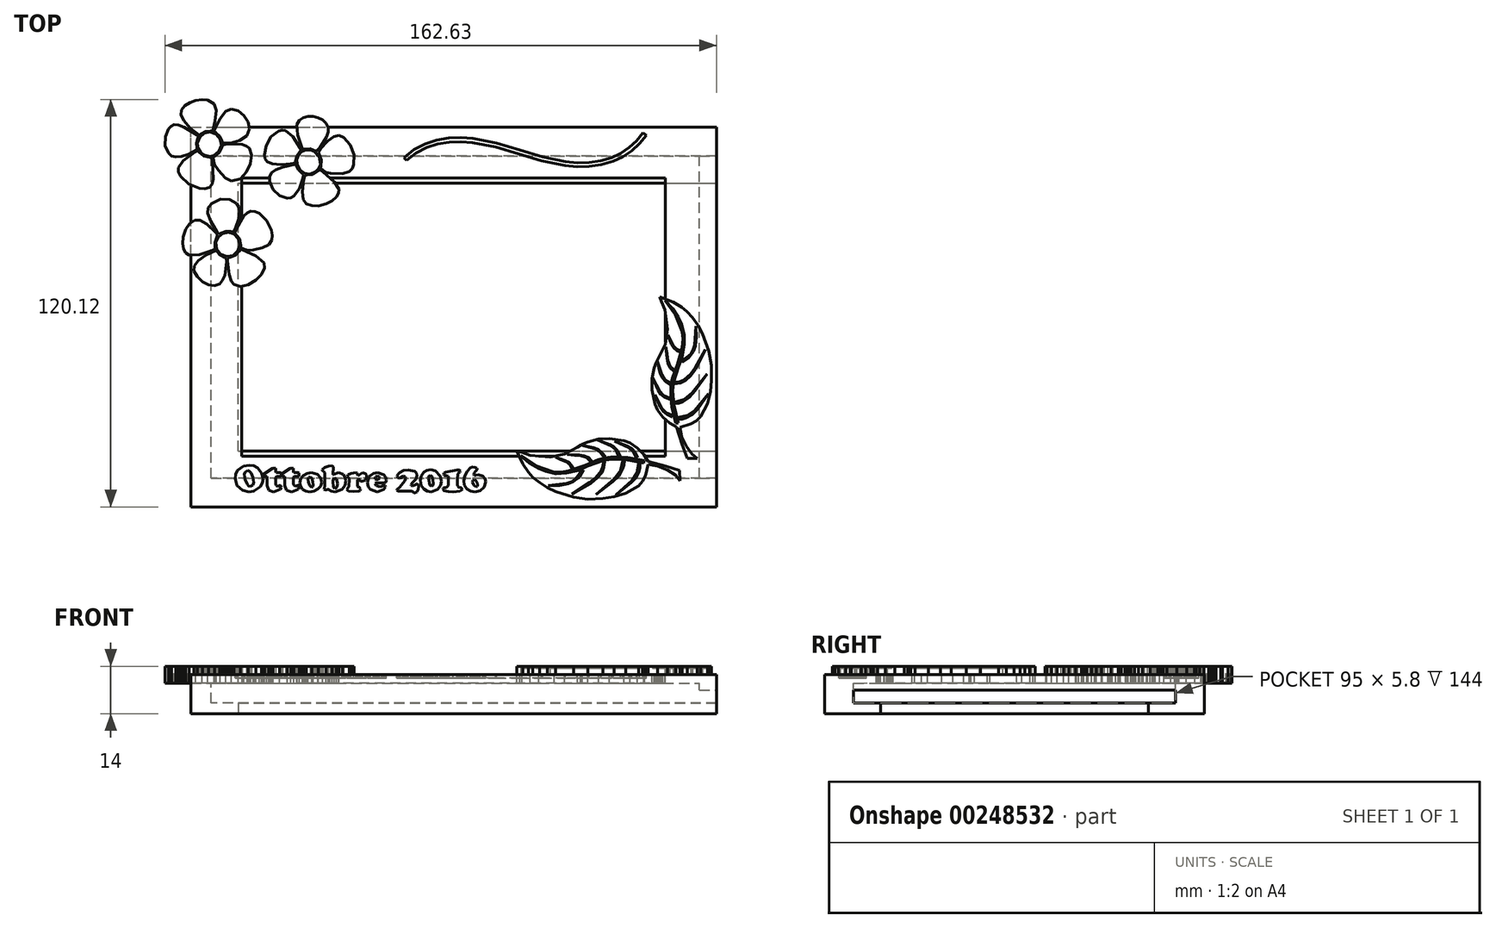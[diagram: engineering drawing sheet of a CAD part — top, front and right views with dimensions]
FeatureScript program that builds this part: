
annotation { "Feature Type Name" : "Feature", "Feature Type Description" : "" }
export const myFeature = defineFeature(function(context is Context, id is Id, definition is map)
    precondition{}
    {
        {
            var Q0;
            Q0=qCreatedBy(makeId("Top.planeOp"),FACE);
            var sketch = newSketch(context, id + "F0", { "sketchPlane" : qUnion([Q0])});
            skLineSegment(sketch, "E0", {"start": v(-51.6, -43.86) * mm, "end": v(-51.6, 51.14) * mm});
            skLineSegment(sketch, "E1", {"start": v(-51.6, 51.14) * mm, "end": v(91.4, 51.14) * mm});
            skLineSegment(sketch, "E2", {"start": v(92.4, -43.86) * mm, "end": v(-51.6, -43.86) * mm});
            skLineSegment(sketch, "E3", {"start": v(97.4, 59.64) * mm, "end": v(97.4, -52.22) * mm});
            skLineSegment(sketch, "E4", {"start": v(97.4, -52.36) * mm, "end": v(-57.31, -52.36) * mm});
            skLineSegment(sketch, "E5", {"start": v(-57.6, -52.22) * mm, "end": v(-57.6, 59.64) * mm});
            skLineSegment(sketch, "E6", {"start": v(-57.6, 59.64) * mm, "end": v(97.4, 59.64) * mm});
            skLineSegment(sketch, "E7", {"start": v(-42.6, 44.64) * mm, "end": v(-42.6, -37.36) * mm});
            skLineSegment(sketch, "E8", {"start": v(-42.6, -37.36) * mm, "end": v(82.4, -37.36) * mm});
            skLineSegment(sketch, "E9", {"start": v(82.4, -37.36) * mm, "end": v(82.4, 44.64) * mm});
            skLineSegment(sketch, "E10", {"start": v(82.4, 44.64) * mm, "end": v(-42.31, 44.64) * mm});
            skLineSegment(sketch, "E11", {"start": v(-57.6, -52.22) * mm, "end": v(-57.6, -52.36) * mm});
            skLineSegment(sketch, "E12", {"start": v(-57.6, -52.36) * mm, "end": v(-57.31, -52.36) * mm});
            skLineSegment(sketch, "E13", {"start": v(97.4, -52.22) * mm, "end": v(97.4, -52.36) * mm});
            skLineSegment(sketch, "E14", {"start": v(-42.31, 44.64) * mm, "end": v(-42.6, 44.64) * mm});
            skLineSegment(sketch, "E15", {"start": v(91.4, 51.14) * mm, "end": v(97.4, 51.14) * mm});
            skLineSegment(sketch, "E16", {"start": v(92.4, -43.86) * mm, "end": v(97.4, -43.86) * mm});
            skLineSegment(sketch, "E17", {"start": v(92.4, -43.86) * mm, "end": v(92.4, 51.14) * mm});
            skLineSegment(sketch, "E18.top", {"start": v(92.4, 51.14) * mm, "end": v(97.4, 51.14) * mm});
            skLineSegment(sketch, "E18.right", {"start": v(97.4, -43.86) * mm, "end": v(97.4, 51.14) * mm});
            skSolve(sketch);
        }
        {
            var Q0;
            Q0=makeQuery(id+"F0.imprint","IMPRINT",FACE,{"disambiguationData":[TD([[makeQuery(id+"F0.imprint","IMPRINT",EDGE,{"derivedFrom":sQuery(id+"F0.wireOp",EDGE,"E0")}),-1.0]])]});
            var Q1;
            Q1=makeQuery(id+"F0.imprint","IMPRINT",FACE,{"disambiguationData":[TD([[makeQuery(id+"F0.imprint","IMPRINT",EDGE,{"derivedFrom":sQuery(id+"F0.wireOp",EDGE,"E0")}),1.0]])]});
            var Q2;
            Q2=makeQuery(id+"F0.imprint","IMPRINT",FACE,{"disambiguationData":[TD([[makeQuery(id+"F0.imprint","IMPRINT",EDGE,{"derivedFrom":sQuery(id+"F0.wireOp",EDGE,"3e203181-d2fc-4a26-8add-b23972c1667f")}),1.0]])]});
            var Q3;
            Q3=makeQuery(id+"F0.imprint","IMPRINT",FACE,{"disambiguationData":[TD([[makeQuery(id+"F0.imprint","IMPRINT",EDGE,{"derivedFrom":sQuery(id+"F0.wireOp",EDGE,"E16")}),1.0]])]});
            extrude(context, id + "F1", {"entities" : qUnion([Q0, Q1, Q2, Q3]), "depth" : 2.5 * mm});
        }
        {
            var Q0;
            Q0=makeQuery(id+"F0.imprint","IMPRINT",FACE,{"disambiguationData":[TD([[makeQuery(id+"F0.imprint","IMPRINT",EDGE,{"derivedFrom":sQuery(id+"F0.wireOp",EDGE,"E0")}),1.0]])]});
            extrude(context, id + "F2", {"entities" : qUnion([Q0]), "operationType" : NewBodyOperationType.ADD, "oppositeDirection" : true, "depth" : 9 * mm});
        }
        {
            var Q0;
            Q0=makeQuery(id+"F0.imprint","IMPRINT",FACE,{"disambiguationData":[TD([[makeQuery(id+"F0.imprint","IMPRINT",EDGE,{"derivedFrom":sQuery(id+"F0.wireOp",EDGE,"E16")}),1.0]])]});
            extrude(context, id + "F3", {"entities" : qUnion([Q0]), "operationType" : NewBodyOperationType.ADD, "oppositeDirection" : true, "depth" : 2 * mm});
        }
        {
            var Q0;
            Q0=makeQuery(id+"F1.opExtrude","CAP_FACE",FACE,{"disambiguationData":[OSD([sQuery(id+"F0.wireOp",EDGE,"E3"),sQuery(id+"F0.wireOp",EDGE,"E4"),sQuery(id+"F0.wireOp",EDGE,"E5"),sQuery(id+"F0.wireOp",EDGE,"E6"),sQuery(id+"F0.wireOp",EDGE,"E7"),sQuery(id+"F0.wireOp",EDGE,"E8"),sQuery(id+"F0.wireOp",EDGE,"E9"),sQuery(id+"F0.wireOp",EDGE,"E10"),sQuery(id+"F0.wireOp",EDGE,"E11"),sQuery(id+"F0.wireOp",EDGE,"E12"),sQuery(id+"F0.wireOp",EDGE,"E13"),sQuery(id+"F0.wireOp",EDGE,"E14")])],"isStart":false});
            var sketch = newSketch(context, id + "F4", { "sketchPlane" : qUnion([Q0])});
            skLineSegment(sketch, "E19", {"start": v(-43.34, 12.36) * mm, "end": v(-44.56, 12.62) * mm});
            skLineSegment(sketch, "E20", {"start": v(-44.56, 12.62) * mm, "end": v(-45.45, 13.22) * mm});
            skLineSegment(sketch, "E21", {"start": v(-45.45, 13.22) * mm, "end": v(-46.62, 15.86) * mm});
            skLineSegment(sketch, "E22", {"start": v(-46.62, 15.86) * mm, "end": v(-46.97, 17.25) * mm});
            skLineSegment(sketch, "E23", {"start": v(-46.97, 17.25) * mm, "end": v(-47.22, 16.26) * mm});
            skLineSegment(sketch, "E24", {"start": v(-47.22, 16.26) * mm, "end": v(-48.3, 13.7) * mm});
            skLineSegment(sketch, "E25", {"start": v(-48.3, 13.7) * mm, "end": v(-49.1, 13.03) * mm});
            skLineSegment(sketch, "E26", {"start": v(-49.1, 13.03) * mm, "end": v(-50.16, 12.66) * mm});
            skLineSegment(sketch, "E27", {"start": v(-50.16, 12.66) * mm, "end": v(-52.63, 12.87) * mm});
            skLineSegment(sketch, "E28", {"start": v(-52.63, 12.87) * mm, "end": v(-54.94, 14.2) * mm});
            skLineSegment(sketch, "E29", {"start": v(-54.94, 14.2) * mm, "end": v(-56.58, 16.2) * mm});
            skLineSegment(sketch, "E30", {"start": v(-56.58, 16.2) * mm, "end": v(-57.03, 18.45) * mm});
            skLineSegment(sketch, "E31", {"start": v(-57.03, 18.45) * mm, "end": v(-56.32, 19.86) * mm});
            skLineSegment(sketch, "E32", {"start": v(-56.32, 19.86) * mm, "end": v(-54.27, 21.6) * mm});
            skLineSegment(sketch, "E33", {"start": v(-54.27, 21.6) * mm, "end": v(-54.18, 21.75) * mm});
            skLineSegment(sketch, "E34", {"start": v(-54.18, 21.75) * mm, "end": v(-55.13, 21.62) * mm});
            skLineSegment(sketch, "E35", {"start": v(-55.13, 21.62) * mm, "end": v(-58.2, 21.58) * mm});
            skLineSegment(sketch, "E36", {"start": v(-58.2, 21.58) * mm, "end": v(-59.42, 22.34) * mm});
            skLineSegment(sketch, "E37", {"start": v(-59.42, 22.34) * mm, "end": v(-60.13, 23.68) * mm});
            skLineSegment(sketch, "E38", {"start": v(-60.13, 23.68) * mm, "end": v(-60.37, 25.4) * mm});
            skLineSegment(sketch, "E39", {"start": v(-60.37, 25.4) * mm, "end": v(-60.18, 27.31) * mm});
            skLineSegment(sketch, "E40", {"start": v(-60.18, 27.31) * mm, "end": v(-59.6, 29.19) * mm});
            skLineSegment(sketch, "E41", {"start": v(-59.6, 29.19) * mm, "end": v(-58.69, 30.83) * mm});
            skLineSegment(sketch, "E42", {"start": v(-58.69, 30.83) * mm, "end": v(-57.46, 32.04) * mm});
            skLineSegment(sketch, "E43", {"start": v(-57.46, 32.04) * mm, "end": v(-55.97, 32.62) * mm});
            skLineSegment(sketch, "E44", {"start": v(-55.97, 32.62) * mm, "end": v(-54.14, 32.17) * mm});
            skLineSegment(sketch, "E45", {"start": v(-54.14, 32.17) * mm, "end": v(-51.85, 30.54) * mm});
            skLineSegment(sketch, "E46", {"start": v(-51.85, 30.54) * mm, "end": v(-51.1, 29.93) * mm});
            skLineSegment(sketch, "E47", {"start": v(-51.1, 29.93) * mm, "end": v(-51.57, 30.85) * mm});
            skLineSegment(sketch, "E48", {"start": v(-51.57, 30.85) * mm, "end": v(-52.74, 33.3) * mm});
            skLineSegment(sketch, "E49", {"start": v(-52.74, 33.3) * mm, "end": v(-53.03, 35.08) * mm});
            skLineSegment(sketch, "E50", {"start": v(-53.03, 35.08) * mm, "end": v(-52.68, 36.16) * mm});
            skLineSegment(sketch, "E51", {"start": v(-52.68, 36.16) * mm, "end": v(-51.98, 37.1) * mm});
            skLineSegment(sketch, "E52", {"start": v(-51.98, 37.1) * mm, "end": v(-49.88, 38.4) * mm});
            skLineSegment(sketch, "E53", {"start": v(-49.88, 38.4) * mm, "end": v(-47.29, 38.79) * mm});
            skLineSegment(sketch, "E54", {"start": v(-47.29, 38.79) * mm, "end": v(-44.81, 38.05) * mm});
            skLineSegment(sketch, "E55", {"start": v(-44.81, 38.05) * mm, "end": v(-43.79, 37.16) * mm});
            skLineSegment(sketch, "E56", {"start": v(-43.79, 37.16) * mm, "end": v(-43.16, 36) * mm});
            skLineSegment(sketch, "E57", {"start": v(-43.16, 36) * mm, "end": v(-42.94, 34.58) * mm});
            skLineSegment(sketch, "E58", {"start": v(-42.94, 34.58) * mm, "end": v(-43.12, 32.88) * mm});
            skLineSegment(sketch, "E59", {"start": v(-43.12, 32.88) * mm, "end": v(-43.13, 32.45) * mm});
            skLineSegment(sketch, "E60", {"start": v(-43.13, 32.45) * mm, "end": v(-42.7, 32.97) * mm});
            skLineSegment(sketch, "E61", {"start": v(-42.7, 32.97) * mm, "end": v(-41.54, 34.37) * mm});
            skLineSegment(sketch, "E62", {"start": v(-41.54, 34.37) * mm, "end": v(-40.34, 35.1) * mm});
            skLineSegment(sketch, "E63", {"start": v(-40.34, 35.1) * mm, "end": v(-39.05, 35.17) * mm});
            skLineSegment(sketch, "E64", {"start": v(-39.05, 35.17) * mm, "end": v(-37.57, 34.63) * mm});
            skLineSegment(sketch, "E65", {"start": v(-37.57, 34.63) * mm, "end": v(-35.67, 33.07) * mm});
            skLineSegment(sketch, "E66", {"start": v(-35.67, 33.07) * mm, "end": v(-34.1, 30.87) * mm});
            skLineSegment(sketch, "E67", {"start": v(-34.1, 30.87) * mm, "end": v(-33.47, 28.96) * mm});
            skLineSegment(sketch, "E68", {"start": v(-33.47, 28.96) * mm, "end": v(-33.27, 27.17) * mm});
            skLineSegment(sketch, "E69", {"start": v(-33.27, 27.17) * mm, "end": v(-33.68, 25.67) * mm});
            skLineSegment(sketch, "E70", {"start": v(-33.68, 25.67) * mm, "end": v(-34.55, 24.6) * mm});
            skLineSegment(sketch, "E71", {"start": v(-34.55, 24.6) * mm, "end": v(-36.05, 23.87) * mm});
            skLineSegment(sketch, "E72", {"start": v(-36.05, 23.87) * mm, "end": v(-38.36, 23.31) * mm});
            skLineSegment(sketch, "E73", {"start": v(-38.36, 23.31) * mm, "end": v(-40.2, 22.94) * mm});
            skLineSegment(sketch, "E74", {"start": v(-40.2, 22.94) * mm, "end": v(-39.3, 22.45) * mm});
            skLineSegment(sketch, "E75", {"start": v(-39.3, 22.45) * mm, "end": v(-36.3, 20.38) * mm});
            skLineSegment(sketch, "E76", {"start": v(-36.3, 20.38) * mm, "end": v(-35.66, 19.35) * mm});
            skLineSegment(sketch, "E77", {"start": v(-35.66, 19.35) * mm, "end": v(-35.54, 18.28) * mm});
            skLineSegment(sketch, "E78", {"start": v(-35.54, 18.28) * mm, "end": v(-36.46, 16.1) * mm});
            skLineSegment(sketch, "E79", {"start": v(-36.46, 16.1) * mm, "end": v(-38.38, 14.15) * mm});
            skLineSegment(sketch, "E80", {"start": v(-38.38, 14.15) * mm, "end": v(-40.84, 12.78) * mm});
            skLineSegment(sketch, "E81", {"start": v(-40.84, 12.78) * mm, "end": v(-43.34, 12.36) * mm});
            skLineSegment(sketch, "E82", {"start": v(-43.34, 12.36) * mm, "end": v(-43.34, 12.36) * mm});
            skLineSegment(sketch, "E83", {"start": v(-40.74, 13.15) * mm, "end": v(-38.48, 14.47) * mm});
            skLineSegment(sketch, "E84", {"start": v(-38.48, 14.47) * mm, "end": v(-36.79, 16.2) * mm});
            skLineSegment(sketch, "E85", {"start": v(-36.79, 16.2) * mm, "end": v(-35.9, 18.02) * mm});
            skLineSegment(sketch, "E86", {"start": v(-35.9, 18.02) * mm, "end": v(-36.06, 19.6) * mm});
            skLineSegment(sketch, "E87", {"start": v(-36.06, 19.6) * mm, "end": v(-38.45, 21.6) * mm});
            skLineSegment(sketch, "E88", {"start": v(-38.45, 21.6) * mm, "end": v(-42.61, 23.57) * mm});
            skLineSegment(sketch, "E89", {"start": v(-42.61, 23.57) * mm, "end": v(-42.98, 23.7) * mm});
            skLineSegment(sketch, "E90", {"start": v(-42.98, 23.7) * mm, "end": v(-43.4, 23.02) * mm});
            skLineSegment(sketch, "E91", {"start": v(-43.4, 23.02) * mm, "end": v(-44.4, 21.86) * mm});
            skLineSegment(sketch, "E92", {"start": v(-44.4, 21.86) * mm, "end": v(-45.86, 21.25) * mm});
            skLineSegment(sketch, "E93", {"start": v(-45.86, 21.25) * mm, "end": v(-46.82, 21.02) * mm});
            skLineSegment(sketch, "E94", {"start": v(-46.82, 21.02) * mm, "end": v(-46.8, 20.23) * mm});
            skLineSegment(sketch, "E95", {"start": v(-46.8, 20.23) * mm, "end": v(-46.32, 16.21) * mm});
            skLineSegment(sketch, "E96", {"start": v(-46.32, 16.21) * mm, "end": v(-45.73, 14.1) * mm});
            skLineSegment(sketch, "E97", {"start": v(-45.73, 14.1) * mm, "end": v(-44.87, 13.2) * mm});
            skLineSegment(sketch, "E98", {"start": v(-44.87, 13.2) * mm, "end": v(-43, 12.67) * mm});
            skLineSegment(sketch, "E99", {"start": v(-43, 12.67) * mm, "end": v(-40.74, 13.15) * mm});
            skLineSegment(sketch, "E100", {"start": v(-40.74, 13.15) * mm, "end": v(-40.74, 13.15) * mm});
            skLineSegment(sketch, "E101", {"start": v(-49.1, 13.41) * mm, "end": v(-48.28, 14.34) * mm});
            skLineSegment(sketch, "E102", {"start": v(-48.28, 14.34) * mm, "end": v(-47.63, 15.87) * mm});
            skLineSegment(sketch, "E103", {"start": v(-47.63, 15.87) * mm, "end": v(-47.1, 19.88) * mm});
            skLineSegment(sketch, "E104", {"start": v(-47.1, 19.88) * mm, "end": v(-47.19, 21) * mm});
            skLineSegment(sketch, "E105", {"start": v(-47.19, 21) * mm, "end": v(-47.69, 21.26) * mm});
            skLineSegment(sketch, "E106", {"start": v(-47.69, 21.26) * mm, "end": v(-49.2, 22.12) * mm});
            skLineSegment(sketch, "E107", {"start": v(-49.2, 22.12) * mm, "end": v(-50.1, 23.25) * mm});
            skLineSegment(sketch, "E108", {"start": v(-50.1, 23.25) * mm, "end": v(-53.17, 21.87) * mm});
            skLineSegment(sketch, "E109", {"start": v(-53.17, 21.87) * mm, "end": v(-55.45, 20.28) * mm});
            skLineSegment(sketch, "E110", {"start": v(-55.45, 20.28) * mm, "end": v(-56.6, 18.76) * mm});
            skLineSegment(sketch, "E111", {"start": v(-56.6, 18.76) * mm, "end": v(-56.68, 17.2) * mm});
            skLineSegment(sketch, "E112", {"start": v(-56.68, 17.2) * mm, "end": v(-55.73, 15.48) * mm});
            skLineSegment(sketch, "E113", {"start": v(-55.73, 15.48) * mm, "end": v(-54.2, 14.02) * mm});
            skLineSegment(sketch, "E114", {"start": v(-54.2, 14.02) * mm, "end": v(-52.44, 13.15) * mm});
            skLineSegment(sketch, "E115", {"start": v(-52.44, 13.15) * mm, "end": v(-50.68, 12.92) * mm});
            skLineSegment(sketch, "E116", {"start": v(-50.68, 12.92) * mm, "end": v(-49.1, 13.41) * mm});
            skLineSegment(sketch, "E117", {"start": v(-45.15, 21.8) * mm, "end": v(-43.7, 23.13) * mm});
            skLineSegment(sketch, "E118", {"start": v(-43.7, 23.13) * mm, "end": v(-43.17, 24.9) * mm});
            skLineSegment(sketch, "E119", {"start": v(-43.17, 24.9) * mm, "end": v(-43.59, 26.7) * mm});
            skLineSegment(sketch, "E120", {"start": v(-43.59, 26.7) * mm, "end": v(-44.96, 28.14) * mm});
            skLineSegment(sketch, "E121", {"start": v(-44.96, 28.14) * mm, "end": v(-46.58, 28.61) * mm});
            skLineSegment(sketch, "E122", {"start": v(-46.58, 28.61) * mm, "end": v(-48.2, 28.27) * mm});
            skLineSegment(sketch, "E123", {"start": v(-48.2, 28.27) * mm, "end": v(-49.5, 27.25) * mm});
            skLineSegment(sketch, "E124", {"start": v(-49.5, 27.25) * mm, "end": v(-50.18, 25.69) * mm});
            skLineSegment(sketch, "E125", {"start": v(-50.18, 25.69) * mm, "end": v(-49.95, 23.69) * mm});
            skLineSegment(sketch, "E126", {"start": v(-49.95, 23.69) * mm, "end": v(-48.79, 22.19) * mm});
            skLineSegment(sketch, "E127", {"start": v(-48.79, 22.19) * mm, "end": v(-47.07, 21.47) * mm});
            skLineSegment(sketch, "E128", {"start": v(-47.07, 21.47) * mm, "end": v(-45.15, 21.8) * mm});
            skLineSegment(sketch, "E129", {"start": v(-36.53, 24.04) * mm, "end": v(-34.66, 24.94) * mm});
            skLineSegment(sketch, "E130", {"start": v(-34.66, 24.94) * mm, "end": v(-33.79, 26.31) * mm});
            skLineSegment(sketch, "E131", {"start": v(-33.79, 26.31) * mm, "end": v(-33.6, 27.72) * mm});
            skLineSegment(sketch, "E132", {"start": v(-33.6, 27.72) * mm, "end": v(-33.82, 29.2) * mm});
            skLineSegment(sketch, "E133", {"start": v(-33.82, 29.2) * mm, "end": v(-35.22, 32.07) * mm});
            skLineSegment(sketch, "E134", {"start": v(-35.22, 32.07) * mm, "end": v(-37.45, 34.18) * mm});
            skLineSegment(sketch, "E135", {"start": v(-37.45, 34.18) * mm, "end": v(-38.7, 34.73) * mm});
            skLineSegment(sketch, "E136", {"start": v(-38.7, 34.73) * mm, "end": v(-39.98, 34.8) * mm});
            skLineSegment(sketch, "E137", {"start": v(-39.98, 34.8) * mm, "end": v(-40.97, 34.4) * mm});
            skLineSegment(sketch, "E138", {"start": v(-40.97, 34.4) * mm, "end": v(-41.98, 33.43) * mm});
            skLineSegment(sketch, "E139", {"start": v(-41.98, 33.43) * mm, "end": v(-44.19, 29.65) * mm});
            skLineSegment(sketch, "E140", {"start": v(-44.19, 29.65) * mm, "end": v(-44.66, 28.55) * mm});
            skLineSegment(sketch, "E141", {"start": v(-44.66, 28.55) * mm, "end": v(-44.5, 28.24) * mm});
            skLineSegment(sketch, "E142", {"start": v(-44.5, 28.24) * mm, "end": v(-43.3, 26.78) * mm});
            skLineSegment(sketch, "E143", {"start": v(-43.3, 26.78) * mm, "end": v(-42.87, 24.64) * mm});
            skLineSegment(sketch, "E144", {"start": v(-42.87, 24.64) * mm, "end": v(-42.86, 24.04) * mm});
            skLineSegment(sketch, "E145", {"start": v(-42.86, 24.04) * mm, "end": v(-41.98, 23.68) * mm});
            skLineSegment(sketch, "E146", {"start": v(-41.98, 23.68) * mm, "end": v(-40.82, 23.35) * mm});
            skLineSegment(sketch, "E147", {"start": v(-40.82, 23.35) * mm, "end": v(-39.23, 23.48) * mm});
            skLineSegment(sketch, "E148", {"start": v(-39.23, 23.48) * mm, "end": v(-36.53, 24.04) * mm});
            skLineSegment(sketch, "E149", {"start": v(-36.53, 24.04) * mm, "end": v(-36.53, 24.04) * mm});
            skLineSegment(sketch, "E150", {"start": v(-51.58, 23.12) * mm, "end": v(-50.39, 23.72) * mm});
            skLineSegment(sketch, "E151", {"start": v(-50.39, 23.72) * mm, "end": v(-50.45, 24.04) * mm});
            skLineSegment(sketch, "E152", {"start": v(-50.45, 24.04) * mm, "end": v(-50.5, 25.63) * mm});
            skLineSegment(sketch, "E153", {"start": v(-50.5, 25.63) * mm, "end": v(-49.97, 27.08) * mm});
            skLineSegment(sketch, "E154", {"start": v(-49.97, 27.08) * mm, "end": v(-49.67, 27.81) * mm});
            skLineSegment(sketch, "E155", {"start": v(-49.67, 27.81) * mm, "end": v(-50.35, 28.65) * mm});
            skLineSegment(sketch, "E156", {"start": v(-50.35, 28.65) * mm, "end": v(-52.93, 31) * mm});
            skLineSegment(sketch, "E157", {"start": v(-52.93, 31) * mm, "end": v(-54.99, 32.2) * mm});
            skLineSegment(sketch, "E158", {"start": v(-54.99, 32.2) * mm, "end": v(-56.52, 32.14) * mm});
            skLineSegment(sketch, "E159", {"start": v(-56.52, 32.14) * mm, "end": v(-57.97, 31.18) * mm});
            skLineSegment(sketch, "E160", {"start": v(-57.97, 31.18) * mm, "end": v(-59.14, 29.48) * mm});
            skLineSegment(sketch, "E161", {"start": v(-59.14, 29.48) * mm, "end": v(-59.89, 27.22) * mm});
            skLineSegment(sketch, "E162", {"start": v(-59.89, 27.22) * mm, "end": v(-60.04, 25.31) * mm});
            skLineSegment(sketch, "E163", {"start": v(-60.04, 25.31) * mm, "end": v(-59.77, 23.7) * mm});
            skLineSegment(sketch, "E164", {"start": v(-59.77, 23.7) * mm, "end": v(-59.13, 22.51) * mm});
            skLineSegment(sketch, "E165", {"start": v(-59.13, 22.51) * mm, "end": v(-58.14, 21.87) * mm});
            skLineSegment(sketch, "E166", {"start": v(-58.14, 21.87) * mm, "end": v(-55.11, 21.96) * mm});
            skLineSegment(sketch, "E167", {"start": v(-55.11, 21.96) * mm, "end": v(-51.58, 23.12) * mm});
            skLineSegment(sketch, "E168", {"start": v(-44.4, 29.96) * mm, "end": v(-43.52, 32.5) * mm});
            skLineSegment(sketch, "E169", {"start": v(-43.52, 32.5) * mm, "end": v(-43.28, 35.02) * mm});
            skLineSegment(sketch, "E170", {"start": v(-43.28, 35.02) * mm, "end": v(-43.54, 36.18) * mm});
            skLineSegment(sketch, "E171", {"start": v(-43.54, 36.18) * mm, "end": v(-44.17, 37.12) * mm});
            skLineSegment(sketch, "E172", {"start": v(-44.17, 37.12) * mm, "end": v(-46.22, 38.3) * mm});
            skLineSegment(sketch, "E173", {"start": v(-46.22, 38.3) * mm, "end": v(-48.84, 38.36) * mm});
            skLineSegment(sketch, "E174", {"start": v(-48.84, 38.36) * mm, "end": v(-51.42, 37.18) * mm});
            skLineSegment(sketch, "E175", {"start": v(-51.42, 37.18) * mm, "end": v(-52.5, 35.85) * mm});
            skLineSegment(sketch, "E176", {"start": v(-52.5, 35.85) * mm, "end": v(-52.63, 34.15) * mm});
            skLineSegment(sketch, "E177", {"start": v(-52.63, 34.15) * mm, "end": v(-51.78, 31.89) * mm});
            skLineSegment(sketch, "E178", {"start": v(-51.78, 31.89) * mm, "end": v(-49.93, 28.87) * mm});
            skLineSegment(sketch, "E179", {"start": v(-49.93, 28.87) * mm, "end": v(-49.33, 28.13) * mm});
            skLineSegment(sketch, "E180", {"start": v(-49.33, 28.13) * mm, "end": v(-48.74, 28.36) * mm});
            skLineSegment(sketch, "E181", {"start": v(-48.74, 28.36) * mm, "end": v(-47.29, 28.92) * mm});
            skLineSegment(sketch, "E182", {"start": v(-47.29, 28.92) * mm, "end": v(-45.77, 28.82) * mm});
            skLineSegment(sketch, "E183", {"start": v(-45.77, 28.82) * mm, "end": v(-45.05, 28.8) * mm});
            skLineSegment(sketch, "E184", {"start": v(-45.05, 28.8) * mm, "end": v(-44.4, 29.96) * mm});
            skLineSegment(sketch, "E185", {"start": v(-44.4, 29.96) * mm, "end": v(-44.4, 29.96) * mm});
            skLineSegment(sketch, "E186", {"start": v(-20.43, 36.02) * mm, "end": v(-22.8, 36.34) * mm});
            skLineSegment(sketch, "E187", {"start": v(-22.8, 36.34) * mm, "end": v(-24.44, 37.43) * mm});
            skLineSegment(sketch, "E188", {"start": v(-24.44, 37.43) * mm, "end": v(-25, 39.14) * mm});
            skLineSegment(sketch, "E189", {"start": v(-25, 39.14) * mm, "end": v(-25.02, 41.53) * mm});
            skLineSegment(sketch, "E190", {"start": v(-25.02, 41.53) * mm, "end": v(-25.05, 41.87) * mm});
            skLineSegment(sketch, "E191", {"start": v(-25.05, 41.87) * mm, "end": v(-25.5, 41.08) * mm});
            skLineSegment(sketch, "E192", {"start": v(-25.5, 41.08) * mm, "end": v(-26.76, 39.28) * mm});
            skLineSegment(sketch, "E193", {"start": v(-26.76, 39.28) * mm, "end": v(-28.2, 38.37) * mm});
            skLineSegment(sketch, "E194", {"start": v(-28.2, 38.37) * mm, "end": v(-29.84, 38.34) * mm});
            skLineSegment(sketch, "E195", {"start": v(-29.84, 38.34) * mm, "end": v(-31.68, 39.2) * mm});
            skLineSegment(sketch, "E196", {"start": v(-31.68, 39.2) * mm, "end": v(-33.33, 40.7) * mm});
            skLineSegment(sketch, "E197", {"start": v(-33.33, 40.7) * mm, "end": v(-34.4, 42.49) * mm});
            skLineSegment(sketch, "E198", {"start": v(-34.4, 42.49) * mm, "end": v(-34.77, 44.32) * mm});
            skLineSegment(sketch, "E199", {"start": v(-34.77, 44.32) * mm, "end": v(-34.36, 45.95) * mm});
            skLineSegment(sketch, "E200", {"start": v(-34.36, 45.95) * mm, "end": v(-33.02, 47.11) * mm});
            skLineSegment(sketch, "E201", {"start": v(-33.02, 47.11) * mm, "end": v(-31.14, 47.93) * mm});
            skLineSegment(sketch, "E202", {"start": v(-31.14, 47.93) * mm, "end": v(-30.94, 48.1) * mm});
            skLineSegment(sketch, "E203", {"start": v(-30.94, 48.1) * mm, "end": v(-31.99, 48.25) * mm});
            skLineSegment(sketch, "E204", {"start": v(-31.99, 48.25) * mm, "end": v(-33.83, 48.53) * mm});
            skLineSegment(sketch, "E205", {"start": v(-33.83, 48.53) * mm, "end": v(-35.08, 49.04) * mm});
            skLineSegment(sketch, "E206", {"start": v(-35.08, 49.04) * mm, "end": v(-35.82, 49.85) * mm});
            skLineSegment(sketch, "E207", {"start": v(-35.82, 49.85) * mm, "end": v(-36.18, 51.05) * mm});
            skLineSegment(sketch, "E208", {"start": v(-36.18, 51.05) * mm, "end": v(-36.18, 52.66) * mm});
            skLineSegment(sketch, "E209", {"start": v(-36.18, 52.66) * mm, "end": v(-35.77, 54.27) * mm});
            skLineSegment(sketch, "E210", {"start": v(-35.77, 54.27) * mm, "end": v(-34.03, 57.12) * mm});
            skLineSegment(sketch, "E211", {"start": v(-34.03, 57.12) * mm, "end": v(-31.62, 58.87) * mm});
            skLineSegment(sketch, "E212", {"start": v(-31.62, 58.87) * mm, "end": v(-30.37, 59.1) * mm});
            skLineSegment(sketch, "E213", {"start": v(-30.37, 59.1) * mm, "end": v(-29.2, 58.8) * mm});
            skLineSegment(sketch, "E214", {"start": v(-29.2, 58.8) * mm, "end": v(-27.76, 57.55) * mm});
            skLineSegment(sketch, "E215", {"start": v(-27.76, 57.55) * mm, "end": v(-26.3, 55.66) * mm});
            skLineSegment(sketch, "E216", {"start": v(-26.3, 55.66) * mm, "end": v(-26, 55.3) * mm});
            skLineSegment(sketch, "E217", {"start": v(-26, 55.3) * mm, "end": v(-26.04, 55.62) * mm});
            skLineSegment(sketch, "E218", {"start": v(-26.04, 55.62) * mm, "end": v(-26.79, 59.6) * mm});
            skLineSegment(sketch, "E219", {"start": v(-26.79, 59.6) * mm, "end": v(-26.54, 60.73) * mm});
            skLineSegment(sketch, "E220", {"start": v(-26.54, 60.73) * mm, "end": v(-25.93, 61.67) * mm});
            skLineSegment(sketch, "E221", {"start": v(-25.93, 61.67) * mm, "end": v(-23.91, 62.9) * mm});
            skLineSegment(sketch, "E222", {"start": v(-23.91, 62.9) * mm, "end": v(-21.3, 63.11) * mm});
            skLineSegment(sketch, "E223", {"start": v(-21.3, 63.11) * mm, "end": v(-18.65, 62.13) * mm});
            skLineSegment(sketch, "E224", {"start": v(-18.65, 62.13) * mm, "end": v(-17.48, 61.07) * mm});
            skLineSegment(sketch, "E225", {"start": v(-17.48, 61.07) * mm, "end": v(-16.87, 59.8) * mm});
            skLineSegment(sketch, "E226", {"start": v(-16.87, 59.8) * mm, "end": v(-16.83, 58.3) * mm});
            skLineSegment(sketch, "E227", {"start": v(-16.83, 58.3) * mm, "end": v(-17.34, 56.5) * mm});
            skLineSegment(sketch, "E228", {"start": v(-17.34, 56.5) * mm, "end": v(-17.67, 55.62) * mm});
            skLineSegment(sketch, "E229", {"start": v(-17.67, 55.62) * mm, "end": v(-16.83, 56.26) * mm});
            skLineSegment(sketch, "E230", {"start": v(-16.83, 56.26) * mm, "end": v(-14.5, 57.5) * mm});
            skLineSegment(sketch, "E231", {"start": v(-14.5, 57.5) * mm, "end": v(-13.13, 57.31) * mm});
            skLineSegment(sketch, "E232", {"start": v(-13.13, 57.31) * mm, "end": v(-11.88, 56.53) * mm});
            skLineSegment(sketch, "E233", {"start": v(-11.88, 56.53) * mm, "end": v(-9.9, 53.74) * mm});
            skLineSegment(sketch, "E234", {"start": v(-9.9, 53.74) * mm, "end": v(-9.07, 50.24) * mm});
            skLineSegment(sketch, "E235", {"start": v(-9.07, 50.24) * mm, "end": v(-9.23, 48.56) * mm});
            skLineSegment(sketch, "E236", {"start": v(-9.23, 48.56) * mm, "end": v(-9.86, 47.11) * mm});
            skLineSegment(sketch, "E237", {"start": v(-9.86, 47.11) * mm, "end": v(-10.74, 46.2) * mm});
            skLineSegment(sketch, "E238", {"start": v(-10.74, 46.2) * mm, "end": v(-11.94, 45.67) * mm});
            skLineSegment(sketch, "E239", {"start": v(-11.94, 45.67) * mm, "end": v(-15.95, 45.68) * mm});
            skLineSegment(sketch, "E240", {"start": v(-15.95, 45.68) * mm, "end": v(-17.03, 45.75) * mm});
            skLineSegment(sketch, "E241", {"start": v(-17.03, 45.75) * mm, "end": v(-16.3, 44.98) * mm});
            skLineSegment(sketch, "E242", {"start": v(-16.3, 44.98) * mm, "end": v(-14.6, 43.25) * mm});
            skLineSegment(sketch, "E243", {"start": v(-14.6, 43.25) * mm, "end": v(-13.7, 41.79) * mm});
            skLineSegment(sketch, "E244", {"start": v(-13.7, 41.79) * mm, "end": v(-13.57, 40.47) * mm});
            skLineSegment(sketch, "E245", {"start": v(-13.57, 40.47) * mm, "end": v(-14.17, 39.17) * mm});
            skLineSegment(sketch, "E246", {"start": v(-14.17, 39.17) * mm, "end": v(-15.32, 38.03) * mm});
            skLineSegment(sketch, "E247", {"start": v(-15.32, 38.03) * mm, "end": v(-16.9, 37.04) * mm});
            skLineSegment(sketch, "E248", {"start": v(-16.9, 37.04) * mm, "end": v(-18.68, 36.33) * mm});
            skLineSegment(sketch, "E249", {"start": v(-18.68, 36.33) * mm, "end": v(-20.43, 36.02) * mm});
            skLineSegment(sketch, "E250", {"start": v(-17.74, 37) * mm, "end": v(-16, 37.9) * mm});
            skLineSegment(sketch, "E251", {"start": v(-16, 37.9) * mm, "end": v(-14.73, 39) * mm});
            skLineSegment(sketch, "E252", {"start": v(-14.73, 39) * mm, "end": v(-14, 40.19) * mm});
            skLineSegment(sketch, "E253", {"start": v(-14, 40.19) * mm, "end": v(-13.9, 41.36) * mm});
            skLineSegment(sketch, "E254", {"start": v(-13.9, 41.36) * mm, "end": v(-15.27, 43.54) * mm});
            skLineSegment(sketch, "E255", {"start": v(-15.27, 43.54) * mm, "end": v(-18.61, 46.46) * mm});
            skLineSegment(sketch, "E256", {"start": v(-18.61, 46.46) * mm, "end": v(-19.55, 47.1) * mm});
            skLineSegment(sketch, "E257", {"start": v(-19.55, 47.1) * mm, "end": v(-20.04, 46.74) * mm});
            skLineSegment(sketch, "E258", {"start": v(-20.04, 46.74) * mm, "end": v(-21.61, 45.7) * mm});
            skLineSegment(sketch, "E259", {"start": v(-21.61, 45.7) * mm, "end": v(-23.39, 45.5) * mm});
            skLineSegment(sketch, "E260", {"start": v(-23.39, 45.5) * mm, "end": v(-23.96, 45.44) * mm});
            skLineSegment(sketch, "E261", {"start": v(-23.96, 45.44) * mm, "end": v(-24.28, 44.18) * mm});
            skLineSegment(sketch, "E262", {"start": v(-24.28, 44.18) * mm, "end": v(-24.73, 40.6) * mm});
            skLineSegment(sketch, "E263", {"start": v(-24.73, 40.6) * mm, "end": v(-24.49, 38.22) * mm});
            skLineSegment(sketch, "E264", {"start": v(-24.49, 38.22) * mm, "end": v(-23.55, 37.06) * mm});
            skLineSegment(sketch, "E265", {"start": v(-23.55, 37.06) * mm, "end": v(-21.97, 36.44) * mm});
            skLineSegment(sketch, "E266", {"start": v(-21.97, 36.44) * mm, "end": v(-19.96, 36.41) * mm});
            skLineSegment(sketch, "E267", {"start": v(-19.96, 36.41) * mm, "end": v(-17.74, 37) * mm});
            skLineSegment(sketch, "E268", {"start": v(-27.2, 39.24) * mm, "end": v(-25.64, 41.51) * mm});
            skLineSegment(sketch, "E269", {"start": v(-25.64, 41.51) * mm, "end": v(-24.54, 44.55) * mm});
            skLineSegment(sketch, "E270", {"start": v(-24.54, 44.55) * mm, "end": v(-24.3, 45.68) * mm});
            skLineSegment(sketch, "E271", {"start": v(-24.3, 45.68) * mm, "end": v(-24.9, 46.06) * mm});
            skLineSegment(sketch, "E272", {"start": v(-24.9, 46.06) * mm, "end": v(-25.9, 47) * mm});
            skLineSegment(sketch, "E273", {"start": v(-25.9, 47) * mm, "end": v(-26.53, 48.15) * mm});
            skLineSegment(sketch, "E274", {"start": v(-26.53, 48.15) * mm, "end": v(-26.8, 48.67) * mm});
            skLineSegment(sketch, "E275", {"start": v(-26.8, 48.67) * mm, "end": v(-30.59, 47.77) * mm});
            skLineSegment(sketch, "E276", {"start": v(-30.59, 47.77) * mm, "end": v(-32.62, 46.98) * mm});
            skLineSegment(sketch, "E277", {"start": v(-32.62, 46.98) * mm, "end": v(-33.84, 46.12) * mm});
            skLineSegment(sketch, "E278", {"start": v(-33.84, 46.12) * mm, "end": v(-34.38, 45.05) * mm});
            skLineSegment(sketch, "E279", {"start": v(-34.38, 45.05) * mm, "end": v(-34.36, 43.65) * mm});
            skLineSegment(sketch, "E280", {"start": v(-34.36, 43.65) * mm, "end": v(-33.3, 41.16) * mm});
            skLineSegment(sketch, "E281", {"start": v(-33.3, 41.16) * mm, "end": v(-31.38, 39.37) * mm});
            skLineSegment(sketch, "E282", {"start": v(-31.38, 39.37) * mm, "end": v(-29.16, 38.62) * mm});
            skLineSegment(sketch, "E283", {"start": v(-29.16, 38.62) * mm, "end": v(-28.12, 38.74) * mm});
            skLineSegment(sketch, "E284", {"start": v(-28.12, 38.74) * mm, "end": v(-27.2, 39.24) * mm});
            skLineSegment(sketch, "E285", {"start": v(-10.83, 46.47) * mm, "end": v(-10.04, 47.38) * mm});
            skLineSegment(sketch, "E286", {"start": v(-10.04, 47.38) * mm, "end": v(-9.57, 48.59) * mm});
            skLineSegment(sketch, "E287", {"start": v(-9.57, 48.59) * mm, "end": v(-9.53, 51.48) * mm});
            skLineSegment(sketch, "E288", {"start": v(-9.53, 51.48) * mm, "end": v(-10.56, 54.4) * mm});
            skLineSegment(sketch, "E289", {"start": v(-10.56, 54.4) * mm, "end": v(-12.55, 56.62) * mm});
            skLineSegment(sketch, "E290", {"start": v(-12.55, 56.62) * mm, "end": v(-13.96, 57.15) * mm});
            skLineSegment(sketch, "E291", {"start": v(-13.96, 57.15) * mm, "end": v(-15.46, 56.8) * mm});
            skLineSegment(sketch, "E292", {"start": v(-15.46, 56.8) * mm, "end": v(-17.2, 55.52) * mm});
            skLineSegment(sketch, "E293", {"start": v(-17.2, 55.52) * mm, "end": v(-19.36, 53.2) * mm});
            skLineSegment(sketch, "E294", {"start": v(-19.36, 53.2) * mm, "end": v(-20.04, 52.26) * mm});
            skLineSegment(sketch, "E295", {"start": v(-20.04, 52.26) * mm, "end": v(-19.75, 51.6) * mm});
            skLineSegment(sketch, "E296", {"start": v(-19.75, 51.6) * mm, "end": v(-19.1, 49.9) * mm});
            skLineSegment(sketch, "E297", {"start": v(-19.1, 49.9) * mm, "end": v(-19.25, 48.1) * mm});
            skLineSegment(sketch, "E298", {"start": v(-19.25, 48.1) * mm, "end": v(-19.34, 47.5) * mm});
            skLineSegment(sketch, "E299", {"start": v(-19.34, 47.5) * mm, "end": v(-18.65, 46.88) * mm});
            skLineSegment(sketch, "E300", {"start": v(-18.65, 46.88) * mm, "end": v(-17.74, 46.3) * mm});
            skLineSegment(sketch, "E301", {"start": v(-17.74, 46.3) * mm, "end": v(-16.44, 46.06) * mm});
            skLineSegment(sketch, "E302", {"start": v(-16.44, 46.06) * mm, "end": v(-12.94, 45.89) * mm});
            skLineSegment(sketch, "E303", {"start": v(-12.94, 45.89) * mm, "end": v(-10.83, 46.47) * mm});
            skLineSegment(sketch, "E304", {"start": v(-20.76, 46.52) * mm, "end": v(-19.88, 47.48) * mm});
            skLineSegment(sketch, "E305", {"start": v(-19.88, 47.48) * mm, "end": v(-19.44, 48.59) * mm});
            skLineSegment(sketch, "E306", {"start": v(-19.44, 48.59) * mm, "end": v(-19.72, 50.85) * mm});
            skLineSegment(sketch, "E307", {"start": v(-19.72, 50.85) * mm, "end": v(-21.24, 52.54) * mm});
            skLineSegment(sketch, "E308", {"start": v(-21.24, 52.54) * mm, "end": v(-22.35, 52.92) * mm});
            skLineSegment(sketch, "E309", {"start": v(-22.35, 52.92) * mm, "end": v(-23.65, 52.87) * mm});
            skLineSegment(sketch, "E310", {"start": v(-23.65, 52.87) * mm, "end": v(-24.96, 52.32) * mm});
            skLineSegment(sketch, "E311", {"start": v(-24.96, 52.32) * mm, "end": v(-25.87, 51.39) * mm});
            skLineSegment(sketch, "E312", {"start": v(-25.87, 51.39) * mm, "end": v(-26.32, 50.14) * mm});
            skLineSegment(sketch, "E313", {"start": v(-26.32, 50.14) * mm, "end": v(-26.27, 48.69) * mm});
            skLineSegment(sketch, "E314", {"start": v(-26.27, 48.69) * mm, "end": v(-25.47, 47) * mm});
            skLineSegment(sketch, "E315", {"start": v(-25.47, 47) * mm, "end": v(-24.1, 46) * mm});
            skLineSegment(sketch, "E316", {"start": v(-24.1, 46) * mm, "end": v(-22.43, 45.8) * mm});
            skLineSegment(sketch, "E317", {"start": v(-22.43, 45.8) * mm, "end": v(-20.76, 46.52) * mm});
            skLineSegment(sketch, "E318", {"start": v(-26.75, 49.44) * mm, "end": v(-26.37, 51.04) * mm});
            skLineSegment(sketch, "E319", {"start": v(-26.37, 51.04) * mm, "end": v(-25.42, 52.36) * mm});
            skLineSegment(sketch, "E320", {"start": v(-25.42, 52.36) * mm, "end": v(-25.02, 52.79) * mm});
            skLineSegment(sketch, "E321", {"start": v(-25.02, 52.79) * mm, "end": v(-27.5, 56.76) * mm});
            skLineSegment(sketch, "E322", {"start": v(-27.5, 56.76) * mm, "end": v(-29.6, 58.6) * mm});
            skLineSegment(sketch, "E323", {"start": v(-29.6, 58.6) * mm, "end": v(-30.62, 58.77) * mm});
            skLineSegment(sketch, "E324", {"start": v(-30.62, 58.77) * mm, "end": v(-31.75, 58.49) * mm});
            skLineSegment(sketch, "E325", {"start": v(-31.75, 58.49) * mm, "end": v(-33.94, 56.78) * mm});
            skLineSegment(sketch, "E326", {"start": v(-33.94, 56.78) * mm, "end": v(-35.42, 54.19) * mm});
            skLineSegment(sketch, "E327", {"start": v(-35.42, 54.19) * mm, "end": v(-35.92, 51.49) * mm});
            skLineSegment(sketch, "E328", {"start": v(-35.92, 51.49) * mm, "end": v(-35.7, 50.34) * mm});
            skLineSegment(sketch, "E329", {"start": v(-35.7, 50.34) * mm, "end": v(-35.14, 49.46) * mm});
            skLineSegment(sketch, "E330", {"start": v(-35.14, 49.46) * mm, "end": v(-33.66, 48.81) * mm});
            skLineSegment(sketch, "E331", {"start": v(-33.66, 48.81) * mm, "end": v(-31.06, 48.52) * mm});
            skLineSegment(sketch, "E332", {"start": v(-31.06, 48.52) * mm, "end": v(-28.08, 48.78) * mm});
            skLineSegment(sketch, "E333", {"start": v(-28.08, 48.78) * mm, "end": v(-26.76, 49.04) * mm});
            skLineSegment(sketch, "E334", {"start": v(-26.76, 49.04) * mm, "end": v(-26.75, 49.44) * mm});
            skLineSegment(sketch, "E335", {"start": v(-19.45, 53.59) * mm, "end": v(-17.58, 56.73) * mm});
            skLineSegment(sketch, "E336", {"start": v(-17.58, 56.73) * mm, "end": v(-17.14, 58.24) * mm});
            skLineSegment(sketch, "E337", {"start": v(-17.14, 58.24) * mm, "end": v(-17.14, 59.5) * mm});
            skLineSegment(sketch, "E338", {"start": v(-17.14, 59.5) * mm, "end": v(-17.71, 60.8) * mm});
            skLineSegment(sketch, "E339", {"start": v(-17.71, 60.8) * mm, "end": v(-18.74, 61.78) * mm});
            skLineSegment(sketch, "E340", {"start": v(-18.74, 61.78) * mm, "end": v(-20.08, 62.45) * mm});
            skLineSegment(sketch, "E341", {"start": v(-20.08, 62.45) * mm, "end": v(-21.58, 62.78) * mm});
            skLineSegment(sketch, "E342", {"start": v(-21.58, 62.78) * mm, "end": v(-23.1, 62.76) * mm});
            skLineSegment(sketch, "E343", {"start": v(-23.1, 62.76) * mm, "end": v(-24.5, 62.37) * mm});
            skLineSegment(sketch, "E344", {"start": v(-24.5, 62.37) * mm, "end": v(-25.63, 61.6) * mm});
            skLineSegment(sketch, "E345", {"start": v(-25.63, 61.6) * mm, "end": v(-26.35, 60.43) * mm});
            skLineSegment(sketch, "E346", {"start": v(-26.35, 60.43) * mm, "end": v(-26.15, 57.35) * mm});
            skLineSegment(sketch, "E347", {"start": v(-26.15, 57.35) * mm, "end": v(-24.77, 53.1) * mm});
            skLineSegment(sketch, "E348", {"start": v(-24.77, 53.1) * mm, "end": v(-23.88, 53.14) * mm});
            skLineSegment(sketch, "E349", {"start": v(-23.88, 53.14) * mm, "end": v(-22.46, 53.27) * mm});
            skLineSegment(sketch, "E350", {"start": v(-22.46, 53.27) * mm, "end": v(-20.63, 52.54) * mm});
            skLineSegment(sketch, "E351", {"start": v(-20.63, 52.54) * mm, "end": v(-19.45, 53.59) * mm});
            skLineSegment(sketch, "E352", {"start": v(-53.8, 41.12) * mm, "end": v(-56.24, 41.5) * mm});
            skLineSegment(sketch, "E353", {"start": v(-56.24, 41.5) * mm, "end": v(-58.58, 42.62) * mm});
            skLineSegment(sketch, "E354", {"start": v(-58.58, 42.62) * mm, "end": v(-60.46, 44.26) * mm});
            skLineSegment(sketch, "E355", {"start": v(-60.46, 44.26) * mm, "end": v(-61.53, 46.18) * mm});
            skLineSegment(sketch, "E356", {"start": v(-61.53, 46.18) * mm, "end": v(-61.68, 47.26) * mm});
            skLineSegment(sketch, "E357", {"start": v(-61.68, 47.26) * mm, "end": v(-61.45, 48.23) * mm});
            skLineSegment(sketch, "E358", {"start": v(-61.45, 48.23) * mm, "end": v(-59.67, 50.33) * mm});
            skLineSegment(sketch, "E359", {"start": v(-59.67, 50.33) * mm, "end": v(-58.93, 50.97) * mm});
            skLineSegment(sketch, "E360", {"start": v(-58.93, 50.97) * mm, "end": v(-60.48, 50.68) * mm});
            skLineSegment(sketch, "E361", {"start": v(-60.48, 50.68) * mm, "end": v(-62.43, 50.46) * mm});
            skLineSegment(sketch, "E362", {"start": v(-62.43, 50.46) * mm, "end": v(-63.64, 50.94) * mm});
            skLineSegment(sketch, "E363", {"start": v(-63.64, 50.94) * mm, "end": v(-64.94, 52.4) * mm});
            skLineSegment(sketch, "E364", {"start": v(-64.94, 52.4) * mm, "end": v(-65.58, 54.43) * mm});
            skLineSegment(sketch, "E365", {"start": v(-65.58, 54.43) * mm, "end": v(-65.53, 56.7) * mm});
            skLineSegment(sketch, "E366", {"start": v(-65.53, 56.7) * mm, "end": v(-64.73, 58.87) * mm});
            skLineSegment(sketch, "E367", {"start": v(-64.73, 58.87) * mm, "end": v(-63.78, 60.05) * mm});
            skLineSegment(sketch, "E368", {"start": v(-63.78, 60.05) * mm, "end": v(-62.65, 60.62) * mm});
            skLineSegment(sketch, "E369", {"start": v(-62.65, 60.62) * mm, "end": v(-61.27, 60.58) * mm});
            skLineSegment(sketch, "E370", {"start": v(-61.27, 60.58) * mm, "end": v(-59.56, 59.95) * mm});
            skLineSegment(sketch, "E371", {"start": v(-59.56, 59.95) * mm, "end": v(-58.6, 59.5) * mm});
            skLineSegment(sketch, "E372", {"start": v(-58.6, 59.5) * mm, "end": v(-59.27, 60.43) * mm});
            skLineSegment(sketch, "E373", {"start": v(-59.27, 60.43) * mm, "end": v(-60.7, 62.66) * mm});
            skLineSegment(sketch, "E374", {"start": v(-60.7, 62.66) * mm, "end": v(-60.88, 64.28) * mm});
            skLineSegment(sketch, "E375", {"start": v(-60.88, 64.28) * mm, "end": v(-60.35, 65.38) * mm});
            skLineSegment(sketch, "E376", {"start": v(-60.35, 65.38) * mm, "end": v(-59.44, 66.33) * mm});
            skLineSegment(sketch, "E377", {"start": v(-59.44, 66.33) * mm, "end": v(-56.9, 67.68) * mm});
            skLineSegment(sketch, "E378", {"start": v(-56.9, 67.68) * mm, "end": v(-53.94, 68.1) * mm});
            skLineSegment(sketch, "E379", {"start": v(-53.94, 68.1) * mm, "end": v(-51.29, 67.36) * mm});
            skLineSegment(sketch, "E380", {"start": v(-51.29, 67.36) * mm, "end": v(-50.32, 66.49) * mm});
            skLineSegment(sketch, "E381", {"start": v(-50.32, 66.49) * mm, "end": v(-49.8, 65.3) * mm});
            skLineSegment(sketch, "E382", {"start": v(-49.8, 65.3) * mm, "end": v(-49.72, 63.7) * mm});
            skLineSegment(sketch, "E383", {"start": v(-49.72, 63.7) * mm, "end": v(-50.04, 61.58) * mm});
            skLineSegment(sketch, "E384", {"start": v(-50.04, 61.58) * mm, "end": v(-50.16, 60.84) * mm});
            skLineSegment(sketch, "E385", {"start": v(-50.16, 60.84) * mm, "end": v(-49.91, 61.16) * mm});
            skLineSegment(sketch, "E386", {"start": v(-49.91, 61.16) * mm, "end": v(-47.34, 64.72) * mm});
            skLineSegment(sketch, "E387", {"start": v(-47.34, 64.72) * mm, "end": v(-46.27, 65.24) * mm});
            skLineSegment(sketch, "E388", {"start": v(-46.27, 65.24) * mm, "end": v(-45.06, 65.27) * mm});
            skLineSegment(sketch, "E389", {"start": v(-45.06, 65.27) * mm, "end": v(-42.6, 64.12) * mm});
            skLineSegment(sketch, "E390", {"start": v(-42.6, 64.12) * mm, "end": v(-40.7, 61.85) * mm});
            skLineSegment(sketch, "E391", {"start": v(-40.7, 61.85) * mm, "end": v(-40.17, 60.47) * mm});
            skLineSegment(sketch, "E392", {"start": v(-40.17, 60.47) * mm, "end": v(-40.06, 59.02) * mm});
            skLineSegment(sketch, "E393", {"start": v(-40.06, 59.02) * mm, "end": v(-40.34, 57.79) * mm});
            skLineSegment(sketch, "E394", {"start": v(-40.34, 57.79) * mm, "end": v(-40.98, 56.78) * mm});
            skLineSegment(sketch, "E395", {"start": v(-40.98, 56.78) * mm, "end": v(-43.43, 55.32) * mm});
            skLineSegment(sketch, "E396", {"start": v(-43.43, 55.32) * mm, "end": v(-43.97, 55.06) * mm});
            skLineSegment(sketch, "E397", {"start": v(-43.97, 55.06) * mm, "end": v(-43.42, 54.92) * mm});
            skLineSegment(sketch, "E398", {"start": v(-43.42, 54.92) * mm, "end": v(-40.64, 54.1) * mm});
            skLineSegment(sketch, "E399", {"start": v(-40.64, 54.1) * mm, "end": v(-39.9, 53.26) * mm});
            skLineSegment(sketch, "E400", {"start": v(-39.9, 53.26) * mm, "end": v(-39.48, 52.07) * mm});
            skLineSegment(sketch, "E401", {"start": v(-39.48, 52.07) * mm, "end": v(-39.5, 49.69) * mm});
            skLineSegment(sketch, "E402", {"start": v(-39.5, 49.69) * mm, "end": v(-40.34, 47.22) * mm});
            skLineSegment(sketch, "E403", {"start": v(-40.34, 47.22) * mm, "end": v(-41.8, 45.09) * mm});
            skLineSegment(sketch, "E404", {"start": v(-41.8, 45.09) * mm, "end": v(-43.68, 43.7) * mm});
            skLineSegment(sketch, "E405", {"start": v(-43.68, 43.7) * mm, "end": v(-45.17, 43.38) * mm});
            skLineSegment(sketch, "E406", {"start": v(-45.17, 43.38) * mm, "end": v(-46.62, 43.75) * mm});
            skLineSegment(sketch, "E407", {"start": v(-46.62, 43.75) * mm, "end": v(-48.14, 44.88) * mm});
            skLineSegment(sketch, "E408", {"start": v(-48.14, 44.88) * mm, "end": v(-49.83, 46.82) * mm});
            skLineSegment(sketch, "E409", {"start": v(-49.83, 46.82) * mm, "end": v(-50.67, 47.83) * mm});
            skLineSegment(sketch, "E410", {"start": v(-50.67, 47.83) * mm, "end": v(-50.65, 46.7) * mm});
            skLineSegment(sketch, "E411", {"start": v(-50.65, 46.7) * mm, "end": v(-50.7, 44.11) * mm});
            skLineSegment(sketch, "E412", {"start": v(-50.7, 44.11) * mm, "end": v(-51.2, 42.4) * mm});
            skLineSegment(sketch, "E413", {"start": v(-51.2, 42.4) * mm, "end": v(-52.2, 41.45) * mm});
            skLineSegment(sketch, "E414", {"start": v(-52.2, 41.45) * mm, "end": v(-53.8, 41.12) * mm});
            skLineSegment(sketch, "E415", {"start": v(-53.8, 41.12) * mm, "end": v(-53.8, 41.12) * mm});
            skLineSegment(sketch, "E416", {"start": v(-52.16, 41.88) * mm, "end": v(-51.4, 42.7) * mm});
            skLineSegment(sketch, "E417", {"start": v(-51.4, 42.7) * mm, "end": v(-51, 44.2) * mm});
            skLineSegment(sketch, "E418", {"start": v(-51, 44.2) * mm, "end": v(-51.22, 49.43) * mm});
            skLineSegment(sketch, "E419", {"start": v(-51.22, 49.43) * mm, "end": v(-51.43, 50.55) * mm});
            skLineSegment(sketch, "E420", {"start": v(-51.43, 50.55) * mm, "end": v(-52.03, 50.67) * mm});
            skLineSegment(sketch, "E421", {"start": v(-52.03, 50.67) * mm, "end": v(-53.76, 51.08) * mm});
            skLineSegment(sketch, "E422", {"start": v(-53.76, 51.08) * mm, "end": v(-55.15, 52.2) * mm});
            skLineSegment(sketch, "E423", {"start": v(-55.15, 52.2) * mm, "end": v(-55.65, 52.65) * mm});
            skLineSegment(sketch, "E424", {"start": v(-55.65, 52.65) * mm, "end": v(-56.52, 52.2) * mm});
            skLineSegment(sketch, "E425", {"start": v(-56.52, 52.2) * mm, "end": v(-59.88, 49.7) * mm});
            skLineSegment(sketch, "E426", {"start": v(-59.88, 49.7) * mm, "end": v(-61.33, 47.65) * mm});
            skLineSegment(sketch, "E427", {"start": v(-61.33, 47.65) * mm, "end": v(-61.3, 46.36) * mm});
            skLineSegment(sketch, "E428", {"start": v(-61.3, 46.36) * mm, "end": v(-60.7, 45.08) * mm});
            skLineSegment(sketch, "E429", {"start": v(-60.7, 45.08) * mm, "end": v(-58.28, 42.83) * mm});
            skLineSegment(sketch, "E430", {"start": v(-58.28, 42.83) * mm, "end": v(-55.1, 41.55) * mm});
            skLineSegment(sketch, "E431", {"start": v(-55.1, 41.55) * mm, "end": v(-53.53, 41.47) * mm});
            skLineSegment(sketch, "E432", {"start": v(-53.53, 41.47) * mm, "end": v(-52.16, 41.88) * mm});
            skLineSegment(sketch, "E433", {"start": v(-52.16, 41.88) * mm, "end": v(-52.16, 41.88) * mm});
            skLineSegment(sketch, "E434", {"start": v(-43.05, 44.43) * mm, "end": v(-41.2, 46.36) * mm});
            skLineSegment(sketch, "E435", {"start": v(-41.2, 46.36) * mm, "end": v(-40.04, 48.84) * mm});
            skLineSegment(sketch, "E436", {"start": v(-40.04, 48.84) * mm, "end": v(-39.7, 51.35) * mm});
            skLineSegment(sketch, "E437", {"start": v(-39.7, 51.35) * mm, "end": v(-40.38, 53.36) * mm});
            skLineSegment(sketch, "E438", {"start": v(-40.38, 53.36) * mm, "end": v(-41.22, 54.05) * mm});
            skLineSegment(sketch, "E439", {"start": v(-41.22, 54.05) * mm, "end": v(-42.54, 54.48) * mm});
            skLineSegment(sketch, "E440", {"start": v(-42.54, 54.48) * mm, "end": v(-47.03, 54.6) * mm});
            skLineSegment(sketch, "E441", {"start": v(-47.03, 54.6) * mm, "end": v(-48.28, 54.3) * mm});
            skLineSegment(sketch, "E442", {"start": v(-48.28, 54.3) * mm, "end": v(-48.4, 53.61) * mm});
            skLineSegment(sketch, "E443", {"start": v(-48.4, 53.61) * mm, "end": v(-49.2, 52.07) * mm});
            skLineSegment(sketch, "E444", {"start": v(-49.2, 52.07) * mm, "end": v(-50.58, 51) * mm});
            skLineSegment(sketch, "E445", {"start": v(-50.58, 51) * mm, "end": v(-51.03, 50.66) * mm});
            skLineSegment(sketch, "E446", {"start": v(-51.03, 50.66) * mm, "end": v(-50.93, 49.58) * mm});
            skLineSegment(sketch, "E447", {"start": v(-50.93, 49.58) * mm, "end": v(-50.63, 48.5) * mm});
            skLineSegment(sketch, "E448", {"start": v(-50.63, 48.5) * mm, "end": v(-49.52, 46.95) * mm});
            skLineSegment(sketch, "E449", {"start": v(-49.52, 46.95) * mm, "end": v(-47.4, 44.64) * mm});
            skLineSegment(sketch, "E450", {"start": v(-47.4, 44.64) * mm, "end": v(-45.61, 43.71) * mm});
            skLineSegment(sketch, "E451", {"start": v(-45.61, 43.71) * mm, "end": v(-43.05, 44.43) * mm});
            skLineSegment(sketch, "E452", {"start": v(-50.87, 51.22) * mm, "end": v(-49.3, 52.47) * mm});
            skLineSegment(sketch, "E453", {"start": v(-49.3, 52.47) * mm, "end": v(-48.64, 54.22) * mm});
            skLineSegment(sketch, "E454", {"start": v(-48.64, 54.22) * mm, "end": v(-48.92, 56.06) * mm});
            skLineSegment(sketch, "E455", {"start": v(-48.92, 56.06) * mm, "end": v(-50.2, 57.57) * mm});
            skLineSegment(sketch, "E456", {"start": v(-50.2, 57.57) * mm, "end": v(-51.97, 58.17) * mm});
            skLineSegment(sketch, "E457", {"start": v(-51.97, 58.17) * mm, "end": v(-53.67, 57.82) * mm});
            skLineSegment(sketch, "E458", {"start": v(-53.67, 57.82) * mm, "end": v(-55, 56.7) * mm});
            skLineSegment(sketch, "E459", {"start": v(-55, 56.7) * mm, "end": v(-55.64, 54.93) * mm});
            skLineSegment(sketch, "E460", {"start": v(-55.64, 54.93) * mm, "end": v(-55.44, 53.4) * mm});
            skLineSegment(sketch, "E461", {"start": v(-55.44, 53.4) * mm, "end": v(-54.68, 52.15) * mm});
            skLineSegment(sketch, "E462", {"start": v(-54.68, 52.15) * mm, "end": v(-53.49, 51.3) * mm});
            skLineSegment(sketch, "E463", {"start": v(-53.49, 51.3) * mm, "end": v(-51.98, 51) * mm});
            skLineSegment(sketch, "E464", {"start": v(-51.98, 51) * mm, "end": v(-50.87, 51.22) * mm});
            skLineSegment(sketch, "E465", {"start": v(-50.87, 51.22) * mm, "end": v(-50.87, 51.22) * mm});
            skLineSegment(sketch, "E466", {"start": v(-58.34, 51.63) * mm, "end": v(-55.86, 53.02) * mm});
            skLineSegment(sketch, "E467", {"start": v(-55.86, 53.02) * mm, "end": v(-55.85, 53.55) * mm});
            skLineSegment(sketch, "E468", {"start": v(-55.85, 53.55) * mm, "end": v(-55.97, 54.9) * mm});
            skLineSegment(sketch, "E469", {"start": v(-55.97, 54.9) * mm, "end": v(-55.56, 56.38) * mm});
            skLineSegment(sketch, "E470", {"start": v(-55.56, 56.38) * mm, "end": v(-55.3, 56.92) * mm});
            skLineSegment(sketch, "E471", {"start": v(-55.3, 56.92) * mm, "end": v(-55.84, 57.33) * mm});
            skLineSegment(sketch, "E472", {"start": v(-55.84, 57.33) * mm, "end": v(-59.64, 59.62) * mm});
            skLineSegment(sketch, "E473", {"start": v(-59.64, 59.62) * mm, "end": v(-61.3, 60.22) * mm});
            skLineSegment(sketch, "E474", {"start": v(-61.3, 60.22) * mm, "end": v(-62.5, 60.32) * mm});
            skLineSegment(sketch, "E475", {"start": v(-62.5, 60.32) * mm, "end": v(-63.43, 59.9) * mm});
            skLineSegment(sketch, "E476", {"start": v(-63.43, 59.9) * mm, "end": v(-64.2, 59.12) * mm});
            skLineSegment(sketch, "E477", {"start": v(-64.2, 59.12) * mm, "end": v(-65.15, 56.85) * mm});
            skLineSegment(sketch, "E478", {"start": v(-65.15, 56.85) * mm, "end": v(-65.23, 54.21) * mm});
            skLineSegment(sketch, "E479", {"start": v(-65.23, 54.21) * mm, "end": v(-64.27, 51.93) * mm});
            skLineSegment(sketch, "E480", {"start": v(-64.27, 51.93) * mm, "end": v(-63.29, 51.11) * mm});
            skLineSegment(sketch, "E481", {"start": v(-63.29, 51.11) * mm, "end": v(-62.04, 50.79) * mm});
            skLineSegment(sketch, "E482", {"start": v(-62.04, 50.79) * mm, "end": v(-60.43, 50.96) * mm});
            skLineSegment(sketch, "E483", {"start": v(-60.43, 50.96) * mm, "end": v(-58.34, 51.63) * mm});
            skLineSegment(sketch, "E484", {"start": v(-43.3, 55.73) * mm, "end": v(-41.13, 57.1) * mm});
            skLineSegment(sketch, "E485", {"start": v(-41.13, 57.1) * mm, "end": v(-40.37, 59.05) * mm});
            skLineSegment(sketch, "E486", {"start": v(-40.37, 59.05) * mm, "end": v(-40.73, 61.15) * mm});
            skLineSegment(sketch, "E487", {"start": v(-40.73, 61.15) * mm, "end": v(-41.93, 63.07) * mm});
            skLineSegment(sketch, "E488", {"start": v(-41.93, 63.07) * mm, "end": v(-43.67, 64.46) * mm});
            skLineSegment(sketch, "E489", {"start": v(-43.67, 64.46) * mm, "end": v(-45.63, 64.97) * mm});
            skLineSegment(sketch, "E490", {"start": v(-45.63, 64.97) * mm, "end": v(-47.28, 64.32) * mm});
            skLineSegment(sketch, "E491", {"start": v(-47.28, 64.32) * mm, "end": v(-48.99, 62.1) * mm});
            skLineSegment(sketch, "E492", {"start": v(-48.99, 62.1) * mm, "end": v(-50.85, 58.38) * mm});
            skLineSegment(sketch, "E493", {"start": v(-50.85, 58.38) * mm, "end": v(-50.22, 57.94) * mm});
            skLineSegment(sketch, "E494", {"start": v(-50.22, 57.94) * mm, "end": v(-49.05, 56.9) * mm});
            skLineSegment(sketch, "E495", {"start": v(-49.05, 56.9) * mm, "end": v(-48.45, 55.54) * mm});
            skLineSegment(sketch, "E496", {"start": v(-48.45, 55.54) * mm, "end": v(-48.16, 54.95) * mm});
            skLineSegment(sketch, "E497", {"start": v(-48.16, 54.95) * mm, "end": v(-47.01, 54.94) * mm});
            skLineSegment(sketch, "E498", {"start": v(-47.01, 54.94) * mm, "end": v(-45.89, 54.97) * mm});
            skLineSegment(sketch, "E499", {"start": v(-45.89, 54.97) * mm, "end": v(-43.3, 55.73) * mm});
            skLineSegment(sketch, "E500", {"start": v(-54.63, 57.58) * mm, "end": v(-53.3, 58.33) * mm});
            skLineSegment(sketch, "E501", {"start": v(-53.3, 58.33) * mm, "end": v(-51.87, 58.48) * mm});
            skLineSegment(sketch, "E502", {"start": v(-51.87, 58.48) * mm, "end": v(-51.3, 58.42) * mm});
            skLineSegment(sketch, "E503", {"start": v(-51.3, 58.42) * mm, "end": v(-51.17, 58.65) * mm});
            skLineSegment(sketch, "E504", {"start": v(-51.17, 58.65) * mm, "end": v(-50.43, 61.37) * mm});
            skLineSegment(sketch, "E505", {"start": v(-50.43, 61.37) * mm, "end": v(-50.05, 64.57) * mm});
            skLineSegment(sketch, "E506", {"start": v(-50.05, 64.57) * mm, "end": v(-50.75, 66.53) * mm});
            skLineSegment(sketch, "E507", {"start": v(-50.75, 66.53) * mm, "end": v(-52.65, 67.61) * mm});
            skLineSegment(sketch, "E508", {"start": v(-52.65, 67.61) * mm, "end": v(-54.33, 67.76) * mm});
            skLineSegment(sketch, "E509", {"start": v(-54.33, 67.76) * mm, "end": v(-56.16, 67.5) * mm});
            skLineSegment(sketch, "E510", {"start": v(-56.16, 67.5) * mm, "end": v(-57.9, 66.9) * mm});
            skLineSegment(sketch, "E511", {"start": v(-57.9, 66.9) * mm, "end": v(-59.35, 65.99) * mm});
            skLineSegment(sketch, "E512", {"start": v(-59.35, 65.99) * mm, "end": v(-60.4, 64.68) * mm});
            skLineSegment(sketch, "E513", {"start": v(-60.4, 64.68) * mm, "end": v(-60.52, 63.22) * mm});
            skLineSegment(sketch, "E514", {"start": v(-60.52, 63.22) * mm, "end": v(-59.68, 61.48) * mm});
            skLineSegment(sketch, "E515", {"start": v(-59.68, 61.48) * mm, "end": v(-57.85, 59.32) * mm});
            skLineSegment(sketch, "E516", {"start": v(-57.85, 59.32) * mm, "end": v(-55.06, 57.24) * mm});
            skLineSegment(sketch, "E517", {"start": v(-55.06, 57.24) * mm, "end": v(-54.63, 57.58) * mm});
            skLineSegment(sketch, "E518", {"start": v(77.31, -39.88) * mm, "end": v(76.52, -43.19) * mm});
            skLineSegment(sketch, "E519", {"start": v(76.52, -43.19) * mm, "end": v(75.65, -44.83) * mm});
            skLineSegment(sketch, "E520", {"start": v(75.65, -44.83) * mm, "end": v(74.5, -46.15) * mm});
            skLineSegment(sketch, "E521", {"start": v(74.5, -46.15) * mm, "end": v(70.7, -48.32) * mm});
            skLineSegment(sketch, "E522", {"start": v(70.7, -48.32) * mm, "end": v(67.2, -49.39) * mm});
            skLineSegment(sketch, "E523", {"start": v(67.2, -49.39) * mm, "end": v(63.97, -49.86) * mm});
            skLineSegment(sketch, "E524", {"start": v(63.97, -49.86) * mm, "end": v(59.5, -50.08) * mm});
            skLineSegment(sketch, "E525", {"start": v(59.5, -50.08) * mm, "end": v(55.3, -49.48) * mm});
            skLineSegment(sketch, "E526", {"start": v(55.3, -49.48) * mm, "end": v(49.96, -47.88) * mm});
            skLineSegment(sketch, "E527", {"start": v(49.96, -47.88) * mm, "end": v(47.53, -46.73) * mm});
            skLineSegment(sketch, "E528", {"start": v(47.53, -46.73) * mm, "end": v(45.22, -45.2) * mm});
            skLineSegment(sketch, "E529", {"start": v(45.22, -45.2) * mm, "end": v(43.29, -43.65) * mm});
            skLineSegment(sketch, "E530", {"start": v(43.29, -43.65) * mm, "end": v(41.92, -42.15) * mm});
            skLineSegment(sketch, "E531", {"start": v(41.92, -42.15) * mm, "end": v(40.34, -39.71) * mm});
            skLineSegment(sketch, "E532", {"start": v(40.34, -39.71) * mm, "end": v(38.56, -35.87) * mm});
            skLineSegment(sketch, "E533", {"start": v(38.56, -35.87) * mm, "end": v(40.02, -36.3) * mm});
            skLineSegment(sketch, "E534", {"start": v(40.02, -36.3) * mm, "end": v(42.52, -37.14) * mm});
            skLineSegment(sketch, "E535", {"start": v(42.52, -37.14) * mm, "end": v(48.29, -37.64) * mm});
            skLineSegment(sketch, "E536", {"start": v(48.29, -37.64) * mm, "end": v(52.66, -36.73) * mm});
            skLineSegment(sketch, "E537", {"start": v(52.66, -36.73) * mm, "end": v(56.4, -34.74) * mm});
            skLineSegment(sketch, "E538", {"start": v(56.4, -34.74) * mm, "end": v(57.9, -33.86) * mm});
            skLineSegment(sketch, "E539", {"start": v(57.9, -33.86) * mm, "end": v(59.52, -33.22) * mm});
            skLineSegment(sketch, "E540", {"start": v(59.52, -33.22) * mm, "end": v(62.66, -32.37) * mm});
            skLineSegment(sketch, "E541", {"start": v(62.66, -32.37) * mm, "end": v(65.88, -32.23) * mm});
            skLineSegment(sketch, "E542", {"start": v(65.88, -32.23) * mm, "end": v(70.14, -32.85) * mm});
            skLineSegment(sketch, "E543", {"start": v(70.14, -32.85) * mm, "end": v(71.96, -33.52) * mm});
            skLineSegment(sketch, "E544", {"start": v(71.96, -33.52) * mm, "end": v(74.1, -34.96) * mm});
            skLineSegment(sketch, "E545", {"start": v(74.1, -34.96) * mm, "end": v(75.96, -36.91) * mm});
            skLineSegment(sketch, "E546", {"start": v(75.96, -36.91) * mm, "end": v(77.22, -38.89) * mm});
            skLineSegment(sketch, "E547", {"start": v(77.22, -38.89) * mm, "end": v(82.52, -40.35) * mm});
            skLineSegment(sketch, "E548", {"start": v(82.52, -40.35) * mm, "end": v(86.52, -41.64) * mm});
            skLineSegment(sketch, "E549", {"start": v(86.52, -41.64) * mm, "end": v(86.7, -44.6) * mm});
            skLineSegment(sketch, "E550", {"start": v(86.7, -44.6) * mm, "end": v(85.42, -43.04) * mm});
            skLineSegment(sketch, "E551", {"start": v(85.42, -43.04) * mm, "end": v(83.03, -41.5) * mm});
            skLineSegment(sketch, "E552", {"start": v(83.03, -41.5) * mm, "end": v(80.12, -40.34) * mm});
            skLineSegment(sketch, "E553", {"start": v(80.12, -40.34) * mm, "end": v(77.31, -39.88) * mm});
            skLineSegment(sketch, "E554", {"start": v(76, -39.4) * mm, "end": v(70.67, -38.45) * mm});
            skLineSegment(sketch, "E555", {"start": v(70.67, -38.45) * mm, "end": v(66.5, -38.34) * mm});
            skLineSegment(sketch, "E556", {"start": v(66.5, -38.34) * mm, "end": v(64.07, -38.68) * mm});
            skLineSegment(sketch, "E557", {"start": v(64.07, -38.68) * mm, "end": v(59.33, -40.39) * mm});
            skLineSegment(sketch, "E558", {"start": v(59.33, -40.39) * mm, "end": v(56.83, -41.56) * mm});
            skLineSegment(sketch, "E559", {"start": v(56.83, -41.56) * mm, "end": v(53.08, -42.43) * mm});
            skLineSegment(sketch, "E560", {"start": v(53.08, -42.43) * mm, "end": v(50.12, -42.56) * mm});
            skLineSegment(sketch, "E561", {"start": v(50.12, -42.56) * mm, "end": v(47.07, -41.87) * mm});
            skLineSegment(sketch, "E562", {"start": v(47.07, -41.87) * mm, "end": v(44.88, -40.98) * mm});
            skLineSegment(sketch, "E563", {"start": v(44.88, -40.98) * mm, "end": v(42.25, -39.45) * mm});
            skLineSegment(sketch, "E564", {"start": v(42.25, -39.45) * mm, "end": v(39.7, -37.23) * mm});
            skLineSegment(sketch, "E565", {"start": v(39.7, -37.23) * mm, "end": v(44.09, -40.19) * mm});
            skLineSegment(sketch, "E566", {"start": v(44.09, -40.19) * mm, "end": v(49.16, -41.96) * mm});
            skLineSegment(sketch, "E567", {"start": v(49.16, -41.96) * mm, "end": v(51.43, -42.07) * mm});
            skLineSegment(sketch, "E568", {"start": v(51.43, -42.07) * mm, "end": v(53.83, -41.74) * mm});
            skLineSegment(sketch, "E569", {"start": v(53.83, -41.74) * mm, "end": v(58.74, -40.1) * mm});
            skLineSegment(sketch, "E570", {"start": v(58.74, -40.1) * mm, "end": v(62.55, -38.47) * mm});
            skLineSegment(sketch, "E571", {"start": v(62.55, -38.47) * mm, "end": v(64.46, -37.9) * mm});
            skLineSegment(sketch, "E572", {"start": v(64.46, -37.9) * mm, "end": v(66.18, -37.73) * mm});
            skLineSegment(sketch, "E573", {"start": v(66.18, -37.73) * mm, "end": v(68.7, -37.61) * mm});
            skLineSegment(sketch, "E574", {"start": v(68.7, -37.61) * mm, "end": v(71.19, -37.83) * mm});
            skLineSegment(sketch, "E575", {"start": v(71.19, -37.83) * mm, "end": v(76.07, -38.65) * mm});
            skLineSegment(sketch, "E576", {"start": v(76.07, -38.65) * mm, "end": v(76, -39.4) * mm});
            skLineSegment(sketch, "E577", {"start": v(74.44, -39.61) * mm, "end": v(74.91, -39.68) * mm});
            skLineSegment(sketch, "E578", {"start": v(74.91, -39.68) * mm, "end": v(74.91, -40.72) * mm});
            skLineSegment(sketch, "E579", {"start": v(74.91, -40.72) * mm, "end": v(74.6, -41.82) * mm});
            skLineSegment(sketch, "E580", {"start": v(74.6, -41.82) * mm, "end": v(73.69, -43.75) * mm});
            skLineSegment(sketch, "E581", {"start": v(73.69, -43.75) * mm, "end": v(72.22, -45.33) * mm});
            skLineSegment(sketch, "E582", {"start": v(72.22, -45.33) * mm, "end": v(67.8, -48.83) * mm});
            skLineSegment(sketch, "E583", {"start": v(67.8, -48.83) * mm, "end": v(72.6, -44.49) * mm});
            skLineSegment(sketch, "E584", {"start": v(72.6, -44.49) * mm, "end": v(73.93, -42.38) * mm});
            skLineSegment(sketch, "E585", {"start": v(73.93, -42.38) * mm, "end": v(74.44, -39.61) * mm});
            skLineSegment(sketch, "E586", {"start": v(69.78, -38.86) * mm, "end": v(70.17, -38.84) * mm});
            skLineSegment(sketch, "E587", {"start": v(70.17, -38.84) * mm, "end": v(70.23, -38.77) * mm});
            skLineSegment(sketch, "E588", {"start": v(70.23, -38.77) * mm, "end": v(70.2, -39.9) * mm});
            skLineSegment(sketch, "E589", {"start": v(70.2, -39.9) * mm, "end": v(69.84, -41.08) * mm});
            skLineSegment(sketch, "E590", {"start": v(69.84, -41.08) * mm, "end": v(68.59, -43.2) * mm});
            skLineSegment(sketch, "E591", {"start": v(68.59, -43.2) * mm, "end": v(66.8, -44.94) * mm});
            skLineSegment(sketch, "E592", {"start": v(66.8, -44.94) * mm, "end": v(61.95, -48.66) * mm});
            skLineSegment(sketch, "E593", {"start": v(61.95, -48.66) * mm, "end": v(67.4, -44.01) * mm});
            skLineSegment(sketch, "E594", {"start": v(67.4, -44.01) * mm, "end": v(69.15, -41.6) * mm});
            skLineSegment(sketch, "E595", {"start": v(69.15, -41.6) * mm, "end": v(69.78, -38.86) * mm});
            skLineSegment(sketch, "E596", {"start": v(64, -39.24) * mm, "end": v(64.5, -39.08) * mm});
            skLineSegment(sketch, "E597", {"start": v(64.5, -39.08) * mm, "end": v(64.23, -40.71) * mm});
            skLineSegment(sketch, "E598", {"start": v(64.23, -40.71) * mm, "end": v(63.64, -42.21) * mm});
            skLineSegment(sketch, "E599", {"start": v(63.64, -42.21) * mm, "end": v(62.34, -43.77) * mm});
            skLineSegment(sketch, "E600", {"start": v(62.34, -43.77) * mm, "end": v(60.44, -45.37) * mm});
            skLineSegment(sketch, "E601", {"start": v(60.44, -45.37) * mm, "end": v(59.53, -45.91) * mm});
            skLineSegment(sketch, "E602", {"start": v(59.53, -45.91) * mm, "end": v(54.79, -48.55) * mm});
            skLineSegment(sketch, "E603", {"start": v(54.79, -48.55) * mm, "end": v(60.05, -45.21) * mm});
            skLineSegment(sketch, "E604", {"start": v(60.05, -45.21) * mm, "end": v(61.75, -43.8) * mm});
            skLineSegment(sketch, "E605", {"start": v(61.75, -43.8) * mm, "end": v(63.44, -41.69) * mm});
            skLineSegment(sketch, "E606", {"start": v(63.44, -41.69) * mm, "end": v(63.89, -40.38) * mm});
            skLineSegment(sketch, "E607", {"start": v(63.89, -40.38) * mm, "end": v(64, -39.24) * mm});
            skLineSegment(sketch, "E608", {"start": v(57.56, -41.7) * mm, "end": v(58.19, -41.5) * mm});
            skLineSegment(sketch, "E609", {"start": v(58.19, -41.5) * mm, "end": v(57.05, -43.48) * mm});
            skLineSegment(sketch, "E610", {"start": v(57.05, -43.48) * mm, "end": v(55.22, -44.97) * mm});
            skLineSegment(sketch, "E611", {"start": v(55.22, -44.97) * mm, "end": v(53.62, -45.6) * mm});
            skLineSegment(sketch, "E612", {"start": v(53.62, -45.6) * mm, "end": v(51.05, -46.03) * mm});
            skLineSegment(sketch, "E613", {"start": v(51.05, -46.03) * mm, "end": v(47.79, -46.06) * mm});
            skLineSegment(sketch, "E614", {"start": v(47.79, -46.06) * mm, "end": v(53.3, -45.44) * mm});
            skLineSegment(sketch, "E615", {"start": v(53.3, -45.44) * mm, "end": v(54.78, -44.87) * mm});
            skLineSegment(sketch, "E616", {"start": v(54.78, -44.87) * mm, "end": v(55.9, -44.07) * mm});
            skLineSegment(sketch, "E617", {"start": v(55.9, -44.07) * mm, "end": v(57.56, -41.7) * mm});
            skLineSegment(sketch, "E618", {"start": v(73.7, -37.8) * mm, "end": v(74.16, -37.78) * mm});
            skLineSegment(sketch, "E619", {"start": v(74.16, -37.78) * mm, "end": v(73.4, -36.23) * mm});
            skLineSegment(sketch, "E620", {"start": v(73.4, -36.23) * mm, "end": v(72.39, -35.15) * mm});
            skLineSegment(sketch, "E621", {"start": v(72.39, -35.15) * mm, "end": v(71.08, -34.4) * mm});
            skLineSegment(sketch, "E622", {"start": v(71.08, -34.4) * mm, "end": v(67.4, -33.03) * mm});
            skLineSegment(sketch, "E623", {"start": v(67.4, -33.03) * mm, "end": v(71.5, -34.9) * mm});
            skLineSegment(sketch, "E624", {"start": v(71.5, -34.9) * mm, "end": v(72.84, -36) * mm});
            skLineSegment(sketch, "E625", {"start": v(72.84, -36) * mm, "end": v(73.7, -37.8) * mm});
            skLineSegment(sketch, "E626", {"start": v(68.57, -37.34) * mm, "end": v(69, -37.36) * mm});
            skLineSegment(sketch, "E627", {"start": v(69, -37.36) * mm, "end": v(68.26, -35.77) * mm});
            skLineSegment(sketch, "E628", {"start": v(68.26, -35.77) * mm, "end": v(67.24, -34.69) * mm});
            skLineSegment(sketch, "E629", {"start": v(67.24, -34.69) * mm, "end": v(65.93, -33.95) * mm});
            skLineSegment(sketch, "E630", {"start": v(65.93, -33.95) * mm, "end": v(62.26, -32.57) * mm});
            skLineSegment(sketch, "E631", {"start": v(62.26, -32.57) * mm, "end": v(66.36, -34.43) * mm});
            skLineSegment(sketch, "E632", {"start": v(66.36, -34.43) * mm, "end": v(67.7, -35.55) * mm});
            skLineSegment(sketch, "E633", {"start": v(67.7, -35.55) * mm, "end": v(68.57, -37.34) * mm});
            skLineSegment(sketch, "E634", {"start": v(64.18, -37.66) * mm, "end": v(64.65, -37.58) * mm});
            skLineSegment(sketch, "E635", {"start": v(64.65, -37.58) * mm, "end": v(63.73, -36.35) * mm});
            skLineSegment(sketch, "E636", {"start": v(63.73, -36.35) * mm, "end": v(62.56, -35.44) * mm});
            skLineSegment(sketch, "E637", {"start": v(62.56, -35.44) * mm, "end": v(61.15, -34.91) * mm});
            skLineSegment(sketch, "E638", {"start": v(61.15, -34.91) * mm, "end": v(57.31, -34.13) * mm});
            skLineSegment(sketch, "E639", {"start": v(57.31, -34.13) * mm, "end": v(61.65, -35.32) * mm});
            skLineSegment(sketch, "E640", {"start": v(61.65, -35.32) * mm, "end": v(63.14, -36.21) * mm});
            skLineSegment(sketch, "E641", {"start": v(63.14, -36.21) * mm, "end": v(64.18, -37.66) * mm});
            skLineSegment(sketch, "E642", {"start": v(60.25, -39) * mm, "end": v(60.64, -38.83) * mm});
            skLineSegment(sketch, "E643", {"start": v(60.64, -38.83) * mm, "end": v(59.69, -37.83) * mm});
            skLineSegment(sketch, "E644", {"start": v(59.69, -37.83) * mm, "end": v(58.37, -37.23) * mm});
            skLineSegment(sketch, "E645", {"start": v(58.37, -37.23) * mm, "end": v(56.9, -37.05) * mm});
            skLineSegment(sketch, "E646", {"start": v(56.9, -37.05) * mm, "end": v(53.37, -36.9) * mm});
            skLineSegment(sketch, "E647", {"start": v(53.37, -36.9) * mm, "end": v(55.5, -37.2) * mm});
            skLineSegment(sketch, "E648", {"start": v(55.5, -37.2) * mm, "end": v(57.5, -37.3) * mm});
            skLineSegment(sketch, "E649", {"start": v(57.5, -37.3) * mm, "end": v(59.13, -37.86) * mm});
            skLineSegment(sketch, "E650", {"start": v(59.13, -37.86) * mm, "end": v(60.25, -39) * mm});
            skLineSegment(sketch, "E651", {"start": v(54.93, -41.34) * mm, "end": v(55.3, -41.26) * mm});
            skLineSegment(sketch, "E652", {"start": v(55.3, -41.26) * mm, "end": v(54.74, -40.16) * mm});
            skLineSegment(sketch, "E653", {"start": v(54.74, -40.16) * mm, "end": v(53.89, -39.25) * mm});
            skLineSegment(sketch, "E654", {"start": v(53.89, -39.25) * mm, "end": v(52.79, -38.63) * mm});
            skLineSegment(sketch, "E655", {"start": v(52.79, -38.63) * mm, "end": v(49.95, -37.67) * mm});
            skLineSegment(sketch, "E656", {"start": v(49.95, -37.67) * mm, "end": v(51.5, -38.4) * mm});
            skLineSegment(sketch, "E657", {"start": v(51.5, -38.4) * mm, "end": v(53.15, -39.03) * mm});
            skLineSegment(sketch, "E658", {"start": v(53.15, -39.03) * mm, "end": v(54.27, -39.97) * mm});
            skLineSegment(sketch, "E659", {"start": v(54.27, -39.97) * mm, "end": v(54.93, -41.34) * mm});
            skLineSegment(sketch, "E660", {"start": v(86.63, -28.88) * mm, "end": v(89.9, -27.92) * mm});
            skLineSegment(sketch, "E661", {"start": v(89.9, -27.92) * mm, "end": v(91.5, -26.98) * mm});
            skLineSegment(sketch, "E662", {"start": v(91.5, -26.98) * mm, "end": v(92.75, -25.77) * mm});
            skLineSegment(sketch, "E663", {"start": v(92.75, -25.77) * mm, "end": v(94.74, -21.86) * mm});
            skLineSegment(sketch, "E664", {"start": v(94.74, -21.86) * mm, "end": v(95.63, -18.31) * mm});
            skLineSegment(sketch, "E665", {"start": v(95.63, -18.31) * mm, "end": v(95.95, -15.06) * mm});
            skLineSegment(sketch, "E666", {"start": v(95.95, -15.06) * mm, "end": v(95.95, -10.6) * mm});
            skLineSegment(sketch, "E667", {"start": v(95.95, -10.6) * mm, "end": v(95.15, -6.43) * mm});
            skLineSegment(sketch, "E668", {"start": v(95.15, -6.43) * mm, "end": v(93.3, -1.17) * mm});
            skLineSegment(sketch, "E669", {"start": v(93.3, -1.17) * mm, "end": v(92.02, 1.2) * mm});
            skLineSegment(sketch, "E670", {"start": v(92.02, 1.2) * mm, "end": v(90.4, 3.43) * mm});
            skLineSegment(sketch, "E671", {"start": v(90.4, 3.43) * mm, "end": v(88.74, 5.29) * mm});
            skLineSegment(sketch, "E672", {"start": v(88.74, 5.29) * mm, "end": v(87.18, 6.58) * mm});
            skLineSegment(sketch, "E673", {"start": v(87.18, 6.58) * mm, "end": v(84.67, 8.05) * mm});
            skLineSegment(sketch, "E674", {"start": v(84.67, 8.05) * mm, "end": v(80.74, 9.63) * mm});
            skLineSegment(sketch, "E675", {"start": v(80.74, 9.63) * mm, "end": v(81.24, 8.2) * mm});
            skLineSegment(sketch, "E676", {"start": v(81.24, 8.2) * mm, "end": v(82.2, 5.74) * mm});
            skLineSegment(sketch, "E677", {"start": v(82.2, 5.74) * mm, "end": v(82.98, 0) * mm});
            skLineSegment(sketch, "E678", {"start": v(82.98, 0) * mm, "end": v(82.29, -4.41) * mm});
            skLineSegment(sketch, "E679", {"start": v(82.29, -4.41) * mm, "end": v(80.48, -8.24) * mm});
            skLineSegment(sketch, "E680", {"start": v(80.48, -8.24) * mm, "end": v(79.67, -9.78) * mm});
            skLineSegment(sketch, "E681", {"start": v(79.67, -9.78) * mm, "end": v(79.11, -11.43) * mm});
            skLineSegment(sketch, "E682", {"start": v(79.11, -11.43) * mm, "end": v(78.42, -14.6) * mm});
            skLineSegment(sketch, "E683", {"start": v(78.42, -14.6) * mm, "end": v(78.43, -17.83) * mm});
            skLineSegment(sketch, "E684", {"start": v(78.43, -17.83) * mm, "end": v(79.26, -22.05) * mm});
            skLineSegment(sketch, "E685", {"start": v(79.26, -22.05) * mm, "end": v(80.01, -23.83) * mm});
            skLineSegment(sketch, "E686", {"start": v(80.01, -23.83) * mm, "end": v(81.55, -25.9) * mm});
            skLineSegment(sketch, "E687", {"start": v(81.55, -25.9) * mm, "end": v(83.6, -27.67) * mm});
            skLineSegment(sketch, "E688", {"start": v(83.6, -27.67) * mm, "end": v(85.63, -28.84) * mm});
            skLineSegment(sketch, "E689", {"start": v(85.63, -28.84) * mm, "end": v(87.35, -34.05) * mm});
            skLineSegment(sketch, "E690", {"start": v(87.35, -34.05) * mm, "end": v(88.84, -38) * mm});
            skLineSegment(sketch, "E691", {"start": v(88.84, -38) * mm, "end": v(91.8, -38.02) * mm});
            skLineSegment(sketch, "E692", {"start": v(91.8, -38.02) * mm, "end": v(90.17, -36.82) * mm});
            skLineSegment(sketch, "E693", {"start": v(90.17, -36.82) * mm, "end": v(88.53, -34.5) * mm});
            skLineSegment(sketch, "E694", {"start": v(88.53, -34.5) * mm, "end": v(87.23, -31.66) * mm});
            skLineSegment(sketch, "E695", {"start": v(87.23, -31.66) * mm, "end": v(86.63, -28.88) * mm});
            skLineSegment(sketch, "E696", {"start": v(86.63, -28.88) * mm, "end": v(86.63, -28.88) * mm});
            skLineSegment(sketch, "E697", {"start": v(86.1, -27.6) * mm, "end": v(84.88, -22.3) * mm});
            skLineSegment(sketch, "E698", {"start": v(84.88, -22.3) * mm, "end": v(84.56, -18.15) * mm});
            skLineSegment(sketch, "E699", {"start": v(84.56, -18.15) * mm, "end": v(84.8, -15.7) * mm});
            skLineSegment(sketch, "E700", {"start": v(84.8, -15.7) * mm, "end": v(86.26, -10.9) * mm});
            skLineSegment(sketch, "E701", {"start": v(86.26, -10.9) * mm, "end": v(87.31, -8.33) * mm});
            skLineSegment(sketch, "E702", {"start": v(87.31, -8.33) * mm, "end": v(88, -4.55) * mm});
            skLineSegment(sketch, "E703", {"start": v(88, -4.55) * mm, "end": v(87.98, -1.6) * mm});
            skLineSegment(sketch, "E704", {"start": v(87.98, -1.6) * mm, "end": v(87.15, 1.43) * mm});
            skLineSegment(sketch, "E705", {"start": v(87.15, 1.43) * mm, "end": v(86.15, 3.57) * mm});
            skLineSegment(sketch, "E706", {"start": v(86.15, 3.57) * mm, "end": v(84.5, 6.12) * mm});
            skLineSegment(sketch, "E707", {"start": v(84.5, 6.12) * mm, "end": v(82.16, 8.57) * mm});
            skLineSegment(sketch, "E708", {"start": v(82.16, 8.57) * mm, "end": v(85.33, 4.32) * mm});
            skLineSegment(sketch, "E709", {"start": v(85.33, 4.32) * mm, "end": v(87.34, -0.66) * mm});
            skLineSegment(sketch, "E710", {"start": v(87.34, -0.66) * mm, "end": v(87.56, -2.92) * mm});
            skLineSegment(sketch, "E711", {"start": v(87.56, -2.92) * mm, "end": v(87.35, -5.33) * mm});
            skLineSegment(sketch, "E712", {"start": v(87.35, -5.33) * mm, "end": v(85.95, -10.32) * mm});
            skLineSegment(sketch, "E713", {"start": v(85.95, -10.32) * mm, "end": v(84.5, -14.2) * mm});
            skLineSegment(sketch, "E714", {"start": v(84.5, -14.2) * mm, "end": v(84.03, -16.14) * mm});
            skLineSegment(sketch, "E715", {"start": v(84.03, -16.14) * mm, "end": v(83.94, -17.86) * mm});
            skLineSegment(sketch, "E716", {"start": v(83.94, -17.86) * mm, "end": v(83.94, -20.4) * mm});
            skLineSegment(sketch, "E717", {"start": v(83.94, -20.4) * mm, "end": v(84.28, -22.86) * mm});
            skLineSegment(sketch, "E718", {"start": v(84.28, -22.86) * mm, "end": v(85.34, -27.7) * mm});
            skLineSegment(sketch, "E719", {"start": v(85.34, -27.7) * mm, "end": v(86.1, -27.6) * mm});
            skLineSegment(sketch, "E720", {"start": v(86.22, -26.02) * mm, "end": v(86.31, -26.5) * mm});
            skLineSegment(sketch, "E721", {"start": v(86.31, -26.5) * mm, "end": v(87.35, -26.44) * mm});
            skLineSegment(sketch, "E722", {"start": v(87.35, -26.44) * mm, "end": v(88.44, -26.07) * mm});
            skLineSegment(sketch, "E723", {"start": v(88.44, -26.07) * mm, "end": v(90.32, -25.07) * mm});
            skLineSegment(sketch, "E724", {"start": v(90.32, -25.07) * mm, "end": v(91.83, -23.53) * mm});
            skLineSegment(sketch, "E725", {"start": v(91.83, -23.53) * mm, "end": v(95.1, -18.95) * mm});
            skLineSegment(sketch, "E726", {"start": v(95.1, -18.95) * mm, "end": v(91, -23.94) * mm});
            skLineSegment(sketch, "E727", {"start": v(91, -23.94) * mm, "end": v(88.96, -25.38) * mm});
            skLineSegment(sketch, "E728", {"start": v(88.96, -25.38) * mm, "end": v(86.22, -26.02) * mm});
            skLineSegment(sketch, "E729", {"start": v(85.24, -21.4) * mm, "end": v(85.24, -21.8) * mm});
            skLineSegment(sketch, "E730", {"start": v(85.24, -21.8) * mm, "end": v(85.18, -21.86) * mm});
            skLineSegment(sketch, "E731", {"start": v(85.18, -21.86) * mm, "end": v(86.3, -21.77) * mm});
            skLineSegment(sketch, "E732", {"start": v(86.3, -21.77) * mm, "end": v(87.46, -21.36) * mm});
            skLineSegment(sketch, "E733", {"start": v(87.46, -21.36) * mm, "end": v(89.51, -20) * mm});
            skLineSegment(sketch, "E734", {"start": v(89.51, -20) * mm, "end": v(91.17, -18.12) * mm});
            skLineSegment(sketch, "E735", {"start": v(91.17, -18.12) * mm, "end": v(94.66, -13.1) * mm});
            skLineSegment(sketch, "E736", {"start": v(94.66, -13.1) * mm, "end": v(90.27, -18.77) * mm});
            skLineSegment(sketch, "E737", {"start": v(90.27, -18.77) * mm, "end": v(87.95, -20.64) * mm});
            skLineSegment(sketch, "E738", {"start": v(87.95, -20.64) * mm, "end": v(85.24, -21.4) * mm});
            skLineSegment(sketch, "E739", {"start": v(85.35, -15.6) * mm, "end": v(85.2, -16.12) * mm});
            skLineSegment(sketch, "E740", {"start": v(85.2, -16.12) * mm, "end": v(86.82, -15.77) * mm});
            skLineSegment(sketch, "E741", {"start": v(86.82, -15.77) * mm, "end": v(88.3, -15.11) * mm});
            skLineSegment(sketch, "E742", {"start": v(88.3, -15.11) * mm, "end": v(89.78, -13.73) * mm});
            skLineSegment(sketch, "E743", {"start": v(89.78, -13.73) * mm, "end": v(91.3, -11.75) * mm});
            skLineSegment(sketch, "E744", {"start": v(91.3, -11.75) * mm, "end": v(91.79, -10.82) * mm});
            skLineSegment(sketch, "E745", {"start": v(91.79, -10.82) * mm, "end": v(94.2, -5.96) * mm});
            skLineSegment(sketch, "E746", {"start": v(94.2, -5.96) * mm, "end": v(91.12, -11.38) * mm});
            skLineSegment(sketch, "E747", {"start": v(91.12, -11.38) * mm, "end": v(89.78, -13.14) * mm});
            skLineSegment(sketch, "E748", {"start": v(89.78, -13.14) * mm, "end": v(87.76, -14.94) * mm});
            skLineSegment(sketch, "E749", {"start": v(87.76, -14.94) * mm, "end": v(86.48, -15.45) * mm});
            skLineSegment(sketch, "E750", {"start": v(86.48, -15.45) * mm, "end": v(85.35, -15.6) * mm});
            skLineSegment(sketch, "E751", {"start": v(87.5, -9.06) * mm, "end": v(87.3, -9.7) * mm});
            skLineSegment(sketch, "E752", {"start": v(87.3, -9.7) * mm, "end": v(89.24, -8.46) * mm});
            skLineSegment(sketch, "E753", {"start": v(89.24, -8.46) * mm, "end": v(90.64, -6.57) * mm});
            skLineSegment(sketch, "E754", {"start": v(90.64, -6.57) * mm, "end": v(91.19, -4.93) * mm});
            skLineSegment(sketch, "E755", {"start": v(91.19, -4.93) * mm, "end": v(91.5, -2.35) * mm});
            skLineSegment(sketch, "E756", {"start": v(91.5, -2.35) * mm, "end": v(91.36, 0.91) * mm});
            skLineSegment(sketch, "E757", {"start": v(91.36, 0.91) * mm, "end": v(91.02, -4.63) * mm});
            skLineSegment(sketch, "E758", {"start": v(91.02, -4.63) * mm, "end": v(90.52, -6.13) * mm});
            skLineSegment(sketch, "E759", {"start": v(90.52, -6.13) * mm, "end": v(89.78, -7.28) * mm});
            skLineSegment(sketch, "E760", {"start": v(89.78, -7.28) * mm, "end": v(87.5, -9.06) * mm});
            skLineSegment(sketch, "E761", {"start": v(84.38, -25.37) * mm, "end": v(84.37, -25.83) * mm});
            skLineSegment(sketch, "E762", {"start": v(84.37, -25.83) * mm, "end": v(82.8, -25.15) * mm});
            skLineSegment(sketch, "E763", {"start": v(82.8, -25.15) * mm, "end": v(81.66, -24.19) * mm});
            skLineSegment(sketch, "E764", {"start": v(81.66, -24.19) * mm, "end": v(80.86, -22.91) * mm});
            skLineSegment(sketch, "E765", {"start": v(80.86, -22.91) * mm, "end": v(79.3, -19.31) * mm});
            skLineSegment(sketch, "E766", {"start": v(79.3, -19.31) * mm, "end": v(81.36, -23.32) * mm});
            skLineSegment(sketch, "E767", {"start": v(81.36, -23.32) * mm, "end": v(82.54, -24.6) * mm});
            skLineSegment(sketch, "E768", {"start": v(82.54, -24.6) * mm, "end": v(84.38, -25.37) * mm});
            skLineSegment(sketch, "E769", {"start": v(84.38, -25.37) * mm, "end": v(84.38, -25.37) * mm});
            skLineSegment(sketch, "E770", {"start": v(83.67, -20.27) * mm, "end": v(83.7, -20.7) * mm});
            skLineSegment(sketch, "E771", {"start": v(83.7, -20.7) * mm, "end": v(82.09, -20.03) * mm});
            skLineSegment(sketch, "E772", {"start": v(82.09, -20.03) * mm, "end": v(80.95, -19.07) * mm});
            skLineSegment(sketch, "E773", {"start": v(80.95, -19.07) * mm, "end": v(80.15, -17.8) * mm});
            skLineSegment(sketch, "E774", {"start": v(80.15, -17.8) * mm, "end": v(78.6, -14.2) * mm});
            skLineSegment(sketch, "E775", {"start": v(78.6, -14.2) * mm, "end": v(80.66, -18.2) * mm});
            skLineSegment(sketch, "E776", {"start": v(80.66, -18.2) * mm, "end": v(81.83, -19.48) * mm});
            skLineSegment(sketch, "E777", {"start": v(81.83, -19.48) * mm, "end": v(83.67, -20.27) * mm});
            skLineSegment(sketch, "E778", {"start": v(83.77, -15.87) * mm, "end": v(83.71, -16.34) * mm});
            skLineSegment(sketch, "E779", {"start": v(83.71, -16.34) * mm, "end": v(82.44, -15.48) * mm});
            skLineSegment(sketch, "E780", {"start": v(82.44, -15.48) * mm, "end": v(81.47, -14.36) * mm});
            skLineSegment(sketch, "E781", {"start": v(81.47, -14.36) * mm, "end": v(80.88, -12.98) * mm});
            skLineSegment(sketch, "E782", {"start": v(80.88, -12.98) * mm, "end": v(79.91, -9.18) * mm});
            skLineSegment(sketch, "E783", {"start": v(79.91, -9.18) * mm, "end": v(81.32, -13.45) * mm});
            skLineSegment(sketch, "E784", {"start": v(81.32, -13.45) * mm, "end": v(82.28, -14.9) * mm});
            skLineSegment(sketch, "E785", {"start": v(82.28, -14.9) * mm, "end": v(83.77, -15.87) * mm});
            skLineSegment(sketch, "E786", {"start": v(84.93, -11.88) * mm, "end": v(84.77, -12.27) * mm});
            skLineSegment(sketch, "E787", {"start": v(84.77, -12.27) * mm, "end": v(83.72, -11.37) * mm});
            skLineSegment(sketch, "E788", {"start": v(83.72, -11.37) * mm, "end": v(83.06, -10.08) * mm});
            skLineSegment(sketch, "E789", {"start": v(83.06, -10.08) * mm, "end": v(82.81, -8.64) * mm});
            skLineSegment(sketch, "E790", {"start": v(82.81, -8.64) * mm, "end": v(82.48, -5.11) * mm});
            skLineSegment(sketch, "E791", {"start": v(82.48, -5.11) * mm, "end": v(82.9, -7.21) * mm});
            skLineSegment(sketch, "E792", {"start": v(82.9, -7.21) * mm, "end": v(83.08, -9.22) * mm});
            skLineSegment(sketch, "E793", {"start": v(83.08, -9.22) * mm, "end": v(83.73, -10.82) * mm});
            skLineSegment(sketch, "E794", {"start": v(83.73, -10.82) * mm, "end": v(84.93, -11.88) * mm});
            skLineSegment(sketch, "E795", {"start": v(87, -6.45) * mm, "end": v(86.94, -6.81) * mm});
            skLineSegment(sketch, "E796", {"start": v(86.94, -6.81) * mm, "end": v(85.81, -6.32) * mm});
            skLineSegment(sketch, "E797", {"start": v(85.81, -6.32) * mm, "end": v(84.86, -5.51) * mm});
            skLineSegment(sketch, "E798", {"start": v(84.86, -5.51) * mm, "end": v(84.19, -4.44) * mm});
            skLineSegment(sketch, "E799", {"start": v(84.19, -4.44) * mm, "end": v(83.1, -1.66) * mm});
            skLineSegment(sketch, "E800", {"start": v(83.1, -1.66) * mm, "end": v(83.9, -3.18) * mm});
            skLineSegment(sketch, "E801", {"start": v(83.9, -3.18) * mm, "end": v(84.61, -4.78) * mm});
            skLineSegment(sketch, "E802", {"start": v(84.61, -4.78) * mm, "end": v(85.6, -5.85) * mm});
            skLineSegment(sketch, "E803", {"start": v(85.6, -5.85) * mm, "end": v(87, -6.45) * mm});
            skLineSegment(sketch, "E804", {"start": v(75.75, 57.9) * mm, "end": v(73.87, 55.59) * mm});
            skLineSegment(sketch, "E805", {"start": v(73.87, 55.59) * mm, "end": v(71.67, 53.58) * mm});
            skLineSegment(sketch, "E806", {"start": v(71.67, 53.58) * mm, "end": v(69.2, 51.9) * mm});
            skLineSegment(sketch, "E807", {"start": v(69.2, 51.9) * mm, "end": v(66.5, 50.62) * mm});
            skLineSegment(sketch, "E808", {"start": v(66.5, 50.62) * mm, "end": v(63.24, 49.65) * mm});
            skLineSegment(sketch, "E809", {"start": v(63.24, 49.65) * mm, "end": v(59.84, 49.17) * mm});
            skLineSegment(sketch, "E810", {"start": v(59.84, 49.17) * mm, "end": v(56.39, 49.12) * mm});
            skLineSegment(sketch, "E811", {"start": v(56.39, 49.12) * mm, "end": v(52.93, 49.44) * mm});
            skLineSegment(sketch, "E812", {"start": v(52.93, 49.44) * mm, "end": v(46.13, 50.87) * mm});
            skLineSegment(sketch, "E813", {"start": v(46.13, 50.87) * mm, "end": v(39.4, 52.87) * mm});
            skLineSegment(sketch, "E814", {"start": v(39.4, 52.87) * mm, "end": v(32.61, 54.87) * mm});
            skLineSegment(sketch, "E815", {"start": v(32.61, 54.87) * mm, "end": v(25.64, 56.26) * mm});
            skLineSegment(sketch, "E816", {"start": v(25.64, 56.26) * mm, "end": v(22.07, 56.53) * mm});
            skLineSegment(sketch, "E817", {"start": v(22.07, 56.53) * mm, "end": v(18.47, 56.4) * mm});
            skLineSegment(sketch, "E818", {"start": v(18.47, 56.4) * mm, "end": v(14.93, 55.83) * mm});
            skLineSegment(sketch, "E819", {"start": v(14.93, 55.83) * mm, "end": v(11.5, 54.71) * mm});
            skLineSegment(sketch, "E820", {"start": v(11.5, 54.71) * mm, "end": v(8.2, 52.96) * mm});
            skLineSegment(sketch, "E821", {"start": v(8.2, 52.96) * mm, "end": v(5.25, 50.64) * mm});
            skLineSegment(sketch, "E822", {"start": v(5.25, 50.64) * mm, "end": v(6.06, 49.78) * mm});
            skLineSegment(sketch, "E823", {"start": v(6.06, 49.78) * mm, "end": v(8.84, 51.97) * mm});
            skLineSegment(sketch, "E824", {"start": v(8.84, 51.97) * mm, "end": v(11.96, 53.62) * mm});
            skLineSegment(sketch, "E825", {"start": v(11.96, 53.62) * mm, "end": v(15.2, 54.68) * mm});
            skLineSegment(sketch, "E826", {"start": v(15.2, 54.68) * mm, "end": v(18.59, 55.23) * mm});
            skLineSegment(sketch, "E827", {"start": v(18.59, 55.23) * mm, "end": v(22.04, 55.34) * mm});
            skLineSegment(sketch, "E828", {"start": v(22.04, 55.34) * mm, "end": v(25.5, 55.08) * mm});
            skLineSegment(sketch, "E829", {"start": v(25.5, 55.08) * mm, "end": v(32.31, 53.72) * mm});
            skLineSegment(sketch, "E830", {"start": v(32.31, 53.72) * mm, "end": v(39.04, 51.74) * mm});
            skLineSegment(sketch, "E831", {"start": v(39.04, 51.74) * mm, "end": v(45.82, 49.72) * mm});
            skLineSegment(sketch, "E832", {"start": v(45.82, 49.72) * mm, "end": v(52.77, 48.26) * mm});
            skLineSegment(sketch, "E833", {"start": v(52.77, 48.26) * mm, "end": v(56.34, 47.94) * mm});
            skLineSegment(sketch, "E834", {"start": v(56.34, 47.94) * mm, "end": v(59.93, 48) * mm});
            skLineSegment(sketch, "E835", {"start": v(59.93, 48) * mm, "end": v(63.49, 48.5) * mm});
            skLineSegment(sketch, "E836", {"start": v(63.49, 48.5) * mm, "end": v(66.94, 49.52) * mm});
            skLineSegment(sketch, "E837", {"start": v(66.94, 49.52) * mm, "end": v(69.78, 50.88) * mm});
            skLineSegment(sketch, "E838", {"start": v(69.78, 50.88) * mm, "end": v(72.4, 52.64) * mm});
            skLineSegment(sketch, "E839", {"start": v(72.4, 52.64) * mm, "end": v(74.73, 54.77) * mm});
            skLineSegment(sketch, "E840", {"start": v(74.73, 54.77) * mm, "end": v(76.72, 57.22) * mm});
            skLineSegment(sketch, "E841", {"start": v(76.72, 57.22) * mm, "end": v(75.75, 57.9) * mm});
            skLineSegment(sketch, "E842", {"start": v(-40.38, -40.06) * mm, "end": v(-39.06, -40.27) * mm});
            skLineSegment(sketch, "E843", {"start": v(-39.06, -40.27) * mm, "end": v(-37.9, -40.87) * mm});
            skLineSegment(sketch, "E844", {"start": v(-37.9, -40.87) * mm, "end": v(-36.75, -42.32) * mm});
            skLineSegment(sketch, "E845", {"start": v(-36.75, -42.32) * mm, "end": v(-36.3, -44.08) * mm});
            skLineSegment(sketch, "E846", {"start": v(-36.3, -44.08) * mm, "end": v(-36.52, -45.31) * mm});
            skLineSegment(sketch, "E847", {"start": v(-36.52, -45.31) * mm, "end": v(-37.17, -46.4) * mm});
            skLineSegment(sketch, "E848", {"start": v(-37.17, -46.4) * mm, "end": v(-39.07, -47.66) * mm});
            skLineSegment(sketch, "E849", {"start": v(-39.07, -47.66) * mm, "end": v(-40.52, -47.9) * mm});
            skLineSegment(sketch, "E850", {"start": v(-40.52, -47.9) * mm, "end": v(-42.35, -47.5) * mm});
            skLineSegment(sketch, "E851", {"start": v(-42.35, -47.5) * mm, "end": v(-44, -46.04) * mm});
            skLineSegment(sketch, "E852", {"start": v(-44, -46.04) * mm, "end": v(-44.57, -43.98) * mm});
            skLineSegment(sketch, "E853", {"start": v(-44.57, -43.98) * mm, "end": v(-44.39, -42.74) * mm});
            skLineSegment(sketch, "E854", {"start": v(-44.39, -42.74) * mm, "end": v(-43.83, -41.66) * mm});
            skLineSegment(sketch, "E855", {"start": v(-43.83, -41.66) * mm, "end": v(-42.05, -40.35) * mm});
            skLineSegment(sketch, "E856", {"start": v(-42.05, -40.35) * mm, "end": v(-40.38, -40.06) * mm});
            skLineSegment(sketch, "E857", {"start": v(-40.9, -41.65) * mm, "end": v(-41.64, -42.06) * mm});
            skLineSegment(sketch, "E858", {"start": v(-41.64, -42.06) * mm, "end": v(-41.85, -42.8) * mm});
            skLineSegment(sketch, "E859", {"start": v(-41.85, -42.8) * mm, "end": v(-41.6, -44.24) * mm});
            skLineSegment(sketch, "E860", {"start": v(-41.6, -44.24) * mm, "end": v(-40.96, -45.69) * mm});
            skLineSegment(sketch, "E861", {"start": v(-40.96, -45.69) * mm, "end": v(-40.54, -46.12) * mm});
            skLineSegment(sketch, "E862", {"start": v(-40.54, -46.12) * mm, "end": v(-40.03, -46.28) * mm});
            skLineSegment(sketch, "E863", {"start": v(-40.03, -46.28) * mm, "end": v(-39.35, -45.96) * mm});
            skLineSegment(sketch, "E864", {"start": v(-39.35, -45.96) * mm, "end": v(-39.1, -45.14) * mm});
            skLineSegment(sketch, "E865", {"start": v(-39.1, -45.14) * mm, "end": v(-39.3, -43.7) * mm});
            skLineSegment(sketch, "E866", {"start": v(-39.3, -43.7) * mm, "end": v(-39.87, -42.38) * mm});
            skLineSegment(sketch, "E867", {"start": v(-39.87, -42.38) * mm, "end": v(-40.35, -41.85) * mm});
            skLineSegment(sketch, "E868", {"start": v(-40.35, -41.85) * mm, "end": v(-40.9, -41.65) * mm});
            skLineSegment(sketch, "E869", {"start": v(-32.56, -43.7) * mm, "end": v(-32.56, -45.56) * mm});
            skLineSegment(sketch, "E870", {"start": v(-32.56, -45.56) * mm, "end": v(-32.4, -46.1) * mm});
            skLineSegment(sketch, "E871", {"start": v(-32.4, -46.1) * mm, "end": v(-31.98, -46.3) * mm});
            skLineSegment(sketch, "E872", {"start": v(-31.98, -46.3) * mm, "end": v(-31.4, -46.11) * mm});
            skLineSegment(sketch, "E873", {"start": v(-31.4, -46.11) * mm, "end": v(-31.24, -46.06) * mm});
            skLineSegment(sketch, "E874", {"start": v(-31.24, -46.06) * mm, "end": v(-31, -46.22) * mm});
            skLineSegment(sketch, "E875", {"start": v(-31, -46.22) * mm, "end": v(-30.9, -46.57) * mm});
            skLineSegment(sketch, "E876", {"start": v(-30.9, -46.57) * mm, "end": v(-31.27, -47.22) * mm});
            skLineSegment(sketch, "E877", {"start": v(-31.27, -47.22) * mm, "end": v(-33.16, -47.9) * mm});
            skLineSegment(sketch, "E878", {"start": v(-33.16, -47.9) * mm, "end": v(-34.58, -47.4) * mm});
            skLineSegment(sketch, "E879", {"start": v(-34.58, -47.4) * mm, "end": v(-35.11, -46.08) * mm});
            skLineSegment(sketch, "E880", {"start": v(-35.11, -46.08) * mm, "end": v(-35.11, -43.53) * mm});
            skLineSegment(sketch, "E881", {"start": v(-35.11, -43.53) * mm, "end": v(-35.15, -43.38) * mm});
            skLineSegment(sketch, "E882", {"start": v(-35.15, -43.38) * mm, "end": v(-35.3, -43.34) * mm});
            skLineSegment(sketch, "E883", {"start": v(-35.3, -43.34) * mm, "end": v(-35.87, -43.34) * mm});
            skLineSegment(sketch, "E884", {"start": v(-35.87, -43.34) * mm, "end": v(-36.07, -43.3) * mm});
            skLineSegment(sketch, "E885", {"start": v(-36.07, -43.3) * mm, "end": v(-36.12, -43.05) * mm});
            skLineSegment(sketch, "E886", {"start": v(-36.12, -43.05) * mm, "end": v(-36.12, -42.8) * mm});
            skLineSegment(sketch, "E887", {"start": v(-36.12, -42.8) * mm, "end": v(-36, -42.56) * mm});
            skLineSegment(sketch, "E888", {"start": v(-36, -42.56) * mm, "end": v(-33.47, -40.97) * mm});
            skLineSegment(sketch, "E889", {"start": v(-33.47, -40.97) * mm, "end": v(-33.23, -40.92) * mm});
            skLineSegment(sketch, "E890", {"start": v(-33.23, -40.92) * mm, "end": v(-32.79, -40.92) * mm});
            skLineSegment(sketch, "E891", {"start": v(-32.79, -40.92) * mm, "end": v(-32.6, -41) * mm});
            skLineSegment(sketch, "E892", {"start": v(-32.6, -41) * mm, "end": v(-32.56, -41.24) * mm});
            skLineSegment(sketch, "E893", {"start": v(-32.56, -41.24) * mm, "end": v(-32.56, -41.98) * mm});
            skLineSegment(sketch, "E894", {"start": v(-32.56, -41.98) * mm, "end": v(-32.5, -42.2) * mm});
            skLineSegment(sketch, "E895", {"start": v(-32.5, -42.2) * mm, "end": v(-32.28, -42.25) * mm});
            skLineSegment(sketch, "E896", {"start": v(-32.28, -42.25) * mm, "end": v(-31.26, -42.25) * mm});
            skLineSegment(sketch, "E897", {"start": v(-31.26, -42.25) * mm, "end": v(-31, -42.32) * mm});
            skLineSegment(sketch, "E898", {"start": v(-31, -42.32) * mm, "end": v(-30.94, -42.64) * mm});
            skLineSegment(sketch, "E899", {"start": v(-30.94, -42.64) * mm, "end": v(-30.94, -42.96) * mm});
            skLineSegment(sketch, "E900", {"start": v(-30.94, -42.96) * mm, "end": v(-31.01, -43.33) * mm});
            skLineSegment(sketch, "E901", {"start": v(-31.01, -43.33) * mm, "end": v(-31.3, -43.43) * mm});
            skLineSegment(sketch, "E902", {"start": v(-31.3, -43.43) * mm, "end": v(-32.3, -43.43) * mm});
            skLineSegment(sketch, "E903", {"start": v(-32.3, -43.43) * mm, "end": v(-32.5, -43.49) * mm});
            skLineSegment(sketch, "E904", {"start": v(-32.5, -43.49) * mm, "end": v(-32.56, -43.7) * mm});
            skLineSegment(sketch, "E905", {"start": v(-27.33, -43.7) * mm, "end": v(-27.33, -45.56) * mm});
            skLineSegment(sketch, "E906", {"start": v(-27.33, -45.56) * mm, "end": v(-27.17, -46.1) * mm});
            skLineSegment(sketch, "E907", {"start": v(-27.17, -46.1) * mm, "end": v(-26.75, -46.3) * mm});
            skLineSegment(sketch, "E908", {"start": v(-26.75, -46.3) * mm, "end": v(-26.18, -46.11) * mm});
            skLineSegment(sketch, "E909", {"start": v(-26.18, -46.11) * mm, "end": v(-26.02, -46.06) * mm});
            skLineSegment(sketch, "E910", {"start": v(-26.02, -46.06) * mm, "end": v(-25.78, -46.22) * mm});
            skLineSegment(sketch, "E911", {"start": v(-25.78, -46.22) * mm, "end": v(-25.67, -46.57) * mm});
            skLineSegment(sketch, "E912", {"start": v(-25.67, -46.57) * mm, "end": v(-26.04, -47.22) * mm});
            skLineSegment(sketch, "E913", {"start": v(-26.04, -47.22) * mm, "end": v(-27.94, -47.9) * mm});
            skLineSegment(sketch, "E914", {"start": v(-27.94, -47.9) * mm, "end": v(-29.35, -47.4) * mm});
            skLineSegment(sketch, "E915", {"start": v(-29.35, -47.4) * mm, "end": v(-29.89, -46.08) * mm});
            skLineSegment(sketch, "E916", {"start": v(-29.89, -46.08) * mm, "end": v(-29.89, -43.53) * mm});
            skLineSegment(sketch, "E917", {"start": v(-29.89, -43.53) * mm, "end": v(-29.92, -43.38) * mm});
            skLineSegment(sketch, "E918", {"start": v(-29.92, -43.38) * mm, "end": v(-30.08, -43.34) * mm});
            skLineSegment(sketch, "E919", {"start": v(-30.08, -43.34) * mm, "end": v(-30.64, -43.34) * mm});
            skLineSegment(sketch, "E920", {"start": v(-30.64, -43.34) * mm, "end": v(-30.85, -43.3) * mm});
            skLineSegment(sketch, "E921", {"start": v(-30.85, -43.3) * mm, "end": v(-30.9, -43.05) * mm});
            skLineSegment(sketch, "E922", {"start": v(-30.9, -43.05) * mm, "end": v(-30.9, -42.8) * mm});
            skLineSegment(sketch, "E923", {"start": v(-30.9, -42.8) * mm, "end": v(-30.76, -42.56) * mm});
            skLineSegment(sketch, "E924", {"start": v(-30.76, -42.56) * mm, "end": v(-28.24, -40.97) * mm});
            skLineSegment(sketch, "E925", {"start": v(-28.24, -40.97) * mm, "end": v(-28, -40.92) * mm});
            skLineSegment(sketch, "E926", {"start": v(-28, -40.92) * mm, "end": v(-27.56, -40.92) * mm});
            skLineSegment(sketch, "E927", {"start": v(-27.56, -40.92) * mm, "end": v(-27.38, -41) * mm});
            skLineSegment(sketch, "E928", {"start": v(-27.38, -41) * mm, "end": v(-27.33, -41.24) * mm});
            skLineSegment(sketch, "E929", {"start": v(-27.33, -41.24) * mm, "end": v(-27.33, -41.98) * mm});
            skLineSegment(sketch, "E930", {"start": v(-27.33, -41.98) * mm, "end": v(-27.28, -42.2) * mm});
            skLineSegment(sketch, "E931", {"start": v(-27.28, -42.2) * mm, "end": v(-27.05, -42.25) * mm});
            skLineSegment(sketch, "E932", {"start": v(-27.05, -42.25) * mm, "end": v(-26.04, -42.25) * mm});
            skLineSegment(sketch, "E933", {"start": v(-26.04, -42.25) * mm, "end": v(-25.77, -42.32) * mm});
            skLineSegment(sketch, "E934", {"start": v(-25.77, -42.32) * mm, "end": v(-25.7, -42.64) * mm});
            skLineSegment(sketch, "E935", {"start": v(-25.7, -42.64) * mm, "end": v(-25.7, -42.96) * mm});
            skLineSegment(sketch, "E936", {"start": v(-25.7, -42.96) * mm, "end": v(-25.79, -43.33) * mm});
            skLineSegment(sketch, "E937", {"start": v(-25.79, -43.33) * mm, "end": v(-26.07, -43.43) * mm});
            skLineSegment(sketch, "E938", {"start": v(-26.07, -43.43) * mm, "end": v(-27.07, -43.43) * mm});
            skLineSegment(sketch, "E939", {"start": v(-27.07, -43.43) * mm, "end": v(-27.28, -43.49) * mm});
            skLineSegment(sketch, "E940", {"start": v(-27.28, -43.49) * mm, "end": v(-27.33, -43.7) * mm});
            skLineSegment(sketch, "E941", {"start": v(-22.02, -42.25) * mm, "end": v(-20.25, -42.77) * mm});
            skLineSegment(sketch, "E942", {"start": v(-20.25, -42.77) * mm, "end": v(-19.38, -43.75) * mm});
            skLineSegment(sketch, "E943", {"start": v(-19.38, -43.75) * mm, "end": v(-19.03, -45.06) * mm});
            skLineSegment(sketch, "E944", {"start": v(-19.03, -45.06) * mm, "end": v(-19.3, -46.16) * mm});
            skLineSegment(sketch, "E945", {"start": v(-19.3, -46.16) * mm, "end": v(-20.13, -47.1) * mm});
            skLineSegment(sketch, "E946", {"start": v(-20.13, -47.1) * mm, "end": v(-21.25, -47.7) * mm});
            skLineSegment(sketch, "E947", {"start": v(-21.25, -47.7) * mm, "end": v(-22.53, -47.9) * mm});
            skLineSegment(sketch, "E948", {"start": v(-22.53, -47.9) * mm, "end": v(-23.72, -47.7) * mm});
            skLineSegment(sketch, "E949", {"start": v(-23.72, -47.7) * mm, "end": v(-24.66, -47.14) * mm});
            skLineSegment(sketch, "E950", {"start": v(-24.66, -47.14) * mm, "end": v(-25.26, -46.3) * mm});
            skLineSegment(sketch, "E951", {"start": v(-25.26, -46.3) * mm, "end": v(-25.46, -45.25) * mm});
            skLineSegment(sketch, "E952", {"start": v(-25.46, -45.25) * mm, "end": v(-25.21, -44.06) * mm});
            skLineSegment(sketch, "E953", {"start": v(-25.21, -44.06) * mm, "end": v(-24.49, -43.12) * mm});
            skLineSegment(sketch, "E954", {"start": v(-24.49, -43.12) * mm, "end": v(-23.36, -42.46) * mm});
            skLineSegment(sketch, "E955", {"start": v(-23.36, -42.46) * mm, "end": v(-22.02, -42.25) * mm});
            skLineSegment(sketch, "E956", {"start": v(-22.46, -43.52) * mm, "end": v(-22.85, -43.7) * mm});
            skLineSegment(sketch, "E957", {"start": v(-22.85, -43.7) * mm, "end": v(-23, -44.18) * mm});
            skLineSegment(sketch, "E958", {"start": v(-23, -44.18) * mm, "end": v(-22.88, -45.08) * mm});
            skLineSegment(sketch, "E959", {"start": v(-22.88, -45.08) * mm, "end": v(-22.58, -46.09) * mm});
            skLineSegment(sketch, "E960", {"start": v(-22.58, -46.09) * mm, "end": v(-22.02, -46.54) * mm});
            skLineSegment(sketch, "E961", {"start": v(-22.02, -46.54) * mm, "end": v(-21.65, -46.39) * mm});
            skLineSegment(sketch, "E962", {"start": v(-21.65, -46.39) * mm, "end": v(-21.53, -45.92) * mm});
            skLineSegment(sketch, "E963", {"start": v(-21.53, -45.92) * mm, "end": v(-21.66, -44.87) * mm});
            skLineSegment(sketch, "E964", {"start": v(-21.66, -44.87) * mm, "end": v(-21.96, -43.9) * mm});
            skLineSegment(sketch, "E965", {"start": v(-21.96, -43.9) * mm, "end": v(-22.46, -43.52) * mm});
            skLineSegment(sketch, "E966", {"start": v(-15.63, -40.55) * mm, "end": v(-15.7, -42.7) * mm});
            skLineSegment(sketch, "E967", {"start": v(-15.7, -42.7) * mm, "end": v(-15.7, -42.82) * mm});
            skLineSegment(sketch, "E968", {"start": v(-15.7, -42.82) * mm, "end": v(-15.63, -42.93) * mm});
            skLineSegment(sketch, "E969", {"start": v(-15.63, -42.93) * mm, "end": v(-15.41, -42.78) * mm});
            skLineSegment(sketch, "E970", {"start": v(-15.41, -42.78) * mm, "end": v(-14, -42.25) * mm});
            skLineSegment(sketch, "E971", {"start": v(-14, -42.25) * mm, "end": v(-12.63, -42.8) * mm});
            skLineSegment(sketch, "E972", {"start": v(-12.63, -42.8) * mm, "end": v(-12.08, -43.62) * mm});
            skLineSegment(sketch, "E973", {"start": v(-12.08, -43.62) * mm, "end": v(-11.9, -44.63) * mm});
            skLineSegment(sketch, "E974", {"start": v(-11.9, -44.63) * mm, "end": v(-12.2, -46.08) * mm});
            skLineSegment(sketch, "E975", {"start": v(-12.2, -46.08) * mm, "end": v(-13.09, -47.2) * mm});
            skLineSegment(sketch, "E976", {"start": v(-13.09, -47.2) * mm, "end": v(-15.1, -47.9) * mm});
            skLineSegment(sketch, "E977", {"start": v(-15.1, -47.9) * mm, "end": v(-16.14, -47.74) * mm});
            skLineSegment(sketch, "E978", {"start": v(-16.14, -47.74) * mm, "end": v(-17.14, -47.25) * mm});
            skLineSegment(sketch, "E979", {"start": v(-17.14, -47.25) * mm, "end": v(-17.28, -47.2) * mm});
            skLineSegment(sketch, "E980", {"start": v(-17.28, -47.2) * mm, "end": v(-17.62, -47.3) * mm});
            skLineSegment(sketch, "E981", {"start": v(-17.62, -47.3) * mm, "end": v(-17.95, -47.36) * mm});
            skLineSegment(sketch, "E982", {"start": v(-17.95, -47.36) * mm, "end": v(-18.3, -47.14) * mm});
            skLineSegment(sketch, "E983", {"start": v(-18.3, -47.14) * mm, "end": v(-18.27, -46.97) * mm});
            skLineSegment(sketch, "E984", {"start": v(-18.27, -46.97) * mm, "end": v(-18.12, -46.08) * mm});
            skLineSegment(sketch, "E985", {"start": v(-18.12, -46.08) * mm, "end": v(-18.08, -44.4) * mm});
            skLineSegment(sketch, "E986", {"start": v(-18.08, -44.4) * mm, "end": v(-18.08, -42.89) * mm});
            skLineSegment(sketch, "E987", {"start": v(-18.08, -42.89) * mm, "end": v(-18.13, -42.18) * mm});
            skLineSegment(sketch, "E988", {"start": v(-18.13, -42.18) * mm, "end": v(-18.37, -41.95) * mm});
            skLineSegment(sketch, "E989", {"start": v(-18.37, -41.95) * mm, "end": v(-18.77, -41.71) * mm});
            skLineSegment(sketch, "E990", {"start": v(-18.77, -41.71) * mm, "end": v(-18.88, -41.4) * mm});
            skLineSegment(sketch, "E991", {"start": v(-18.88, -41.4) * mm, "end": v(-18.1, -40.69) * mm});
            skLineSegment(sketch, "E992", {"start": v(-18.1, -40.69) * mm, "end": v(-17.02, -40.36) * mm});
            skLineSegment(sketch, "E993", {"start": v(-17.02, -40.36) * mm, "end": v(-15.92, -40.22) * mm});
            skLineSegment(sketch, "E994", {"start": v(-15.92, -40.22) * mm, "end": v(-15.63, -40.55) * mm});
            skLineSegment(sketch, "E995", {"start": v(-15.16, -43.91) * mm, "end": v(-15.59, -44.12) * mm});
            skLineSegment(sketch, "E996", {"start": v(-15.59, -44.12) * mm, "end": v(-15.7, -44.74) * mm});
            skLineSegment(sketch, "E997", {"start": v(-15.7, -44.74) * mm, "end": v(-15.6, -46.5) * mm});
            skLineSegment(sketch, "E998", {"start": v(-15.6, -46.5) * mm, "end": v(-15.14, -46.91) * mm});
            skLineSegment(sketch, "E999", {"start": v(-15.14, -46.91) * mm, "end": v(-14.53, -46.57) * mm});
            skLineSegment(sketch, "E1000", {"start": v(-14.53, -46.57) * mm, "end": v(-14.32, -45.58) * mm});
            skLineSegment(sketch, "E1001", {"start": v(-14.32, -45.58) * mm, "end": v(-14.67, -44.18) * mm});
            skLineSegment(sketch, "E1002", {"start": v(-14.67, -44.18) * mm, "end": v(-15.16, -43.91) * mm});
            skLineSegment(sketch, "E1003", {"start": v(-8.91, -42.29) * mm, "end": v(-8.56, -42.37) * mm});
            skLineSegment(sketch, "E1004", {"start": v(-8.56, -42.37) * mm, "end": v(-8.45, -42.9) * mm});
            skLineSegment(sketch, "E1005", {"start": v(-8.45, -42.9) * mm, "end": v(-8.28, -43.14) * mm});
            skLineSegment(sketch, "E1006", {"start": v(-8.28, -43.14) * mm, "end": v(-8.07, -42.98) * mm});
            skLineSegment(sketch, "E1007", {"start": v(-8.07, -42.98) * mm, "end": v(-6.91, -42.3) * mm});
            skLineSegment(sketch, "E1008", {"start": v(-6.91, -42.3) * mm, "end": v(-6.1, -42.62) * mm});
            skLineSegment(sketch, "E1009", {"start": v(-6.1, -42.62) * mm, "end": v(-5.84, -43.03) * mm});
            skLineSegment(sketch, "E1010", {"start": v(-5.84, -43.03) * mm, "end": v(-5.74, -43.5) * mm});
            skLineSegment(sketch, "E1011", {"start": v(-5.74, -43.5) * mm, "end": v(-5.86, -44.04) * mm});
            skLineSegment(sketch, "E1012", {"start": v(-5.86, -44.04) * mm, "end": v(-6.17, -44.5) * mm});
            skLineSegment(sketch, "E1013", {"start": v(-6.17, -44.5) * mm, "end": v(-7.04, -44.83) * mm});
            skLineSegment(sketch, "E1014", {"start": v(-7.04, -44.83) * mm, "end": v(-7.51, -44.73) * mm});
            skLineSegment(sketch, "E1015", {"start": v(-7.51, -44.73) * mm, "end": v(-8.01, -44.33) * mm});
            skLineSegment(sketch, "E1016", {"start": v(-8.01, -44.33) * mm, "end": v(-8.23, -44.2) * mm});
            skLineSegment(sketch, "E1017", {"start": v(-8.23, -44.2) * mm, "end": v(-8.43, -44.39) * mm});
            skLineSegment(sketch, "E1018", {"start": v(-8.43, -44.39) * mm, "end": v(-8.47, -45.11) * mm});
            skLineSegment(sketch, "E1019", {"start": v(-8.47, -45.11) * mm, "end": v(-8.41, -46.25) * mm});
            skLineSegment(sketch, "E1020", {"start": v(-8.41, -46.25) * mm, "end": v(-8.3, -46.48) * mm});
            skLineSegment(sketch, "E1021", {"start": v(-8.3, -46.48) * mm, "end": v(-8.01, -46.6) * mm});
            skLineSegment(sketch, "E1022", {"start": v(-8.01, -46.6) * mm, "end": v(-7.51, -47.13) * mm});
            skLineSegment(sketch, "E1023", {"start": v(-7.51, -47.13) * mm, "end": v(-7.67, -47.52) * mm});
            skLineSegment(sketch, "E1024", {"start": v(-7.67, -47.52) * mm, "end": v(-8.1, -47.74) * mm});
            skLineSegment(sketch, "E1025", {"start": v(-8.1, -47.74) * mm, "end": v(-9.65, -47.85) * mm});
            skLineSegment(sketch, "E1026", {"start": v(-9.65, -47.85) * mm, "end": v(-11.14, -47.68) * mm});
            skLineSegment(sketch, "E1027", {"start": v(-11.14, -47.68) * mm, "end": v(-11.59, -47.15) * mm});
            skLineSegment(sketch, "E1028", {"start": v(-11.59, -47.15) * mm, "end": v(-11.26, -46.63) * mm});
            skLineSegment(sketch, "E1029", {"start": v(-11.26, -46.63) * mm, "end": v(-11.04, -46.45) * mm});
            skLineSegment(sketch, "E1030", {"start": v(-11.04, -46.45) * mm, "end": v(-10.95, -46.21) * mm});
            skLineSegment(sketch, "E1031", {"start": v(-10.95, -46.21) * mm, "end": v(-10.87, -44.35) * mm});
            skLineSegment(sketch, "E1032", {"start": v(-10.87, -44.35) * mm, "end": v(-10.92, -44) * mm});
            skLineSegment(sketch, "E1033", {"start": v(-10.92, -44) * mm, "end": v(-11.14, -43.82) * mm});
            skLineSegment(sketch, "E1034", {"start": v(-11.14, -43.82) * mm, "end": v(-11.53, -43.38) * mm});
            skLineSegment(sketch, "E1035", {"start": v(-11.53, -43.38) * mm, "end": v(-11.26, -42.93) * mm});
            skLineSegment(sketch, "E1036", {"start": v(-11.26, -42.93) * mm, "end": v(-10.36, -42.54) * mm});
            skLineSegment(sketch, "E1037", {"start": v(-10.36, -42.54) * mm, "end": v(-8.91, -42.29) * mm});
            skLineSegment(sketch, "E1038", {"start": v(-0.45, -45.27) * mm, "end": v(-3.04, -45.27) * mm});
            skLineSegment(sketch, "E1039", {"start": v(-3.04, -45.27) * mm, "end": v(-3.21, -45.42) * mm});
            skLineSegment(sketch, "E1040", {"start": v(-3.21, -45.42) * mm, "end": v(-2.83, -46.1) * mm});
            skLineSegment(sketch, "E1041", {"start": v(-2.83, -46.1) * mm, "end": v(-2, -46.41) * mm});
            skLineSegment(sketch, "E1042", {"start": v(-2, -46.41) * mm, "end": v(-1.4, -46.31) * mm});
            skLineSegment(sketch, "E1043", {"start": v(-1.4, -46.31) * mm, "end": v(-0.87, -46.06) * mm});
            skLineSegment(sketch, "E1044", {"start": v(-0.87, -46.06) * mm, "end": v(-0.57, -45.93) * mm});
            skLineSegment(sketch, "E1045", {"start": v(-0.57, -45.93) * mm, "end": v(-0.3, -46.1) * mm});
            skLineSegment(sketch, "E1046", {"start": v(-0.3, -46.1) * mm, "end": v(-0.16, -46.47) * mm});
            skLineSegment(sketch, "E1047", {"start": v(-0.16, -46.47) * mm, "end": v(-0.65, -47.24) * mm});
            skLineSegment(sketch, "E1048", {"start": v(-0.65, -47.24) * mm, "end": v(-2.67, -47.9) * mm});
            skLineSegment(sketch, "E1049", {"start": v(-2.67, -47.9) * mm, "end": v(-4.61, -47.22) * mm});
            skLineSegment(sketch, "E1050", {"start": v(-4.61, -47.22) * mm, "end": v(-5.24, -46.42) * mm});
            skLineSegment(sketch, "E1051", {"start": v(-5.24, -46.42) * mm, "end": v(-5.57, -45.1) * mm});
            skLineSegment(sketch, "E1052", {"start": v(-5.57, -45.1) * mm, "end": v(-5, -43.44) * mm});
            skLineSegment(sketch, "E1053", {"start": v(-5, -43.44) * mm, "end": v(-3.77, -42.49) * mm});
            skLineSegment(sketch, "E1054", {"start": v(-3.77, -42.49) * mm, "end": v(-2.55, -42.25) * mm});
            skLineSegment(sketch, "E1055", {"start": v(-2.55, -42.25) * mm, "end": v(-0.77, -42.85) * mm});
            skLineSegment(sketch, "E1056", {"start": v(-0.77, -42.85) * mm, "end": v(-0.18, -43.55) * mm});
            skLineSegment(sketch, "E1057", {"start": v(-0.18, -43.55) * mm, "end": v(0.08, -44.46) * mm});
            skLineSegment(sketch, "E1058", {"start": v(0.08, -44.46) * mm, "end": v(-0.07, -45.05) * mm});
            skLineSegment(sketch, "E1059", {"start": v(-0.07, -45.05) * mm, "end": v(-0.45, -45.27) * mm});
            skLineSegment(sketch, "E1060", {"start": v(-2.9, -44.24) * mm, "end": v(-2.34, -44.24) * mm});
            skLineSegment(sketch, "E1061", {"start": v(-2.34, -44.24) * mm, "end": v(-2, -43.92) * mm});
            skLineSegment(sketch, "E1062", {"start": v(-2, -43.92) * mm, "end": v(-2.16, -43.43) * mm});
            skLineSegment(sketch, "E1063", {"start": v(-2.16, -43.43) * mm, "end": v(-2.6, -43.24) * mm});
            skLineSegment(sketch, "E1064", {"start": v(-2.6, -43.24) * mm, "end": v(-3.1, -43.49) * mm});
            skLineSegment(sketch, "E1065", {"start": v(-3.1, -43.49) * mm, "end": v(-3.26, -43.94) * mm});
            skLineSegment(sketch, "E1066", {"start": v(-3.26, -43.94) * mm, "end": v(-3.18, -44.18) * mm});
            skLineSegment(sketch, "E1067", {"start": v(-3.18, -44.18) * mm, "end": v(-2.9, -44.24) * mm});
            skLineSegment(sketch, "E1068", {"start": v(7.42, -47.74) * mm, "end": v(3.67, -47.74) * mm});
            skLineSegment(sketch, "E1069", {"start": v(3.67, -47.74) * mm, "end": v(3.17, -47.46) * mm});
            skLineSegment(sketch, "E1070", {"start": v(3.17, -47.46) * mm, "end": v(3.28, -47.2) * mm});
            skLineSegment(sketch, "E1071", {"start": v(3.28, -47.2) * mm, "end": v(3.96, -46.53) * mm});
            skLineSegment(sketch, "E1072", {"start": v(3.96, -46.53) * mm, "end": v(5.53, -44.66) * mm});
            skLineSegment(sketch, "E1073", {"start": v(5.53, -44.66) * mm, "end": v(5.8, -43.9) * mm});
            skLineSegment(sketch, "E1074", {"start": v(5.8, -43.9) * mm, "end": v(5.64, -43.47) * mm});
            skLineSegment(sketch, "E1075", {"start": v(5.64, -43.47) * mm, "end": v(5.2, -43.3) * mm});
            skLineSegment(sketch, "E1076", {"start": v(5.2, -43.3) * mm, "end": v(4.82, -43.37) * mm});
            skLineSegment(sketch, "E1077", {"start": v(4.82, -43.37) * mm, "end": v(4.24, -43.82) * mm});
            skLineSegment(sketch, "E1078", {"start": v(4.24, -43.82) * mm, "end": v(3.92, -43.92) * mm});
            skLineSegment(sketch, "E1079", {"start": v(3.92, -43.92) * mm, "end": v(3.44, -43.72) * mm});
            skLineSegment(sketch, "E1080", {"start": v(3.44, -43.72) * mm, "end": v(3.22, -43.28) * mm});
            skLineSegment(sketch, "E1081", {"start": v(3.22, -43.28) * mm, "end": v(3.42, -42.8) * mm});
            skLineSegment(sketch, "E1082", {"start": v(3.42, -42.8) * mm, "end": v(3.95, -42.27) * mm});
            skLineSegment(sketch, "E1083", {"start": v(3.95, -42.27) * mm, "end": v(5.2, -41.63) * mm});
            skLineSegment(sketch, "E1084", {"start": v(5.2, -41.63) * mm, "end": v(6.59, -41.42) * mm});
            skLineSegment(sketch, "E1085", {"start": v(6.59, -41.42) * mm, "end": v(8.41, -41.84) * mm});
            skLineSegment(sketch, "E1086", {"start": v(8.41, -41.84) * mm, "end": v(8.93, -42.38) * mm});
            skLineSegment(sketch, "E1087", {"start": v(8.93, -42.38) * mm, "end": v(9.13, -43.11) * mm});
            skLineSegment(sketch, "E1088", {"start": v(9.13, -43.11) * mm, "end": v(8.8, -44.12) * mm});
            skLineSegment(sketch, "E1089", {"start": v(8.8, -44.12) * mm, "end": v(7.8, -45.2) * mm});
            skLineSegment(sketch, "E1090", {"start": v(7.8, -45.2) * mm, "end": v(7.32, -45.8) * mm});
            skLineSegment(sketch, "E1091", {"start": v(7.32, -45.8) * mm, "end": v(7.47, -46.07) * mm});
            skLineSegment(sketch, "E1092", {"start": v(7.47, -46.07) * mm, "end": v(7.81, -46.17) * mm});
            skLineSegment(sketch, "E1093", {"start": v(7.81, -46.17) * mm, "end": v(8.68, -45.8) * mm});
            skLineSegment(sketch, "E1094", {"start": v(8.68, -45.8) * mm, "end": v(8.93, -45.57) * mm});
            skLineSegment(sketch, "E1095", {"start": v(8.93, -45.57) * mm, "end": v(9.11, -45.53) * mm});
            skLineSegment(sketch, "E1096", {"start": v(9.11, -45.53) * mm, "end": v(9.47, -45.74) * mm});
            skLineSegment(sketch, "E1097", {"start": v(9.47, -45.74) * mm, "end": v(9.6, -46.36) * mm});
            skLineSegment(sketch, "E1098", {"start": v(9.6, -46.36) * mm, "end": v(9.44, -47.2) * mm});
            skLineSegment(sketch, "E1099", {"start": v(9.44, -47.2) * mm, "end": v(9.01, -47.93) * mm});
            skLineSegment(sketch, "E1100", {"start": v(9.01, -47.93) * mm, "end": v(8.38, -48.26) * mm});
            skLineSegment(sketch, "E1101", {"start": v(8.38, -48.26) * mm, "end": v(8.16, -48.2) * mm});
            skLineSegment(sketch, "E1102", {"start": v(8.16, -48.2) * mm, "end": v(7.97, -47.99) * mm});
            skLineSegment(sketch, "E1103", {"start": v(7.97, -47.99) * mm, "end": v(7.78, -47.79) * mm});
            skLineSegment(sketch, "E1104", {"start": v(7.78, -47.79) * mm, "end": v(7.42, -47.74) * mm});
            skLineSegment(sketch, "E1105", {"start": v(13.11, -41.38) * mm, "end": v(14.57, -41.75) * mm});
            skLineSegment(sketch, "E1106", {"start": v(14.57, -41.75) * mm, "end": v(15.98, -43.23) * mm});
            skLineSegment(sketch, "E1107", {"start": v(15.98, -43.23) * mm, "end": v(16.33, -44.76) * mm});
            skLineSegment(sketch, "E1108", {"start": v(16.33, -44.76) * mm, "end": v(16.05, -46.1) * mm});
            skLineSegment(sketch, "E1109", {"start": v(16.05, -46.1) * mm, "end": v(15.2, -47.17) * mm});
            skLineSegment(sketch, "E1110", {"start": v(15.2, -47.17) * mm, "end": v(13.23, -47.9) * mm});
            skLineSegment(sketch, "E1111", {"start": v(13.23, -47.9) * mm, "end": v(12.1, -47.7) * mm});
            skLineSegment(sketch, "E1112", {"start": v(12.1, -47.7) * mm, "end": v(11.14, -47.1) * mm});
            skLineSegment(sketch, "E1113", {"start": v(11.14, -47.1) * mm, "end": v(10.38, -46) * mm});
            skLineSegment(sketch, "E1114", {"start": v(10.38, -46) * mm, "end": v(10.12, -44.57) * mm});
            skLineSegment(sketch, "E1115", {"start": v(10.12, -44.57) * mm, "end": v(10.36, -43.2) * mm});
            skLineSegment(sketch, "E1116", {"start": v(10.36, -43.2) * mm, "end": v(11.06, -42.16) * mm});
            skLineSegment(sketch, "E1117", {"start": v(11.06, -42.16) * mm, "end": v(11.98, -41.58) * mm});
            skLineSegment(sketch, "E1118", {"start": v(11.98, -41.58) * mm, "end": v(13.11, -41.38) * mm});
            skLineSegment(sketch, "E1119", {"start": v(12.99, -43.02) * mm, "end": v(12.6, -43.24) * mm});
            skLineSegment(sketch, "E1120", {"start": v(12.6, -43.24) * mm, "end": v(12.47, -43.9) * mm});
            skLineSegment(sketch, "E1121", {"start": v(12.47, -43.9) * mm, "end": v(12.9, -45.95) * mm});
            skLineSegment(sketch, "E1122", {"start": v(12.9, -45.95) * mm, "end": v(13.37, -46.3) * mm});
            skLineSegment(sketch, "E1123", {"start": v(13.37, -46.3) * mm, "end": v(13.74, -46.08) * mm});
            skLineSegment(sketch, "E1124", {"start": v(13.74, -46.08) * mm, "end": v(13.87, -45.41) * mm});
            skLineSegment(sketch, "E1125", {"start": v(13.87, -45.41) * mm, "end": v(13.76, -44.35) * mm});
            skLineSegment(sketch, "E1126", {"start": v(13.76, -44.35) * mm, "end": v(13.49, -43.43) * mm});
            skLineSegment(sketch, "E1127", {"start": v(13.49, -43.43) * mm, "end": v(12.99, -43.02) * mm});
            skLineSegment(sketch, "E1128", {"start": v(17.18, -46.67) * mm, "end": v(17.54, -46.7) * mm});
            skLineSegment(sketch, "E1129", {"start": v(17.54, -46.7) * mm, "end": v(17.75, -46.73) * mm});
            skLineSegment(sketch, "E1130", {"start": v(17.75, -46.73) * mm, "end": v(18.3, -45.99) * mm});
            skLineSegment(sketch, "E1131", {"start": v(18.3, -45.99) * mm, "end": v(18.33, -43.6) * mm});
            skLineSegment(sketch, "E1132", {"start": v(18.33, -43.6) * mm, "end": v(18.21, -43.2) * mm});
            skLineSegment(sketch, "E1133", {"start": v(18.21, -43.2) * mm, "end": v(17.77, -43.08) * mm});
            skLineSegment(sketch, "E1134", {"start": v(17.77, -43.08) * mm, "end": v(17.55, -43.1) * mm});
            skLineSegment(sketch, "E1135", {"start": v(17.55, -43.1) * mm, "end": v(17.36, -43.1) * mm});
            skLineSegment(sketch, "E1136", {"start": v(17.36, -43.1) * mm, "end": v(17.05, -43) * mm});
            skLineSegment(sketch, "E1137", {"start": v(17.05, -43) * mm, "end": v(16.94, -42.74) * mm});
            skLineSegment(sketch, "E1138", {"start": v(16.94, -42.74) * mm, "end": v(17.11, -42.4) * mm});
            skLineSegment(sketch, "E1139", {"start": v(17.11, -42.4) * mm, "end": v(17.6, -42.08) * mm});
            skLineSegment(sketch, "E1140", {"start": v(17.6, -42.08) * mm, "end": v(20.92, -41.42) * mm});
            skLineSegment(sketch, "E1141", {"start": v(20.92, -41.42) * mm, "end": v(21.62, -41.54) * mm});
            skLineSegment(sketch, "E1142", {"start": v(21.62, -41.54) * mm, "end": v(21.84, -41.9) * mm});
            skLineSegment(sketch, "E1143", {"start": v(21.84, -41.9) * mm, "end": v(21.77, -42.12) * mm});
            skLineSegment(sketch, "E1144", {"start": v(21.77, -42.12) * mm, "end": v(21.48, -42.3) * mm});
            skLineSegment(sketch, "E1145", {"start": v(21.48, -42.3) * mm, "end": v(21.09, -42.65) * mm});
            skLineSegment(sketch, "E1146", {"start": v(21.09, -42.65) * mm, "end": v(21.01, -44.33) * mm});
            skLineSegment(sketch, "E1147", {"start": v(21.01, -44.33) * mm, "end": v(21.06, -45.91) * mm});
            skLineSegment(sketch, "E1148", {"start": v(21.06, -45.91) * mm, "end": v(21.1, -46.2) * mm});
            skLineSegment(sketch, "E1149", {"start": v(21.1, -46.2) * mm, "end": v(21.35, -46.6) * mm});
            skLineSegment(sketch, "E1150", {"start": v(21.35, -46.6) * mm, "end": v(22, -46.74) * mm});
            skLineSegment(sketch, "E1151", {"start": v(22, -46.74) * mm, "end": v(22.51, -47.16) * mm});
            skLineSegment(sketch, "E1152", {"start": v(22.51, -47.16) * mm, "end": v(21.78, -47.72) * mm});
            skLineSegment(sketch, "E1153", {"start": v(21.78, -47.72) * mm, "end": v(19.68, -47.9) * mm});
            skLineSegment(sketch, "E1154", {"start": v(19.68, -47.9) * mm, "end": v(18.35, -47.81) * mm});
            skLineSegment(sketch, "E1155", {"start": v(18.35, -47.81) * mm, "end": v(17.12, -47.54) * mm});
            skLineSegment(sketch, "E1156", {"start": v(17.12, -47.54) * mm, "end": v(16.7, -47.08) * mm});
            skLineSegment(sketch, "E1157", {"start": v(16.7, -47.08) * mm, "end": v(16.84, -46.8) * mm});
            skLineSegment(sketch, "E1158", {"start": v(16.84, -46.8) * mm, "end": v(17.18, -46.67) * mm});
            skLineSegment(sketch, "E1159", {"start": v(25.42, -40.57) * mm, "end": v(26.2, -40.74) * mm});
            skLineSegment(sketch, "E1160", {"start": v(26.2, -40.74) * mm, "end": v(26.68, -40.97) * mm});
            skLineSegment(sketch, "E1161", {"start": v(26.68, -40.97) * mm, "end": v(26.88, -41.2) * mm});
            skLineSegment(sketch, "E1162", {"start": v(26.88, -41.2) * mm, "end": v(26.82, -41.38) * mm});
            skLineSegment(sketch, "E1163", {"start": v(26.82, -41.38) * mm, "end": v(26.41, -41.84) * mm});
            skLineSegment(sketch, "E1164", {"start": v(26.41, -41.84) * mm, "end": v(26.02, -42.42) * mm});
            skLineSegment(sketch, "E1165", {"start": v(26.02, -42.42) * mm, "end": v(25.85, -42.93) * mm});
            skLineSegment(sketch, "E1166", {"start": v(25.85, -42.93) * mm, "end": v(25.9, -43.07) * mm});
            skLineSegment(sketch, "E1167", {"start": v(25.9, -43.07) * mm, "end": v(26.02, -43.12) * mm});
            skLineSegment(sketch, "E1168", {"start": v(26.02, -43.12) * mm, "end": v(26.41, -43) * mm});
            skLineSegment(sketch, "E1169", {"start": v(26.41, -43) * mm, "end": v(27.27, -42.84) * mm});
            skLineSegment(sketch, "E1170", {"start": v(27.27, -42.84) * mm, "end": v(28.54, -43.28) * mm});
            skLineSegment(sketch, "E1171", {"start": v(28.54, -43.28) * mm, "end": v(29.13, -44) * mm});
            skLineSegment(sketch, "E1172", {"start": v(29.13, -44) * mm, "end": v(29.33, -44.93) * mm});
            skLineSegment(sketch, "E1173", {"start": v(29.33, -44.93) * mm, "end": v(28.85, -46.5) * mm});
            skLineSegment(sketch, "E1174", {"start": v(28.85, -46.5) * mm, "end": v(27.75, -47.55) * mm});
            skLineSegment(sketch, "E1175", {"start": v(27.75, -47.55) * mm, "end": v(26.2, -47.9) * mm});
            skLineSegment(sketch, "E1176", {"start": v(26.2, -47.9) * mm, "end": v(24.9, -47.68) * mm});
            skLineSegment(sketch, "E1177", {"start": v(24.9, -47.68) * mm, "end": v(23.86, -47.05) * mm});
            skLineSegment(sketch, "E1178", {"start": v(23.86, -47.05) * mm, "end": v(23.1, -45.87) * mm});
            skLineSegment(sketch, "E1179", {"start": v(23.1, -45.87) * mm, "end": v(22.87, -44.69) * mm});
            skLineSegment(sketch, "E1180", {"start": v(22.87, -44.69) * mm, "end": v(23.15, -43.28) * mm});
            skLineSegment(sketch, "E1181", {"start": v(23.15, -43.28) * mm, "end": v(23.99, -41.83) * mm});
            skLineSegment(sketch, "E1182", {"start": v(23.99, -41.83) * mm, "end": v(24.84, -40.86) * mm});
            skLineSegment(sketch, "E1183", {"start": v(24.84, -40.86) * mm, "end": v(25.42, -40.57) * mm});
            skLineSegment(sketch, "E1184", {"start": v(26.02, -44.4) * mm, "end": v(25.63, -44.57) * mm});
            skLineSegment(sketch, "E1185", {"start": v(25.63, -44.57) * mm, "end": v(25.5, -45.04) * mm});
            skLineSegment(sketch, "E1186", {"start": v(25.5, -45.04) * mm, "end": v(25.82, -45.95) * mm});
            skLineSegment(sketch, "E1187", {"start": v(25.82, -45.95) * mm, "end": v(26.48, -46.4) * mm});
            skLineSegment(sketch, "E1188", {"start": v(26.48, -46.4) * mm, "end": v(26.84, -46.27) * mm});
            skLineSegment(sketch, "E1189", {"start": v(26.84, -46.27) * mm, "end": v(26.98, -45.9) * mm});
            skLineSegment(sketch, "E1190", {"start": v(26.98, -45.9) * mm, "end": v(26.82, -45.14) * mm});
            skLineSegment(sketch, "E1191", {"start": v(26.82, -45.14) * mm, "end": v(26.41, -44.55) * mm});
            skLineSegment(sketch, "E1192", {"start": v(26.41, -44.55) * mm, "end": v(26.02, -44.4) * mm});
            skSolve(sketch);
        }
        {
            var Q0;
            Q0=makeQuery(id+"F4.imprint","IMPRINT",FACE,{"disambiguationData":[TD([[makeQuery(id+"F4.imprint","IMPRINT",EDGE,{"derivedFrom":sQuery(id+"F4.wireOp",EDGE,"E842")}),-1.0]])]});
            var Q1;
            Q1=makeQuery(id+"F4.imprint","IMPRINT",FACE,{"disambiguationData":[TD([[makeQuery(id+"F4.imprint","IMPRINT",EDGE,{"derivedFrom":sQuery(id+"F4.wireOp",EDGE,"E869")}),-1.0]])]});
            var Q2;
            Q2=makeQuery(id+"F4.imprint","IMPRINT",FACE,{"disambiguationData":[TD([[makeQuery(id+"F4.imprint","IMPRINT",EDGE,{"derivedFrom":sQuery(id+"F4.wireOp",EDGE,"E905")}),-1.0]])]});
            var Q3;
            Q3=makeQuery(id+"F4.imprint","IMPRINT",FACE,{"disambiguationData":[TD([[makeQuery(id+"F4.imprint","IMPRINT",EDGE,{"derivedFrom":sQuery(id+"F4.wireOp",EDGE,"E941")}),-1.0]])]});
            var Q4;
            Q4=makeQuery(id+"F4.imprint","IMPRINT",FACE,{"disambiguationData":[TD([[makeQuery(id+"F4.imprint","IMPRINT",EDGE,{"derivedFrom":sQuery(id+"F4.wireOp",EDGE,"E966")}),-1.0]])]});
            var Q5;
            Q5=makeQuery(id+"F4.imprint","IMPRINT",FACE,{"disambiguationData":[TD([[makeQuery(id+"F4.imprint","IMPRINT",EDGE,{"derivedFrom":sQuery(id+"F4.wireOp",EDGE,"E1003")}),-1.0]])]});
            var Q6;
            Q6=makeQuery(id+"F4.imprint","IMPRINT",FACE,{"disambiguationData":[TD([[makeQuery(id+"F4.imprint","IMPRINT",EDGE,{"derivedFrom":sQuery(id+"F4.wireOp",EDGE,"E1038")}),-1.0]])]});
            var Q7;
            Q7=makeQuery(id+"F4.imprint","IMPRINT",FACE,{"disambiguationData":[TD([[makeQuery(id+"F4.imprint","IMPRINT",EDGE,{"derivedFrom":sQuery(id+"F4.wireOp",EDGE,"E1068")}),-1.0]])]});
            var Q8;
            Q8=makeQuery(id+"F4.imprint","IMPRINT",FACE,{"disambiguationData":[TD([[makeQuery(id+"F4.imprint","IMPRINT",EDGE,{"derivedFrom":sQuery(id+"F4.wireOp",EDGE,"E1105")}),-1.0]])]});
            var Q9;
            Q9=makeQuery(id+"F4.imprint","IMPRINT",FACE,{"disambiguationData":[TD([[makeQuery(id+"F4.imprint","IMPRINT",EDGE,{"derivedFrom":sQuery(id+"F4.wireOp",EDGE,"E1128")}),-1.0]])]});
            var Q10;
            Q10=makeQuery(id+"F4.imprint","IMPRINT",FACE,{"disambiguationData":[TD([[makeQuery(id+"F4.imprint","IMPRINT",EDGE,{"derivedFrom":sQuery(id+"F4.wireOp",EDGE,"E1159")}),-1.0]])]});
            var Q11;
            Q11=makeQuery(id+"F4.imprint","IMPRINT",FACE,{"disambiguationData":[TD([[makeQuery(id+"F4.imprint","IMPRINT",EDGE,{"derivedFrom":sQuery(id+"F4.wireOp",EDGE,"E804")}),1.0]])]});
            extrude(context, id + "F5", {"entities" : qUnion([Q0, Q1, Q2, Q3, Q4, Q5, Q6, Q7, Q8, Q9, Q10, Q11]), "operationType" : NewBodyOperationType.REMOVE, "oppositeDirection" : true, "depth" : 1 * mm});
        }
        {
            var Q0;
            Q0=makeQuery(id+"F4.imprint","IMPRINT",FACE,{"disambiguationData":[TD([[makeQuery(id+"F4.imprint","IMPRINT",EDGE,{"derivedFrom":sQuery(id+"F4.wireOp",EDGE,"E434")}),1.0]])]});
            var Q1;
            {var subQ0=sQuery(id+"F4.wireOp",EDGE,"E487");Q1=makeQuery(id+"F4.imprint","IMPRINT",FACE,{"disambiguationData":[TD([[makeQuery(id+"F4.imprint","IMPRINT",EDGE,{"derivedFrom":subQ0}),1.0]])]});}
            var Q2;
            Q2=makeQuery(id+"F4.imprint","IMPRINT",FACE,{"disambiguationData":[TD([[makeQuery(id+"F4.imprint","IMPRINT",EDGE,{"derivedFrom":sQuery(id+"F4.wireOp",EDGE,"E416")}),1.0]])]});
            var Q3;
            {var subQ4=sQuery(id+"F4.wireOp",EDGE,"E473");Q3=makeQuery(id+"F4.imprint","IMPRINT",FACE,{"disambiguationData":[TD([[makeQuery(id+"F4.imprint","IMPRINT",EDGE,{"derivedFrom":subQ4}),1.0]])]});}
            var Q4;
            {var subQ0=sQuery(id+"F4.wireOp",EDGE,"E505");Q4=makeQuery(id+"F4.imprint","IMPRINT",FACE,{"disambiguationData":[TD([[makeQuery(id+"F4.imprint","IMPRINT",EDGE,{"derivedFrom":subQ0}),1.0]])]});}
            var Q5;
            Q5=makeQuery(id+"F4.imprint","IMPRINT",FACE,{"disambiguationData":[TD([[makeQuery(id+"F4.imprint","IMPRINT",EDGE,{"derivedFrom":sQuery(id+"F4.wireOp",EDGE,"E452")}),1.0]])]});
            var Q6;
            {var subQ0=sQuery(id+"F4.wireOp",EDGE,"E339");Q6=makeQuery(id+"F4.imprint","IMPRINT",FACE,{"disambiguationData":[TD([[makeQuery(id+"F4.imprint","IMPRINT",EDGE,{"derivedFrom":subQ0}),1.0]])]});}
            var Q7;
            Q7=makeQuery(id+"F4.imprint","IMPRINT",FACE,{"disambiguationData":[TD([[makeQuery(id+"F4.imprint","IMPRINT",EDGE,{"derivedFrom":sQuery(id+"F4.wireOp",EDGE,"E285")}),1.0]])]});
            var Q8;
            Q8=makeQuery(id+"F4.imprint","IMPRINT",FACE,{"disambiguationData":[TD([[makeQuery(id+"F4.imprint","IMPRINT",EDGE,{"derivedFrom":sQuery(id+"F4.wireOp",EDGE,"E250")}),1.0]])]});
            var Q9;
            Q9=makeQuery(id+"F4.imprint","IMPRINT",FACE,{"disambiguationData":[TD([[makeQuery(id+"F4.imprint","IMPRINT",EDGE,{"derivedFrom":sQuery(id+"F4.wireOp",EDGE,"E268")}),1.0]])]});
            var Q10;
            {var subQ6=sQuery(id+"F4.wireOp",EDGE,"E271");Q10=makeQuery(id+"F4.imprint","IMPRINT",FACE,{"disambiguationData":[TD([[makeQuery(id+"F4.imprint","IMPRINT",EDGE,{"derivedFrom":subQ6}),1.0]])]});}
            var Q11;
            Q11=makeQuery(id+"F4.imprint","IMPRINT",FACE,{"disambiguationData":[TD([[makeQuery(id+"F4.imprint","IMPRINT",EDGE,{"derivedFrom":sQuery(id+"F4.wireOp",EDGE,"E318")}),1.0]])]});
            var Q12;
            Q12=makeQuery(id+"F4.imprint","IMPRINT",FACE,{"disambiguationData":[TD([[makeQuery(id+"F4.imprint","IMPRINT",EDGE,{"derivedFrom":sQuery(id+"F4.wireOp",EDGE,"E304")}),1.0]])]});
            var Q13;
            {var subQ0=sQuery(id+"F4.wireOp",EDGE,"E160");Q13=makeQuery(id+"F4.imprint","IMPRINT",FACE,{"disambiguationData":[TD([[makeQuery(id+"F4.imprint","IMPRINT",EDGE,{"derivedFrom":subQ0}),1.0]])]});}
            var Q14;
            {var subQ5=sQuery(id+"F4.wireOp",EDGE,"E426");Q14=makeQuery(id+"F4.imprint","IMPRINT",FACE,{"disambiguationData":[TD([[makeQuery(id+"F4.imprint","IMPRINT",EDGE,{"derivedFrom":subQ5}),1.0]])]});}
            var Q15;
            Q15=makeQuery(id+"F4.imprint","IMPRINT",FACE,{"disambiguationData":[TD([[makeQuery(id+"F4.imprint","IMPRINT",EDGE,{"derivedFrom":sQuery(id+"F4.wireOp",EDGE,"E150")}),1.0]])]});
            var Q16;
            Q16=makeQuery(id+"F4.imprint","IMPRINT",FACE,{"disambiguationData":[TD([[makeQuery(id+"F4.imprint","IMPRINT",EDGE,{"derivedFrom":sQuery(id+"F4.wireOp",EDGE,"E168")}),1.0]])]});
            var Q17;
            Q17=makeQuery(id+"F4.imprint","IMPRINT",FACE,{"disambiguationData":[TD([[makeQuery(id+"F4.imprint","IMPRINT",EDGE,{"derivedFrom":sQuery(id+"F4.wireOp",EDGE,"E129")}),1.0]])]});
            var Q18;
            {var subQ0=sQuery(id+"F4.wireOp",EDGE,"E140");Q18=makeQuery(id+"F4.imprint","IMPRINT",FACE,{"disambiguationData":[TD([[makeQuery(id+"F4.imprint","IMPRINT",EDGE,{"derivedFrom":subQ0}),1.0]])]});}
            var Q19;
            {var subQ0=sQuery(id+"F4.wireOp",EDGE,"E83");Q19=makeQuery(id+"F4.imprint","IMPRINT",FACE,{"disambiguationData":[TD([[makeQuery(id+"F4.imprint","IMPRINT",EDGE,{"derivedFrom":subQ0}),1.0]])]});}
            var Q20;
            {var subQ0=sQuery(id+"F4.wireOp",EDGE,"E89");Q20=makeQuery(id+"F4.imprint","IMPRINT",FACE,{"disambiguationData":[TD([[makeQuery(id+"F4.imprint","IMPRINT",EDGE,{"derivedFrom":subQ0}),1.0]])]});}
            var Q21;
            Q21=makeQuery(id+"F4.imprint","IMPRINT",FACE,{"disambiguationData":[TD([[makeQuery(id+"F4.imprint","IMPRINT",EDGE,{"derivedFrom":sQuery(id+"F4.wireOp",EDGE,"E101")}),1.0]])]});
            var Q22;
            Q22=makeQuery(id+"F4.imprint","IMPRINT",FACE,{"disambiguationData":[TD([[makeQuery(id+"F4.imprint","IMPRINT",EDGE,{"derivedFrom":sQuery(id+"F4.wireOp",EDGE,"E117")}),1.0]])]});
            var Q23;
            Q23=makeQuery(id+"F4.imprint","IMPRINT",FACE,{"disambiguationData":[TD([[makeQuery(id+"F4.imprint","IMPRINT",EDGE,{"derivedFrom":sQuery(id+"F4.wireOp",EDGE,"E335")}),1.0]])]});
            var Q24;
            {var subQ0=sQuery(id+"F4.wireOp",EDGE,"E256");Q24=makeQuery(id+"F4.imprint","IMPRINT",FACE,{"disambiguationData":[TD([[makeQuery(id+"F4.imprint","IMPRINT",EDGE,{"derivedFrom":subQ0}),1.0]])]});}
            var Q25;
            Q25=makeQuery(id+"F4.imprint","IMPRINT",FACE,{"disambiguationData":[TD([[makeQuery(id+"F4.imprint","IMPRINT",EDGE,{"derivedFrom":sQuery(id+"F4.wireOp",EDGE,"E484")}),1.0]])]});
            var Q26;
            Q26=makeQuery(id+"F4.imprint","IMPRINT",FACE,{"disambiguationData":[TD([[makeQuery(id+"F4.imprint","IMPRINT",EDGE,{"derivedFrom":sQuery(id+"F4.wireOp",EDGE,"E500")}),1.0]])]});
            var Q27;
            {var subQ0=sQuery(id+"F4.wireOp",EDGE,"E467");Q27=makeQuery(id+"F4.imprint","IMPRINT",FACE,{"disambiguationData":[TD([[makeQuery(id+"F4.imprint","IMPRINT",EDGE,{"derivedFrom":subQ0}),1.0]])]});}
            var Q28;
            {var subQ10=sQuery(id+"F4.wireOp",EDGE,"E539");Q28=makeQuery(id+"F4.imprint","IMPRINT",FACE,{"disambiguationData":[TD([[makeQuery(id+"F4.imprint","IMPRINT",EDGE,{"derivedFrom":subQ10}),-1.0]])]});}
            var Q29;
            {var subQ10=sQuery(id+"F4.wireOp",EDGE,"E537");Q29=makeQuery(id+"F4.imprint","IMPRINT",FACE,{"disambiguationData":[TD([[makeQuery(id+"F4.imprint","IMPRINT",EDGE,{"derivedFrom":subQ10}),-1.0]])]});}
            var Q30;
            Q30=makeQuery(id+"F4.imprint","IMPRINT",FACE,{"disambiguationData":[TD([[makeQuery(id+"F4.imprint","IMPRINT",EDGE,{"derivedFrom":sQuery(id+"F4.wireOp",EDGE,"E596")}),-1.0]])]});
            var Q31;
            Q31=makeQuery(id+"F4.imprint","IMPRINT",FACE,{"disambiguationData":[TD([[makeQuery(id+"F4.imprint","IMPRINT",EDGE,{"derivedFrom":sQuery(id+"F4.wireOp",EDGE,"E577")}),-1.0]])]});
            var Q32;
            Q32=makeQuery(id+"F4.imprint","IMPRINT",FACE,{"disambiguationData":[TD([[makeQuery(id+"F4.imprint","IMPRINT",EDGE,{"derivedFrom":sQuery(id+"F4.wireOp",EDGE,"E586")}),-1.0]])]});
            var Q33;
            Q33=makeQuery(id+"F4.imprint","IMPRINT",FACE,{"disambiguationData":[TD([[makeQuery(id+"F4.imprint","IMPRINT",EDGE,{"derivedFrom":sQuery(id+"F4.wireOp",EDGE,"E608")}),-1.0]])]});
            var Q34;
            {var subQ0=sQuery(id+"F4.wireOp",EDGE,"E536");var subQ1=sQuery(id+"F4.wireOp",EDGE,"E535");var subQ2=makeQuery(id+"F4.imprint","INTERSECT",VERTEX,{"derivedFrom":[subQ1,subQ0]});Q34=makeQuery(id+"F4.imprint","IMPRINT",FACE,{"disambiguationData":[TD([[makeQuery(id+"F4.imprint","IMPRINT",EDGE,{"disambiguationData":[TD([[subQ2,1.0]])],"derivedFrom":subQ1}),1.0]])]});}
            var Q35;
            Q35=makeQuery(id+"F4.imprint","IMPRINT",FACE,{"disambiguationData":[TD([[makeQuery(id+"F4.imprint","IMPRINT",EDGE,{"derivedFrom":sQuery(id+"F4.wireOp",EDGE,"E518")}),-1.0]])]});
            var Q36;
            {var subQ0=sQuery(id+"F4.wireOp",EDGE,"E636");Q36=makeQuery(id+"F4.imprint","IMPRINT",FACE,{"disambiguationData":[TD([[makeQuery(id+"F4.imprint","IMPRINT",EDGE,{"derivedFrom":subQ0}),1.0]])]});}
            var Q37;
            {var subQ4=sQuery(id+"F4.wireOp",EDGE,"E533");Q37=makeQuery(id+"F4.imprint","IMPRINT",FACE,{"disambiguationData":[TD([[makeQuery(id+"F4.imprint","IMPRINT",EDGE,{"derivedFrom":subQ4}),-1.0]])]});}
            var Q38;
            Q38=makeQuery(id+"F4.imprint","IMPRINT",FACE,{"disambiguationData":[TD([[makeQuery(id+"F4.imprint","IMPRINT",EDGE,{"derivedFrom":sQuery(id+"F4.wireOp",EDGE,"E554")}),-1.0]])]});
            var Q39;
            {var subQ0=sQuery(id+"F4.wireOp",EDGE,"E620");Q39=makeQuery(id+"F4.imprint","IMPRINT",FACE,{"disambiguationData":[TD([[makeQuery(id+"F4.imprint","IMPRINT",EDGE,{"derivedFrom":subQ0}),1.0]])]});}
            var Q40;
            {var subQ0=sQuery(id+"F4.wireOp",EDGE,"E653");Q40=makeQuery(id+"F4.imprint","IMPRINT",FACE,{"disambiguationData":[TD([[makeQuery(id+"F4.imprint","IMPRINT",EDGE,{"derivedFrom":subQ0}),1.0]])]});}
            var Q41;
            Q41=makeQuery(id+"F4.imprint","IMPRINT",FACE,{"disambiguationData":[TD([[makeQuery(id+"F4.imprint","IMPRINT",EDGE,{"derivedFrom":sQuery(id+"F4.wireOp",EDGE,"E626")}),1.0]])]});
            var Q42;
            {var subQ0=sQuery(id+"F4.wireOp",EDGE,"E645");Q42=makeQuery(id+"F4.imprint","IMPRINT",FACE,{"disambiguationData":[TD([[makeQuery(id+"F4.imprint","IMPRINT",EDGE,{"derivedFrom":subQ0}),1.0]])]});}
            var Q43;
            {var subQ0=sQuery(id+"F4.wireOp",EDGE,"E634");Q43=makeQuery(id+"F4.imprint","IMPRINT",FACE,{"disambiguationData":[TD([[makeQuery(id+"F4.imprint","IMPRINT",EDGE,{"derivedFrom":subQ0}),1.0]])]});}
            var Q44;
            {var subQ0=sQuery(id+"F4.wireOp",EDGE,"E651");var subQ1=sQuery(id+"F4.wireOp",EDGE,"E569");var subQ2=makeQuery(id+"F4.imprint","INTERSECT",VERTEX,{"derivedFrom":[subQ1,subQ0]});Q44=makeQuery(id+"F4.imprint","IMPRINT",FACE,{"disambiguationData":[TD([[makeQuery(id+"F4.imprint","IMPRINT",EDGE,{"disambiguationData":[TD([[subQ2,-1.0]])],"derivedFrom":subQ1}),-1.0]])]});}
            var Q45;
            {var subQ0=sQuery(id+"F4.wireOp",EDGE,"E618");Q45=makeQuery(id+"F4.imprint","IMPRINT",FACE,{"disambiguationData":[TD([[makeQuery(id+"F4.imprint","IMPRINT",EDGE,{"derivedFrom":subQ0}),1.0]])]});}
            var Q46;
            {var subQ0=sQuery(id+"F4.wireOp",EDGE,"E565");var subQ1=sQuery(id+"F4.wireOp",EDGE,"E564");var subQ2=makeQuery(id+"F4.imprint","INTERSECT",VERTEX,{"derivedFrom":[subQ1,subQ0]});Q46=makeQuery(id+"F4.imprint","IMPRINT",FACE,{"disambiguationData":[TD([[makeQuery(id+"F4.imprint","IMPRINT",EDGE,{"disambiguationData":[TD([[subQ2,1.0]])],"derivedFrom":subQ1}),-1.0]])]});}
            var Q47;
            Q47=makeQuery(id+"F4.imprint","IMPRINT",FACE,{"disambiguationData":[TD([[makeQuery(id+"F4.imprint","IMPRINT",EDGE,{"derivedFrom":sQuery(id+"F4.wireOp",EDGE,"E642")}),1.0]])]});
            var Q48;
            {var subQ0=sQuery(id+"F4.wireOp",EDGE,"E639");var subQ1=sQuery(id+"F4.wireOp",EDGE,"E538");var subQ2=makeQuery(id+"F4.imprint","INTERSECT",VERTEX,{"derivedFrom":[subQ1,subQ0]});Q48=makeQuery(id+"F4.imprint","IMPRINT",FACE,{"disambiguationData":[TD([[makeQuery(id+"F4.imprint","IMPRINT",EDGE,{"disambiguationData":[TD([[subQ2,-1.0]])],"derivedFrom":subQ1}),1.0]])]});}
            var Q49;
            {var subQ12=sQuery(id+"F4.wireOp",EDGE,"E681");Q49=makeQuery(id+"F4.imprint","IMPRINT",FACE,{"disambiguationData":[TD([[makeQuery(id+"F4.imprint","IMPRINT",EDGE,{"derivedFrom":subQ12}),1.0]])]});}
            var Q50;
            Q50=makeQuery(id+"F4.imprint","IMPRINT",FACE,{"disambiguationData":[TD([[makeQuery(id+"F4.imprint","IMPRINT",EDGE,{"derivedFrom":sQuery(id+"F4.wireOp",EDGE,"E660")}),1.0]])]});
            var Q51;
            {var subQ0=sQuery(id+"F4.wireOp",EDGE,"E678");var subQ1=sQuery(id+"F4.wireOp",EDGE,"E677");var subQ2=makeQuery(id+"F4.imprint","INTERSECT",VERTEX,{"derivedFrom":[subQ1,subQ0]});Q51=makeQuery(id+"F4.imprint","IMPRINT",FACE,{"disambiguationData":[TD([[makeQuery(id+"F4.imprint","IMPRINT",EDGE,{"disambiguationData":[TD([[subQ2,1.0]])],"derivedFrom":subQ1}),-1.0]])]});}
            var Q52;
            Q52=makeQuery(id+"F4.imprint","IMPRINT",FACE,{"disambiguationData":[TD([[makeQuery(id+"F4.imprint","IMPRINT",EDGE,{"derivedFrom":sQuery(id+"F4.wireOp",EDGE,"E729")}),1.0]])]});
            var Q53;
            {var subQ1=sQuery(id+"F4.wireOp",EDGE,"E781");Q53=makeQuery(id+"F4.imprint","IMPRINT",FACE,{"disambiguationData":[TD([[makeQuery(id+"F4.imprint","IMPRINT",EDGE,{"derivedFrom":subQ1}),-1.0]])]});}
            var Q54;
            {var subQ8=sQuery(id+"F4.wireOp",EDGE,"E675");Q54=makeQuery(id+"F4.imprint","IMPRINT",FACE,{"disambiguationData":[TD([[makeQuery(id+"F4.imprint","IMPRINT",EDGE,{"derivedFrom":subQ8}),1.0]])]});}
            var Q55;
            Q55=makeQuery(id+"F4.imprint","IMPRINT",FACE,{"disambiguationData":[TD([[makeQuery(id+"F4.imprint","IMPRINT",EDGE,{"derivedFrom":sQuery(id+"F4.wireOp",EDGE,"E739")}),1.0]])]});
            var Q56;
            Q56=makeQuery(id+"F4.imprint","IMPRINT",FACE,{"disambiguationData":[TD([[makeQuery(id+"F4.imprint","IMPRINT",EDGE,{"derivedFrom":sQuery(id+"F4.wireOp",EDGE,"E720")}),1.0]])]});
            var Q57;
            {var subQ4=sQuery(id+"F4.wireOp",EDGE,"E679");Q57=makeQuery(id+"F4.imprint","IMPRINT",FACE,{"disambiguationData":[TD([[makeQuery(id+"F4.imprint","IMPRINT",EDGE,{"derivedFrom":subQ4}),1.0]])]});}
            var Q58;
            {var subQ0=sQuery(id+"F4.wireOp",EDGE,"E772");Q58=makeQuery(id+"F4.imprint","IMPRINT",FACE,{"disambiguationData":[TD([[makeQuery(id+"F4.imprint","IMPRINT",EDGE,{"derivedFrom":subQ0}),-1.0]])]});}
            var Q59;
            {var subQ0=sQuery(id+"F4.wireOp",EDGE,"E708");var subQ1=sQuery(id+"F4.wireOp",EDGE,"E707");var subQ2=makeQuery(id+"F4.imprint","INTERSECT",VERTEX,{"derivedFrom":[subQ1,subQ0]});Q59=makeQuery(id+"F4.imprint","IMPRINT",FACE,{"disambiguationData":[TD([[makeQuery(id+"F4.imprint","IMPRINT",EDGE,{"disambiguationData":[TD([[subQ2,1.0]])],"derivedFrom":subQ1}),1.0]])]});}
            var Q60;
            {var subQ1=sQuery(id+"F4.wireOp",EDGE,"E764");Q60=makeQuery(id+"F4.imprint","IMPRINT",FACE,{"disambiguationData":[TD([[makeQuery(id+"F4.imprint","IMPRINT",EDGE,{"derivedFrom":subQ1}),-1.0]])]});}
            var Q61;
            Q61=makeQuery(id+"F4.imprint","IMPRINT",FACE,{"disambiguationData":[TD([[makeQuery(id+"F4.imprint","IMPRINT",EDGE,{"derivedFrom":sQuery(id+"F4.wireOp",EDGE,"E751")}),1.0]])]});
            var Q62;
            Q62=makeQuery(id+"F4.imprint","IMPRINT",FACE,{"disambiguationData":[TD([[makeQuery(id+"F4.imprint","IMPRINT",EDGE,{"derivedFrom":sQuery(id+"F4.wireOp",EDGE,"E786")}),-1.0]])]});
            var Q63;
            {var subQ1=sQuery(id+"F4.wireOp",EDGE,"E778");Q63=makeQuery(id+"F4.imprint","IMPRINT",FACE,{"disambiguationData":[TD([[makeQuery(id+"F4.imprint","IMPRINT",EDGE,{"derivedFrom":subQ1}),-1.0]])]});}
            var Q64;
            Q64=makeQuery(id+"F4.imprint","IMPRINT",FACE,{"disambiguationData":[TD([[makeQuery(id+"F4.imprint","IMPRINT",EDGE,{"derivedFrom":sQuery(id+"F4.wireOp",EDGE,"E697")}),1.0]])]});
            var Q65;
            Q65=makeQuery(id+"F4.imprint","IMPRINT",FACE,{"disambiguationData":[TD([[makeQuery(id+"F4.imprint","IMPRINT",EDGE,{"derivedFrom":sQuery(id+"F4.wireOp",EDGE,"E761")}),-1.0]])]});
            var Q66;
            {var subQ0=sQuery(id+"F4.wireOp",EDGE,"E797");Q66=makeQuery(id+"F4.imprint","IMPRINT",FACE,{"disambiguationData":[TD([[makeQuery(id+"F4.imprint","IMPRINT",EDGE,{"derivedFrom":subQ0}),-1.0]])]});}
            var Q67;
            {var subQ0=sQuery(id+"F4.wireOp",EDGE,"E770");Q67=makeQuery(id+"F4.imprint","IMPRINT",FACE,{"disambiguationData":[TD([[makeQuery(id+"F4.imprint","IMPRINT",EDGE,{"derivedFrom":subQ0}),-1.0]])]});}
            var Q68;
            {var subQ0=sQuery(id+"F4.wireOp",EDGE,"E783");var subQ1=sQuery(id+"F4.wireOp",EDGE,"E680");var subQ2=makeQuery(id+"F4.imprint","INTERSECT",VERTEX,{"derivedFrom":[subQ1,subQ0]});Q68=makeQuery(id+"F4.imprint","IMPRINT",FACE,{"disambiguationData":[TD([[makeQuery(id+"F4.imprint","IMPRINT",EDGE,{"disambiguationData":[TD([[subQ2,-1.0]])],"derivedFrom":subQ1}),-1.0]])]});}
            var Q69;
            {var subQ0=sQuery(id+"F4.wireOp",EDGE,"E795");var subQ1=sQuery(id+"F4.wireOp",EDGE,"E712");var subQ2=makeQuery(id+"F4.imprint","INTERSECT",VERTEX,{"derivedFrom":[subQ1,subQ0]});Q69=makeQuery(id+"F4.imprint","IMPRINT",FACE,{"disambiguationData":[TD([[makeQuery(id+"F4.imprint","IMPRINT",EDGE,{"disambiguationData":[TD([[subQ2,-1.0]])],"derivedFrom":subQ1}),1.0]])]});}
            extrude(context, id + "F6", {"entities" : qUnion([Q0, Q1, Q2, Q3, Q4, Q5, Q6, Q7, Q8, Q9, Q10, Q11, Q12, Q13, Q14, Q15, Q16, Q17, Q18, Q19, Q20, Q21, Q22, Q23, Q24, Q25, Q26, Q27, Q28, Q29, Q30, Q31, Q32, Q33, Q34, Q35, Q36, Q37, Q38, Q39, Q40, Q41, Q42, Q43, Q44, Q45, Q46, Q47, Q48, Q49, Q50, Q51, Q52, Q53, Q54, Q55, Q56, Q57, Q58, Q59, Q60, Q61, Q62, Q63, Q64, Q65, Q66, Q67, Q68, Q69]), "operationType" : NewBodyOperationType.ADD, "oppositeDirection" : true, "depth" : 2.5 * mm});
        }
        {
            var Q0;
            {var subQ4=sQuery(id+"F4.wireOp",EDGE,"E473");Q0=makeQuery(id+"F4.imprint","IMPRINT",FACE,{"disambiguationData":[TD([[makeQuery(id+"F4.imprint","IMPRINT",EDGE,{"derivedFrom":subQ4}),1.0]])]});}
            var Q1;
            {var subQ0=sQuery(id+"F4.wireOp",EDGE,"E467");Q1=makeQuery(id+"F4.imprint","IMPRINT",FACE,{"disambiguationData":[TD([[makeQuery(id+"F4.imprint","IMPRINT",EDGE,{"derivedFrom":subQ0}),1.0]])]});}
            var Q2;
            {var subQ0=sQuery(id+"F4.wireOp",EDGE,"E505");Q2=makeQuery(id+"F4.imprint","IMPRINT",FACE,{"disambiguationData":[TD([[makeQuery(id+"F4.imprint","IMPRINT",EDGE,{"derivedFrom":subQ0}),1.0]])]});}
            var Q3;
            Q3=makeQuery(id+"F4.imprint","IMPRINT",FACE,{"disambiguationData":[TD([[makeQuery(id+"F4.imprint","IMPRINT",EDGE,{"derivedFrom":sQuery(id+"F4.wireOp",EDGE,"E500")}),1.0]])]});
            var Q4;
            {var subQ0=sQuery(id+"F4.wireOp",EDGE,"E487");Q4=makeQuery(id+"F4.imprint","IMPRINT",FACE,{"disambiguationData":[TD([[makeQuery(id+"F4.imprint","IMPRINT",EDGE,{"derivedFrom":subQ0}),1.0]])]});}
            var Q5;
            Q5=makeQuery(id+"F4.imprint","IMPRINT",FACE,{"disambiguationData":[TD([[makeQuery(id+"F4.imprint","IMPRINT",EDGE,{"derivedFrom":sQuery(id+"F4.wireOp",EDGE,"E484")}),1.0]])]});
            var Q6;
            Q6=makeQuery(id+"F4.imprint","IMPRINT",FACE,{"disambiguationData":[TD([[makeQuery(id+"F4.imprint","IMPRINT",EDGE,{"derivedFrom":sQuery(id+"F4.wireOp",EDGE,"E452")}),1.0]])]});
            var Q7;
            Q7=makeQuery(id+"F4.imprint","IMPRINT",FACE,{"disambiguationData":[TD([[makeQuery(id+"F4.imprint","IMPRINT",EDGE,{"derivedFrom":sQuery(id+"F4.wireOp",EDGE,"E416")}),1.0]])]});
            var Q8;
            {var subQ5=sQuery(id+"F4.wireOp",EDGE,"E426");Q8=makeQuery(id+"F4.imprint","IMPRINT",FACE,{"disambiguationData":[TD([[makeQuery(id+"F4.imprint","IMPRINT",EDGE,{"derivedFrom":subQ5}),1.0]])]});}
            var Q9;
            Q9=makeQuery(id+"F4.imprint","IMPRINT",FACE,{"disambiguationData":[TD([[makeQuery(id+"F4.imprint","IMPRINT",EDGE,{"derivedFrom":sQuery(id+"F4.wireOp",EDGE,"E434")}),1.0]])]});
            var Q10;
            Q10=makeQuery(id+"F4.imprint","IMPRINT",FACE,{"disambiguationData":[TD([[makeQuery(id+"F4.imprint","IMPRINT",EDGE,{"derivedFrom":sQuery(id+"F4.wireOp",EDGE,"E318")}),1.0]])]});
            var Q11;
            {var subQ0=sQuery(id+"F4.wireOp",EDGE,"E339");Q11=makeQuery(id+"F4.imprint","IMPRINT",FACE,{"disambiguationData":[TD([[makeQuery(id+"F4.imprint","IMPRINT",EDGE,{"derivedFrom":subQ0}),1.0]])]});}
            var Q12;
            Q12=makeQuery(id+"F4.imprint","IMPRINT",FACE,{"disambiguationData":[TD([[makeQuery(id+"F4.imprint","IMPRINT",EDGE,{"derivedFrom":sQuery(id+"F4.wireOp",EDGE,"E335")}),1.0]])]});
            var Q13;
            Q13=makeQuery(id+"F4.imprint","IMPRINT",FACE,{"disambiguationData":[TD([[makeQuery(id+"F4.imprint","IMPRINT",EDGE,{"derivedFrom":sQuery(id+"F4.wireOp",EDGE,"E285")}),1.0]])]});
            var Q14;
            Q14=makeQuery(id+"F4.imprint","IMPRINT",FACE,{"disambiguationData":[TD([[makeQuery(id+"F4.imprint","IMPRINT",EDGE,{"derivedFrom":sQuery(id+"F4.wireOp",EDGE,"E304")}),1.0]])]});
            var Q15;
            Q15=makeQuery(id+"F4.imprint","IMPRINT",FACE,{"disambiguationData":[TD([[makeQuery(id+"F4.imprint","IMPRINT",EDGE,{"derivedFrom":sQuery(id+"F4.wireOp",EDGE,"E250")}),1.0]])]});
            var Q16;
            {var subQ0=sQuery(id+"F4.wireOp",EDGE,"E256");Q16=makeQuery(id+"F4.imprint","IMPRINT",FACE,{"disambiguationData":[TD([[makeQuery(id+"F4.imprint","IMPRINT",EDGE,{"derivedFrom":subQ0}),1.0]])]});}
            var Q17;
            Q17=makeQuery(id+"F4.imprint","IMPRINT",FACE,{"disambiguationData":[TD([[makeQuery(id+"F4.imprint","IMPRINT",EDGE,{"derivedFrom":sQuery(id+"F4.wireOp",EDGE,"E268")}),1.0]])]});
            var Q18;
            {var subQ6=sQuery(id+"F4.wireOp",EDGE,"E271");Q18=makeQuery(id+"F4.imprint","IMPRINT",FACE,{"disambiguationData":[TD([[makeQuery(id+"F4.imprint","IMPRINT",EDGE,{"derivedFrom":subQ6}),1.0]])]});}
            var Q19;
            Q19=makeQuery(id+"F4.imprint","IMPRINT",FACE,{"disambiguationData":[TD([[makeQuery(id+"F4.imprint","IMPRINT",EDGE,{"derivedFrom":sQuery(id+"F4.wireOp",EDGE,"E168")}),1.0]])]});
            var Q20;
            Q20=makeQuery(id+"F4.imprint","IMPRINT",FACE,{"disambiguationData":[TD([[makeQuery(id+"F4.imprint","IMPRINT",EDGE,{"derivedFrom":sQuery(id+"F4.wireOp",EDGE,"E150")}),1.0]])]});
            var Q21;
            {var subQ0=sQuery(id+"F4.wireOp",EDGE,"E160");Q21=makeQuery(id+"F4.imprint","IMPRINT",FACE,{"disambiguationData":[TD([[makeQuery(id+"F4.imprint","IMPRINT",EDGE,{"derivedFrom":subQ0}),1.0]])]});}
            var Q22;
            Q22=makeQuery(id+"F4.imprint","IMPRINT",FACE,{"disambiguationData":[TD([[makeQuery(id+"F4.imprint","IMPRINT",EDGE,{"derivedFrom":sQuery(id+"F4.wireOp",EDGE,"E117")}),1.0]])]});
            var Q23;
            Q23=makeQuery(id+"F4.imprint","IMPRINT",FACE,{"disambiguationData":[TD([[makeQuery(id+"F4.imprint","IMPRINT",EDGE,{"derivedFrom":sQuery(id+"F4.wireOp",EDGE,"E129")}),1.0]])]});
            var Q24;
            {var subQ0=sQuery(id+"F4.wireOp",EDGE,"E140");Q24=makeQuery(id+"F4.imprint","IMPRINT",FACE,{"disambiguationData":[TD([[makeQuery(id+"F4.imprint","IMPRINT",EDGE,{"derivedFrom":subQ0}),1.0]])]});}
            var Q25;
            {var subQ0=sQuery(id+"F4.wireOp",EDGE,"E83");Q25=makeQuery(id+"F4.imprint","IMPRINT",FACE,{"disambiguationData":[TD([[makeQuery(id+"F4.imprint","IMPRINT",EDGE,{"derivedFrom":subQ0}),1.0]])]});}
            var Q26;
            {var subQ0=sQuery(id+"F4.wireOp",EDGE,"E89");Q26=makeQuery(id+"F4.imprint","IMPRINT",FACE,{"disambiguationData":[TD([[makeQuery(id+"F4.imprint","IMPRINT",EDGE,{"derivedFrom":subQ0}),1.0]])]});}
            var Q27;
            Q27=makeQuery(id+"F4.imprint","IMPRINT",FACE,{"disambiguationData":[TD([[makeQuery(id+"F4.imprint","IMPRINT",EDGE,{"derivedFrom":sQuery(id+"F4.wireOp",EDGE,"E101")}),1.0]])]});
            var Q28;
            Q28=makeQuery(id+"F4.imprint","IMPRINT",FACE,{"disambiguationData":[TD([[makeQuery(id+"F4.imprint","IMPRINT",EDGE,{"derivedFrom":sQuery(id+"F4.wireOp",EDGE,"E660")}),1.0]])]});
            var Q29;
            {var subQ12=sQuery(id+"F4.wireOp",EDGE,"E681");Q29=makeQuery(id+"F4.imprint","IMPRINT",FACE,{"disambiguationData":[TD([[makeQuery(id+"F4.imprint","IMPRINT",EDGE,{"derivedFrom":subQ12}),1.0]])]});}
            var Q30;
            {var subQ4=sQuery(id+"F4.wireOp",EDGE,"E679");Q30=makeQuery(id+"F4.imprint","IMPRINT",FACE,{"disambiguationData":[TD([[makeQuery(id+"F4.imprint","IMPRINT",EDGE,{"derivedFrom":subQ4}),1.0]])]});}
            var Q31;
            {var subQ8=sQuery(id+"F4.wireOp",EDGE,"E675");Q31=makeQuery(id+"F4.imprint","IMPRINT",FACE,{"disambiguationData":[TD([[makeQuery(id+"F4.imprint","IMPRINT",EDGE,{"derivedFrom":subQ8}),1.0]])]});}
            var Q32;
            Q32=makeQuery(id+"F4.imprint","IMPRINT",FACE,{"disambiguationData":[TD([[makeQuery(id+"F4.imprint","IMPRINT",EDGE,{"derivedFrom":sQuery(id+"F4.wireOp",EDGE,"E518")}),-1.0]])]});
            var Q33;
            {var subQ10=sQuery(id+"F4.wireOp",EDGE,"E539");Q33=makeQuery(id+"F4.imprint","IMPRINT",FACE,{"disambiguationData":[TD([[makeQuery(id+"F4.imprint","IMPRINT",EDGE,{"derivedFrom":subQ10}),-1.0]])]});}
            var Q34;
            {var subQ10=sQuery(id+"F4.wireOp",EDGE,"E537");Q34=makeQuery(id+"F4.imprint","IMPRINT",FACE,{"disambiguationData":[TD([[makeQuery(id+"F4.imprint","IMPRINT",EDGE,{"derivedFrom":subQ10}),-1.0]])]});}
            var Q35;
            {var subQ4=sQuery(id+"F4.wireOp",EDGE,"E533");Q35=makeQuery(id+"F4.imprint","IMPRINT",FACE,{"disambiguationData":[TD([[makeQuery(id+"F4.imprint","IMPRINT",EDGE,{"derivedFrom":subQ4}),-1.0]])]});}
            extrude(context, id + "F7", {"entities" : qUnion([Q0, Q1, Q2, Q3, Q4, Q5, Q6, Q7, Q8, Q9, Q10, Q11, Q12, Q13, Q14, Q15, Q16, Q17, Q18, Q19, Q20, Q21, Q22, Q23, Q24, Q25, Q26, Q27, Q28, Q29, Q30, Q31, Q32, Q33, Q34, Q35]), "operationType" : NewBodyOperationType.ADD, "depth" : 2.5 * mm});
        }
        {
            var Q0;
            Q0=makeQuery(id+"F4.imprint","IMPRINT",FACE,{"disambiguationData":[TD([[makeQuery(id+"F4.imprint","IMPRINT",EDGE,{"derivedFrom":sQuery(id+"F4.wireOp",EDGE,"E554")}),-1.0]])]});
            var Q1;
            {var subQ0=sQuery(id+"F4.wireOp",EDGE,"E653");Q1=makeQuery(id+"F4.imprint","IMPRINT",FACE,{"disambiguationData":[TD([[makeQuery(id+"F4.imprint","IMPRINT",EDGE,{"derivedFrom":subQ0}),1.0]])]});}
            var Q2;
            Q2=makeQuery(id+"F4.imprint","IMPRINT",FACE,{"disambiguationData":[TD([[makeQuery(id+"F4.imprint","IMPRINT",EDGE,{"derivedFrom":sQuery(id+"F4.wireOp",EDGE,"E608")}),-1.0]])]});
            var Q3;
            Q3=makeQuery(id+"F4.imprint","IMPRINT",FACE,{"disambiguationData":[TD([[makeQuery(id+"F4.imprint","IMPRINT",EDGE,{"derivedFrom":sQuery(id+"F4.wireOp",EDGE,"E642")}),1.0]])]});
            var Q4;
            {var subQ0=sQuery(id+"F4.wireOp",EDGE,"E645");Q4=makeQuery(id+"F4.imprint","IMPRINT",FACE,{"disambiguationData":[TD([[makeQuery(id+"F4.imprint","IMPRINT",EDGE,{"derivedFrom":subQ0}),1.0]])]});}
            var Q5;
            {var subQ0=sQuery(id+"F4.wireOp",EDGE,"E636");Q5=makeQuery(id+"F4.imprint","IMPRINT",FACE,{"disambiguationData":[TD([[makeQuery(id+"F4.imprint","IMPRINT",EDGE,{"derivedFrom":subQ0}),1.0]])]});}
            var Q6;
            {var subQ0=sQuery(id+"F4.wireOp",EDGE,"E634");Q6=makeQuery(id+"F4.imprint","IMPRINT",FACE,{"disambiguationData":[TD([[makeQuery(id+"F4.imprint","IMPRINT",EDGE,{"derivedFrom":subQ0}),1.0]])]});}
            var Q7;
            Q7=makeQuery(id+"F4.imprint","IMPRINT",FACE,{"disambiguationData":[TD([[makeQuery(id+"F4.imprint","IMPRINT",EDGE,{"derivedFrom":sQuery(id+"F4.wireOp",EDGE,"E596")}),-1.0]])]});
            var Q8;
            Q8=makeQuery(id+"F4.imprint","IMPRINT",FACE,{"disambiguationData":[TD([[makeQuery(id+"F4.imprint","IMPRINT",EDGE,{"derivedFrom":sQuery(id+"F4.wireOp",EDGE,"E586")}),-1.0]])]});
            var Q9;
            Q9=makeQuery(id+"F4.imprint","IMPRINT",FACE,{"disambiguationData":[TD([[makeQuery(id+"F4.imprint","IMPRINT",EDGE,{"derivedFrom":sQuery(id+"F4.wireOp",EDGE,"E626")}),1.0]])]});
            var Q10;
            {var subQ0=sQuery(id+"F4.wireOp",EDGE,"E618");Q10=makeQuery(id+"F4.imprint","IMPRINT",FACE,{"disambiguationData":[TD([[makeQuery(id+"F4.imprint","IMPRINT",EDGE,{"derivedFrom":subQ0}),1.0]])]});}
            var Q11;
            {var subQ0=sQuery(id+"F4.wireOp",EDGE,"E620");Q11=makeQuery(id+"F4.imprint","IMPRINT",FACE,{"disambiguationData":[TD([[makeQuery(id+"F4.imprint","IMPRINT",EDGE,{"derivedFrom":subQ0}),1.0]])]});}
            var Q12;
            Q12=makeQuery(id+"F4.imprint","IMPRINT",FACE,{"disambiguationData":[TD([[makeQuery(id+"F4.imprint","IMPRINT",EDGE,{"derivedFrom":sQuery(id+"F4.wireOp",EDGE,"E577")}),-1.0]])]});
            var Q13;
            Q13=makeQuery(id+"F4.imprint","IMPRINT",FACE,{"disambiguationData":[TD([[makeQuery(id+"F4.imprint","IMPRINT",EDGE,{"derivedFrom":sQuery(id+"F4.wireOp",EDGE,"E697")}),1.0]])]});
            var Q14;
            Q14=makeQuery(id+"F4.imprint","IMPRINT",FACE,{"disambiguationData":[TD([[makeQuery(id+"F4.imprint","IMPRINT",EDGE,{"derivedFrom":sQuery(id+"F4.wireOp",EDGE,"E720")}),1.0]])]});
            var Q15;
            Q15=makeQuery(id+"F4.imprint","IMPRINT",FACE,{"disambiguationData":[TD([[makeQuery(id+"F4.imprint","IMPRINT",EDGE,{"derivedFrom":sQuery(id+"F4.wireOp",EDGE,"E761")}),-1.0]])]});
            var Q16;
            {var subQ1=sQuery(id+"F4.wireOp",EDGE,"E764");Q16=makeQuery(id+"F4.imprint","IMPRINT",FACE,{"disambiguationData":[TD([[makeQuery(id+"F4.imprint","IMPRINT",EDGE,{"derivedFrom":subQ1}),-1.0]])]});}
            var Q17;
            Q17=makeQuery(id+"F4.imprint","IMPRINT",FACE,{"disambiguationData":[TD([[makeQuery(id+"F4.imprint","IMPRINT",EDGE,{"derivedFrom":sQuery(id+"F4.wireOp",EDGE,"E729")}),1.0]])]});
            var Q18;
            {var subQ0=sQuery(id+"F4.wireOp",EDGE,"E770");Q18=makeQuery(id+"F4.imprint","IMPRINT",FACE,{"disambiguationData":[TD([[makeQuery(id+"F4.imprint","IMPRINT",EDGE,{"derivedFrom":subQ0}),-1.0]])]});}
            var Q19;
            {var subQ0=sQuery(id+"F4.wireOp",EDGE,"E772");Q19=makeQuery(id+"F4.imprint","IMPRINT",FACE,{"disambiguationData":[TD([[makeQuery(id+"F4.imprint","IMPRINT",EDGE,{"derivedFrom":subQ0}),-1.0]])]});}
            var Q20;
            {var subQ1=sQuery(id+"F4.wireOp",EDGE,"E778");Q20=makeQuery(id+"F4.imprint","IMPRINT",FACE,{"disambiguationData":[TD([[makeQuery(id+"F4.imprint","IMPRINT",EDGE,{"derivedFrom":subQ1}),-1.0]])]});}
            var Q21;
            {var subQ1=sQuery(id+"F4.wireOp",EDGE,"E781");Q21=makeQuery(id+"F4.imprint","IMPRINT",FACE,{"disambiguationData":[TD([[makeQuery(id+"F4.imprint","IMPRINT",EDGE,{"derivedFrom":subQ1}),-1.0]])]});}
            var Q22;
            Q22=makeQuery(id+"F4.imprint","IMPRINT",FACE,{"disambiguationData":[TD([[makeQuery(id+"F4.imprint","IMPRINT",EDGE,{"derivedFrom":sQuery(id+"F4.wireOp",EDGE,"E739")}),1.0]])]});
            var Q23;
            Q23=makeQuery(id+"F4.imprint","IMPRINT",FACE,{"disambiguationData":[TD([[makeQuery(id+"F4.imprint","IMPRINT",EDGE,{"derivedFrom":sQuery(id+"F4.wireOp",EDGE,"E786")}),-1.0]])]});
            var Q24;
            Q24=makeQuery(id+"F4.imprint","IMPRINT",FACE,{"disambiguationData":[TD([[makeQuery(id+"F4.imprint","IMPRINT",EDGE,{"derivedFrom":sQuery(id+"F4.wireOp",EDGE,"E751")}),1.0]])]});
            var Q25;
            {var subQ0=sQuery(id+"F4.wireOp",EDGE,"E797");Q25=makeQuery(id+"F4.imprint","IMPRINT",FACE,{"disambiguationData":[TD([[makeQuery(id+"F4.imprint","IMPRINT",EDGE,{"derivedFrom":subQ0}),-1.0]])]});}
            extrude(context, id + "F8", {"entities" : qUnion([Q0, Q1, Q2, Q3, Q4, Q5, Q6, Q7, Q8, Q9, Q10, Q11, Q12, Q13, Q14, Q15, Q16, Q17, Q18, Q19, Q20, Q21, Q22, Q23, Q24, Q25]), "operationType" : NewBodyOperationType.ADD, "depth" : 2 * mm});
        }
        {
            var Q0;
            Q0=makeQuery(id+"F2.opExtrude","SWEPT_FACE",FACE,{"disambiguationData":[OSD([sQuery(id+"F0.wireOp",EDGE,"E0")])]});
            var sketch = newSketch(context, id + "F9", { "sketchPlane" : qUnion([Q0])});
            skLineSegment(sketch, "E1193.bottom", {"start": v(51.14, -9) * mm, "end": v(-43.86, -9) * mm});
            skLineSegment(sketch, "E1193.top", {"start": v(51.14, -5.8) * mm, "end": v(-43.86, -5.8) * mm});
            skLineSegment(sketch, "E1193.left", {"start": v(51.14, -9) * mm, "end": v(51.14, -5.8) * mm});
            skLineSegment(sketch, "E1193.right", {"start": v(-43.86, -9) * mm, "end": v(-43.86, -5.8) * mm});
            skSolve(sketch);
        }
        {
            var Q0;
            Q0=makeQuery(id+"F2.opExtrude","SWEPT_FACE",FACE,{"disambiguationData":[OSD([sQuery(id+"F0.wireOp",EDGE,"E2"),sQuery(id+"F0.wireOp",EDGE,"E16")])]});
            var sketch = newSketch(context, id + "F10", { "sketchPlane" : qUnion([Q0])});
            skLineSegment(sketch, "E1194.bottom", {"start": v(51.6, -9) * mm, "end": v(-97.4, -9) * mm});
            skLineSegment(sketch, "E1194.top", {"start": v(51.6, -5.8) * mm, "end": v(-97.4, -5.8) * mm});
            skLineSegment(sketch, "E1194.left", {"start": v(51.6, -9) * mm, "end": v(51.6, -5.8) * mm});
            skLineSegment(sketch, "E1194.right", {"start": v(-97.4, -9) * mm, "end": v(-97.4, -5.8) * mm});
            skSolve(sketch);
        }
        {
            var Q0;
            Q0=makeQuery(id+"F2.opExtrude","SWEPT_FACE",FACE,{"disambiguationData":[OSD([sQuery(id+"F0.wireOp",EDGE,"E1"),sQuery(id+"F0.wireOp",EDGE,"E15"),sQuery(id+"F0.wireOp",EDGE,"E18.top")])]});
            var sketch = newSketch(context, id + "F11", { "sketchPlane" : qUnion([Q0])});
            skLineSegment(sketch, "E1195.bottom", {"start": v(-51.6, -9) * mm, "end": v(97.4, -9) * mm});
            skLineSegment(sketch, "E1195.top", {"start": v(-51.6, -5.8) * mm, "end": v(97.4, -5.8) * mm});
            skLineSegment(sketch, "E1195.left", {"start": v(-51.6, -9) * mm, "end": v(-51.6, -5.8) * mm});
            skLineSegment(sketch, "E1195.right", {"start": v(97.4, -9) * mm, "end": v(97.4, -5.8) * mm});
            skSolve(sketch);
        }
        {
            var Q0;
            Q0=makeQuery(id+"F9.imprint","IMPRINT",FACE,{"disambiguationData":[TD([[makeQuery(id+"F9.imprint","IMPRINT",EDGE,{"derivedFrom":sQuery(id+"F9.wireOp",EDGE,"E1193.bottom")}),1.0]])]});
            extrude(context, id + "F12", {"entities" : qUnion([Q0]), "operationType" : NewBodyOperationType.ADD, "depth" : 8 * mm});
        }
        {
            var Q0;
            Q0=makeQuery(id+"F10.imprint","IMPRINT",FACE,{"disambiguationData":[TD([[makeQuery(id+"F10.imprint","IMPRINT",EDGE,{"derivedFrom":sQuery(id+"F10.wireOp",EDGE,"E1194.bottom")}),-1.0]])]});
            extrude(context, id + "F13", {"entities" : qUnion([Q0]), "operationType" : NewBodyOperationType.ADD, "depth" : 8 * mm});
        }
        {
            var Q0;
            Q0=makeQuery(id+"F11.imprint","IMPRINT",FACE,{"disambiguationData":[TD([[makeQuery(id+"F11.imprint","IMPRINT",EDGE,{"derivedFrom":sQuery(id+"F11.wireOp",EDGE,"E1195.bottom")}),1.0]])]});
            extrude(context, id + "F14", {"entities" : qUnion([Q0]), "operationType" : NewBodyOperationType.ADD, "depth" : 8 * mm});
        }
        {
            var Q0;
            Q0=makeQuery(id+"F12.opExtrude","CAP_FACE",FACE,{"disambiguationData":[OSD([sQuery(id+"F9.wireOp",EDGE,"E1193.bottom"),sQuery(id+"F9.wireOp",EDGE,"E1193.top"),sQuery(id+"F9.wireOp",EDGE,"E1193.left"),sQuery(id+"F9.wireOp",EDGE,"E1193.right")])],"isStart":false});
            var sketch = newSketch(context, id + "F15", { "sketchPlane" : qUnion([Q0])});
            skLineSegment(sketch, "E1196.bottom", {"start": v(43.14, -9) * mm, "end": v(-35.86, -9) * mm});
            skLineSegment(sketch, "E1196.top", {"start": v(43.14, -8.5) * mm, "end": v(-35.86, -8.5) * mm});
            skLineSegment(sketch, "E1196.left", {"start": v(43.14, -9) * mm, "end": v(43.14, -8.5) * mm});
            skLineSegment(sketch, "E1196.right", {"start": v(-35.86, -9) * mm, "end": v(-35.86, -8.5) * mm});
            skSolve(sketch);
        }
        {
            var Q0;
            Q0=makeQuery(id+"FxxfhiVzZimAMsD_1.boolean.opBoolean","MERGE",FACE,{"derivedFrom":[makeQuery(id+"F14.boolean.opBoolean","MERGE",FACE,{"derivedFrom":[makeQuery(id+"F13.boolean.opBoolean","MERGE",FACE,{"derivedFrom":[makeQuery(id+"F12.boolean.opBoolean","MERGE",FACE,{"derivedFrom":[makeQuery(id+"F2.opExtrude","CAP_FACE",FACE,{"disambiguationData":[OSD([sQuery(id+"F0.wireOp",EDGE,"E0"),sQuery(id+"F0.wireOp",EDGE,"E1"),sQuery(id+"F0.wireOp",EDGE,"E2"),sQuery(id+"F0.wireOp",EDGE,"E3"),sQuery(id+"F0.wireOp",EDGE,"E4"),sQuery(id+"F0.wireOp",EDGE,"E5"),sQuery(id+"F0.wireOp",EDGE,"E6"),sQuery(id+"F0.wireOp",EDGE,"E11"),sQuery(id+"F0.wireOp",EDGE,"E12"),sQuery(id+"F0.wireOp",EDGE,"E13"),sQuery(id+"F0.wireOp",EDGE,"E15"),sQuery(id+"F0.wireOp",EDGE,"E16"),sQuery(id+"F0.wireOp",EDGE,"E18.top")])],"isStart":false}),makeQuery(id+"F12.opExtrude","SWEPT_FACE",FACE,{"disambiguationData":[OSD([sQuery(id+"F9.wireOp",EDGE,"E1193.bottom")])]})]}),makeQuery(id+"F13.opExtrude","SWEPT_FACE",FACE,{"disambiguationData":[OSD([sQuery(id+"F10.wireOp",EDGE,"E1194.bottom")])]})]}),makeQuery(id+"F14.opExtrude","SWEPT_FACE",FACE,{"disambiguationData":[OSD([sQuery(id+"F11.wireOp",EDGE,"E1195.bottom")])]})]}),makeQuery(id+"FxxfhiVzZimAMsD_1.opExtrude","SWEPT_FACE",FACE,{"disambiguationData":[OSD([sQuery(id+"F15.wireOp",EDGE,"E1196.bottom")])]})]});
            var sketch = newSketch(context, id + "F16", { "sketchPlane" : qUnion([Q0])});
            skLineSegment(sketch, "E1197.bottom", {"start": v(-57.6, 52.36) * mm, "end": v(97.4, 52.36) * mm, "construction": true});
            skLineSegment(sketch, "E1197.top", {"start": v(-57.6, -59.64) * mm, "end": v(97.4, -59.64) * mm, "construction": true});
            skLineSegment(sketch, "E1197.left", {"start": v(-57.6, 52.36) * mm, "end": v(-57.6, -59.64) * mm, "construction": true});
            skLineSegment(sketch, "E1197.right", {"start": v(97.4, 52.36) * mm, "end": v(97.4, -59.64) * mm, "construction": true});
            skLineSegment(sketch, "E1198.bottom", {"start": v(-61.1, 55.86) * mm, "end": v(100.9, 55.86) * mm});
            skLineSegment(sketch, "E1198.top", {"start": v(-61.1, -63.14) * mm, "end": v(100.9, -63.14) * mm});
            skLineSegment(sketch, "E1198.left", {"start": v(-61.1, 55.86) * mm, "end": v(-61.1, -63.14) * mm});
            skLineSegment(sketch, "E1198.right", {"start": v(100.9, 55.86) * mm, "end": v(100.9, -63.14) * mm});
            skLineSegment(sketch, "E1199.bottom", {"start": v(-66.1, 60.86) * mm, "end": v(105.9, 60.86) * mm});
            skLineSegment(sketch, "E1199.top", {"start": v(-66.1, -68.14) * mm, "end": v(105.9, -68.14) * mm});
            skLineSegment(sketch, "E1199.left", {"start": v(-66.1, 60.86) * mm, "end": v(-66.1, -68.14) * mm});
            skLineSegment(sketch, "E1199.right", {"start": v(105.9, 60.86) * mm, "end": v(105.9, -68.14) * mm});
            skSolve(sketch);
        }
        {
            var Q0;
            Q0=makeQuery(id+"F16.imprint","IMPRINT",FACE,{"disambiguationData":[TD([[makeQuery(id+"F16.imprint","IMPRINT",EDGE,{"derivedFrom":sQuery(id+"F16.wireOp",EDGE,"E1198.bottom")}),1.0]])]});
            extrude(context, id + "F17", {"entities" : qUnion([Q0]), "oppositeDirection" : true, "depth" : 2 * mm});
        }
        {
            var Q0;
            Q0=makeQuery(id+"F17.opExtrude","SWEPT_BODY",BODY,{"disambiguationData":[OSD([sQuery(id+"F16.wireOp",EDGE,"E1198.bottom"),sQuery(id+"F16.wireOp",EDGE,"E1198.top"),sQuery(id+"F16.wireOp",EDGE,"E1198.left"),sQuery(id+"F16.wireOp",EDGE,"E1198.right"),sQuery(id+"F16.wireOp",EDGE,"E1199.bottom"),sQuery(id+"F16.wireOp",EDGE,"E1199.top"),sQuery(id+"F16.wireOp",EDGE,"E1199.left"),sQuery(id+"F16.wireOp",EDGE,"E1199.right")])]});
            deleteBodies(context, id + "F18", {"entities" : qUnion([Q0])});
        }
    });
